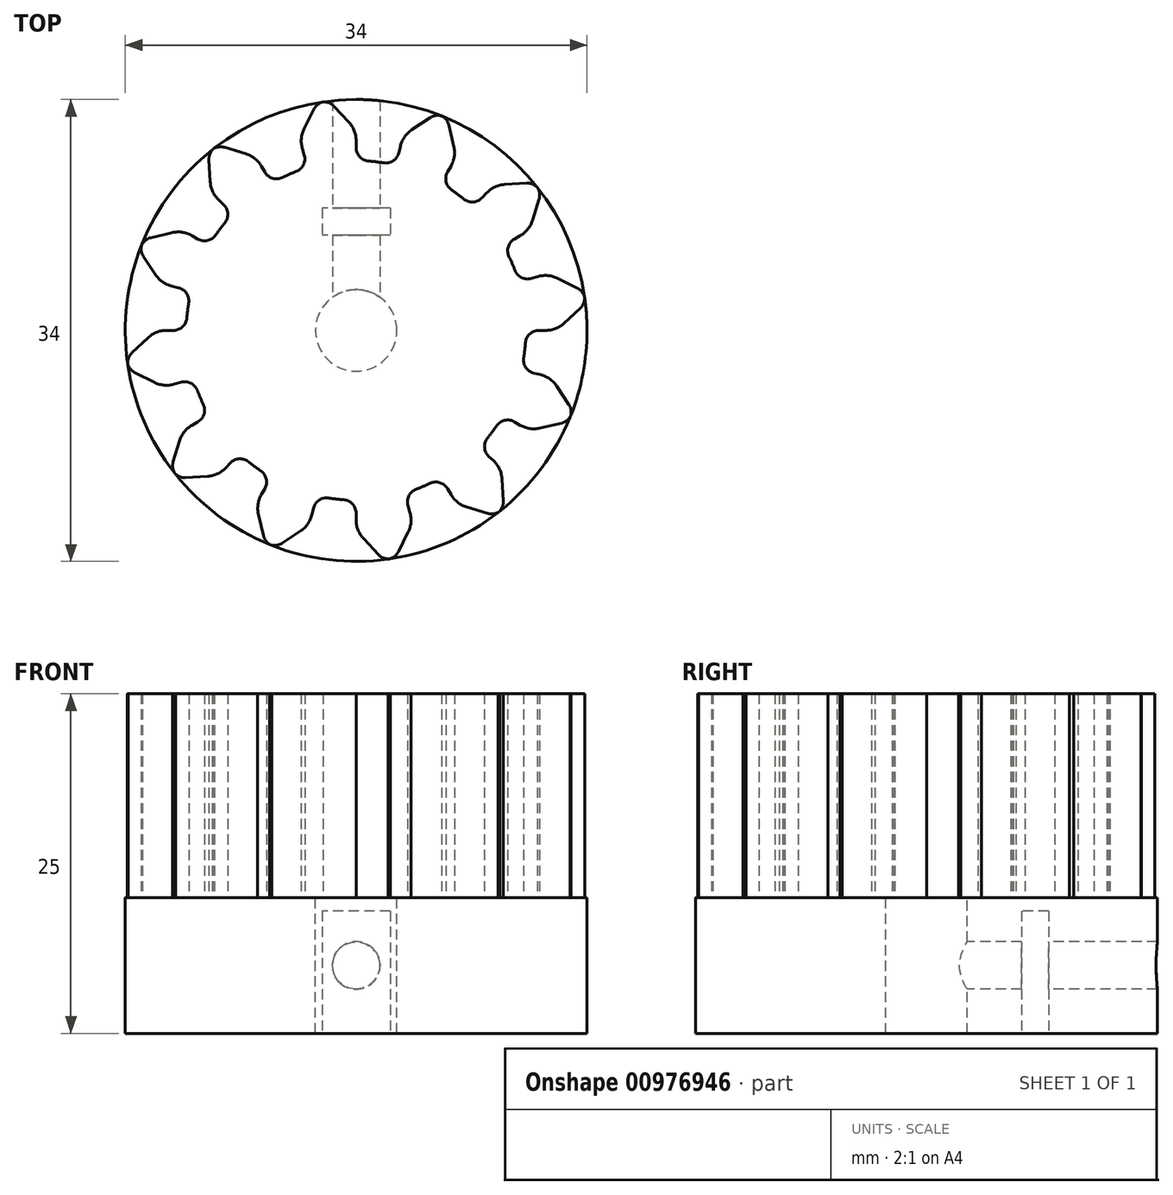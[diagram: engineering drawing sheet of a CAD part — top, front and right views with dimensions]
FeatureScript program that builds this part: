
annotation { "Feature Type Name" : "Feature", "Feature Type Description" : "" }
export const myFeature = defineFeature(function(context is Context, id is Id, definition is map)
    precondition{}
    {
        {
            var Q0;
            Q0=qCreatedBy(makeId("Top.planeOp"),FACE);
            var sketch = newSketch(context, id + "F0", { "sketchPlane" : qUnion([Q0])});
            skLineSegment(sketch, "E0", {"start": v(0, 13.96) * mm, "end": v(0, 13.46) * mm});
            skLineSegment(sketch, "E1", {"start": v(3.15, 13.1) * mm, "end": v(3.26, 13.57) * mm});
            skArc(sketch, "E2", {"start": v(2.01, 12.34) * mm, "mid": v(1.47, 12.41) * mm, "end": v(0.93, 12.47) * mm});
            skLineSegment(sketch, "E3", {"start": v(4.1, 14.78) * mm, "end": v(5.46, 15.67) * mm});
            skLineSegment(sketch, "E4", {"start": v(-0.54, 15.33) * mm, "end": v(-1.64, 16.5) * mm});
            skPoint(sketch, "E5.visualSharp", {"position": v(3.45, 14.34) * mm});
            skArc(sketch, "E5.filletArc", {"start": v(4.1, 14.78) * mm, "mid": v(3.57, 14.26) * mm, "end": v(3.26, 13.57) * mm});
            skPoint(sketch, "E6.visualSharp", {"position": v(0, 14.75) * mm});
            skArc(sketch, "E6.filletArc", {"start": v(0, 13.96) * mm, "mid": v(-0.14, 14.7) * mm, "end": v(-0.54, 15.33) * mm});
            skPoint(sketch, "E7.visualSharp", {"position": v(2.92, 12.15) * mm});
            skArc(sketch, "E7.filletArc", {"start": v(2.01, 12.34) * mm, "mid": v(2.73, 12.5) * mm, "end": v(3.15, 13.1) * mm});
            skPoint(sketch, "E8.visualSharp", {"position": v(0, 12.5) * mm});
            skArc(sketch, "E8.filletArc", {"start": v(0, 13.46) * mm, "mid": v(0.27, 12.78) * mm, "end": v(0.93, 12.47) * mm});
            skPoint(sketch, "E9.visualSharp", {"position": v(-2, 16.88) * mm});
            skArc(sketch, "E9.filletArc", {"start": v(-1.64, 16.5) * mm, "mid": v(-2.05, 16.77) * mm, "end": v(-2.52, 16.81) * mm});
            skPoint(sketch, "E10.visualSharp", {"position": v(5.89, 15.95) * mm});
            skArc(sketch, "E10.filletArc", {"start": v(6.38, 15.76) * mm, "mid": v(5.9, 15.83) * mm, "end": v(5.46, 15.67) * mm});
            skPoint(sketch, "E11.2.0", {"position": v(0, 17) * mm});
            skPoint(sketch, "E11.2.7", {"position": v(3.97, 16.53) * mm});
            skPoint(sketch, "E11.3.0", {"position": v(0, 17) * mm});
            skPoint(sketch, "E11.3.7", {"position": v(3.97, 16.53) * mm});
            skPoint(sketch, "E11.4.0", {"position": v(0, 17) * mm});
            skPoint(sketch, "E11.4.7", {"position": v(3.97, 16.53) * mm});
            skPoint(sketch, "E11.5.0", {"position": v(0, 17) * mm});
            skPoint(sketch, "E11.5.7", {"position": v(3.97, 16.53) * mm});
            skPoint(sketch, "E11.6.0", {"position": v(0, 17) * mm});
            skPoint(sketch, "E11.6.7", {"position": v(3.97, 16.53) * mm});
            skPoint(sketch, "E11.7.0", {"position": v(0, 17) * mm});
            skPoint(sketch, "E11.7.7", {"position": v(3.97, 16.53) * mm});
            skPoint(sketch, "E11.8.0", {"position": v(0, 17) * mm});
            skPoint(sketch, "E11.8.7", {"position": v(3.97, 16.53) * mm});
            skPoint(sketch, "E11.9.0", {"position": v(0, 17) * mm});
            skPoint(sketch, "E11.9.7", {"position": v(3.97, 16.53) * mm});
            skPoint(sketch, "E11.10.0", {"position": v(0, 17) * mm});
            skPoint(sketch, "E11.10.7", {"position": v(3.97, 16.53) * mm});
            skPoint(sketch, "E11.11.0", {"position": v(0, 17) * mm});
            skPoint(sketch, "E11.11.7", {"position": v(3.97, 16.53) * mm});
            skPoint(sketch, "E11.12.0", {"position": v(0, 17) * mm});
            skPoint(sketch, "E11.12.7", {"position": v(3.97, 16.53) * mm});
            skLineSegment(sketch, "E12.1.0", {"start": v(-10.6, 13.3) * mm, "end": v(0, 0) * mm});
            skPoint(sketch, "E12.1.1", {"position": v(-10.17, 13.62) * mm});
            skPoint(sketch, "E12.1.2", {"position": v(-4.82, 16.3) * mm});
            skPoint(sketch, "E12.1.4", {"position": v(-4.19, 14.14) * mm});
            skPoint(sketch, "E12.1.6", {"position": v(-2.88, 16.75) * mm});
            skPoint(sketch, "E12.1.7", {"position": v(-6.25, 10.83) * mm});
            skPoint(sketch, "E12.1.8", {"position": v(-8.5, 14.72) * mm});
            skPoint(sketch, "E12.1.9", {"position": v(-7.38, 12.77) * mm});
            skPoint(sketch, "E12.1.10", {"position": v(-3.55, 11.99) * mm});
            skPoint(sketch, "E12.1.11", {"position": v(-4.82, 16.3) * mm});
            skPoint(sketch, "E12.1.12", {"position": v(-2.88, 16.75) * mm});
            skPoint(sketch, "E12.1.13", {"position": v(-3.55, 11.99) * mm});
            skPoint(sketch, "E12.1.14", {"position": v(-6.25, 10.83) * mm});
            skPoint(sketch, "E12.1.15", {"position": v(-4.19, 14.14) * mm});
            skPoint(sketch, "E12.1.16", {"position": v(-10.17, 13.62) * mm});
            skPoint(sketch, "E12.1.17", {"position": v(-7.38, 12.77) * mm});
            skPoint(sketch, "E12.1.18", {"position": v(-8.5, 14.72) * mm});
            skPoint(sketch, "E12.1.19", {"position": v(-2.88, 16.75) * mm});
            skPoint(sketch, "E12.1.20", {"position": v(-4.82, 16.3) * mm});
            skPoint(sketch, "E12.1.21", {"position": v(-3.55, 11.99) * mm});
            skPoint(sketch, "E12.1.22", {"position": v(-7.38, 12.77) * mm});
            skPoint(sketch, "E12.1.23", {"position": v(-4.19, 14.14) * mm});
            skPoint(sketch, "E12.1.24", {"position": v(-6.25, 10.83) * mm});
            skPoint(sketch, "E12.1.25", {"position": v(-8.5, 14.72) * mm});
            skPoint(sketch, "E12.1.26", {"position": v(-10.17, 13.62) * mm});
            skPoint(sketch, "E12.1.27", {"position": v(-4.82, 16.3) * mm});
            skPoint(sketch, "E12.1.28", {"position": v(-4.19, 14.14) * mm});
            skPoint(sketch, "E12.1.29", {"position": v(-8.5, 14.72) * mm});
            skPoint(sketch, "E12.1.30", {"position": v(-10.17, 13.62) * mm});
            skPoint(sketch, "E12.1.31", {"position": v(-2.88, 16.75) * mm});
            skPoint(sketch, "E12.1.32", {"position": v(-6.25, 10.83) * mm});
            skPoint(sketch, "E12.1.33", {"position": v(-7.38, 12.77) * mm});
            skPoint(sketch, "E12.1.34", {"position": v(-3.55, 11.99) * mm});
            skPoint(sketch, "E12.1.35", {"position": v(-6.25, 10.83) * mm});
            skPoint(sketch, "E12.1.36", {"position": v(-10.17, 13.62) * mm});
            skPoint(sketch, "E12.1.37", {"position": v(-2.88, 16.75) * mm});
            skPoint(sketch, "E12.1.38", {"position": v(-4.82, 16.3) * mm});
            skPoint(sketch, "E12.1.39", {"position": v(-8.5, 14.72) * mm});
            skPoint(sketch, "E12.1.40", {"position": v(-4.19, 14.14) * mm});
            skPoint(sketch, "E12.1.41", {"position": v(-7.38, 12.77) * mm});
            skPoint(sketch, "E12.1.42", {"position": v(-3.55, 11.99) * mm});
            skPoint(sketch, "E12.1.43", {"position": v(-3.55, 11.99) * mm});
            skPoint(sketch, "E12.1.44", {"position": v(-2.88, 16.75) * mm});
            skPoint(sketch, "E12.1.45", {"position": v(-10.17, 13.62) * mm});
            skPoint(sketch, "E12.1.46", {"position": v(-4.82, 16.3) * mm});
            skPoint(sketch, "E12.1.47", {"position": v(-4.19, 14.14) * mm});
            skPoint(sketch, "E12.1.48", {"position": v(-6.25, 10.83) * mm});
            skPoint(sketch, "E12.1.49", {"position": v(-7.38, 12.77) * mm});
            skPoint(sketch, "E12.1.50", {"position": v(-4.19, 14.14) * mm});
            skPoint(sketch, "E12.1.51", {"position": v(-2.88, 16.75) * mm});
            skPoint(sketch, "E12.1.52", {"position": v(-7.38, 12.77) * mm});
            skPoint(sketch, "E12.1.53", {"position": v(-6.25, 10.83) * mm});
            skPoint(sketch, "E12.1.54", {"position": v(-3.55, 11.99) * mm});
            skPoint(sketch, "E12.1.55", {"position": v(-8.5, 14.72) * mm});
            skPoint(sketch, "E12.1.56", {"position": v(-4.82, 16.3) * mm});
            skPoint(sketch, "E12.1.57", {"position": v(-10.17, 13.62) * mm});
            skPoint(sketch, "E12.1.58", {"position": v(-2.88, 16.75) * mm});
            skPoint(sketch, "E12.1.59", {"position": v(-7.37, 12.77) * mm});
            skPoint(sketch, "E12.1.60", {"position": v(-10.17, 13.62) * mm});
            skPoint(sketch, "E12.1.61", {"position": v(-4.19, 14.14) * mm});
            skPoint(sketch, "E12.1.62", {"position": v(-3.55, 11.99) * mm});
            skPoint(sketch, "E12.1.63", {"position": v(-6.25, 10.83) * mm});
            skPoint(sketch, "E12.1.64", {"position": v(-4.82, 16.3) * mm});
            skPoint(sketch, "E12.1.65", {"position": v(-8.5, 14.72) * mm});
            skPoint(sketch, "E12.1.66", {"position": v(-7.38, 12.77) * mm});
            skPoint(sketch, "E12.1.67", {"position": v(-6.25, 10.83) * mm});
            skPoint(sketch, "E12.1.68", {"position": v(-4.19, 14.14) * mm});
            skPoint(sketch, "E12.1.69", {"position": v(-3.55, 11.99) * mm});
            skPoint(sketch, "E12.1.70", {"position": v(-10.17, 13.62) * mm});
            skPoint(sketch, "E12.1.71", {"position": v(-8.5, 14.72) * mm});
            skPoint(sketch, "E12.1.72", {"position": v(-2.88, 16.75) * mm});
            skPoint(sketch, "E12.1.73", {"position": v(-4.82, 16.3) * mm});
            skPoint(sketch, "E12.1.74", {"position": v(-8.5, 14.72) * mm});
            skPoint(sketch, "E12.1.75", {"position": v(-6.25, 10.83) * mm});
            skPoint(sketch, "E12.1.76", {"position": v(-2.88, 16.75) * mm});
            skPoint(sketch, "E12.1.77", {"position": v(-7.38, 12.77) * mm});
            skPoint(sketch, "E12.1.78", {"position": v(-10.17, 13.62) * mm});
            skPoint(sketch, "E12.1.79", {"position": v(-4.19, 14.14) * mm});
            skPoint(sketch, "E12.1.80", {"position": v(-4.82, 16.3) * mm});
            skPoint(sketch, "E12.1.81", {"position": v(-3.55, 11.99) * mm});
            skPoint(sketch, "E12.1.82", {"position": v(-8.5, 14.72) * mm});
            skPoint(sketch, "E12.1.83", {"position": v(-2.88, 16.75) * mm});
            skPoint(sketch, "E12.1.84", {"position": v(-10.17, 13.62) * mm});
            skPoint(sketch, "E12.1.85", {"position": v(-3.55, 11.99) * mm});
            skPoint(sketch, "E12.1.86", {"position": v(-7.38, 12.77) * mm});
            skPoint(sketch, "E12.1.87", {"position": v(-4.19, 14.14) * mm});
            skPoint(sketch, "E12.1.88", {"position": v(-6.25, 10.83) * mm});
            skPoint(sketch, "E12.1.89", {"position": v(-10.17, 13.62) * mm});
            skPoint(sketch, "E12.1.90", {"position": v(-6.25, 10.83) * mm});
            skPoint(sketch, "E12.1.91", {"position": v(-3.55, 11.99) * mm});
            skPoint(sketch, "E12.1.92", {"position": v(-7.38, 12.77) * mm});
            skPoint(sketch, "E12.1.93", {"position": v(-4.19, 14.14) * mm});
            skPoint(sketch, "E12.1.94", {"position": v(-2.88, 16.75) * mm});
            skPoint(sketch, "E12.1.95", {"position": v(-4.19, 14.14) * mm});
            skPoint(sketch, "E12.1.96", {"position": v(-3.55, 11.99) * mm});
            skPoint(sketch, "E12.1.97", {"position": v(-7.37, 12.77) * mm});
            skPoint(sketch, "E12.1.98", {"position": v(-6.25, 10.83) * mm});
            skPoint(sketch, "E12.1.99", {"position": v(-10.17, 13.62) * mm});
            skPoint(sketch, "E12.1.100", {"position": v(-2.88, 16.75) * mm});
            skArc(sketch, "E12.1.101", {"start": v(-3.83, 14.85) * mm, "mid": v(-4.04, 14.13) * mm, "end": v(-3.96, 13.39) * mm});
            skArc(sketch, "E12.1.102", {"start": v(-4.43, 11.7) * mm, "mid": v(-3.88, 12.18) * mm, "end": v(-3.82, 12.9) * mm});
            skArc(sketch, "E12.1.103", {"start": v(-6.73, 11.66) * mm, "mid": v(-6.16, 11.2) * mm, "end": v(-5.43, 11.26) * mm});
            skArc(sketch, "E12.1.104", {"start": v(-3.83, 14.85) * mm, "mid": v(-4.04, 14.13) * mm, "end": v(-3.96, 13.39) * mm});
            skArc(sketch, "E12.1.105", {"start": v(-2.35, 16.84) * mm, "mid": v(-2.8, 16.66) * mm, "end": v(-3.1, 16.3) * mm});
            skArc(sketch, "E12.1.106", {"start": v(-4.43, 11.7) * mm, "mid": v(-3.88, 12.18) * mm, "end": v(-3.82, 12.9) * mm});
            skArc(sketch, "E12.1.107", {"start": v(-6.73, 11.66) * mm, "mid": v(-6.16, 11.2) * mm, "end": v(-5.43, 11.26) * mm});
            skArc(sketch, "E12.1.108", {"start": v(-9.68, 13.47) * mm, "mid": v(-10.16, 13.5) * mm, "end": v(-10.6, 13.3) * mm});
            skArc(sketch, "E12.1.109", {"start": v(-4.43, 11.7) * mm, "mid": v(-3.88, 12.18) * mm, "end": v(-3.82, 12.9) * mm});
            skArc(sketch, "E12.1.110", {"start": v(-6.73, 11.66) * mm, "mid": v(-6.16, 11.2) * mm, "end": v(-5.43, 11.26) * mm});
            skArc(sketch, "E12.1.111", {"start": v(-3.83, 14.85) * mm, "mid": v(-4.04, 14.13) * mm, "end": v(-3.96, 13.39) * mm});
            skArc(sketch, "E12.1.112", {"start": v(-2.35, 16.84) * mm, "mid": v(-2.8, 16.66) * mm, "end": v(-3.1, 16.3) * mm});
            skArc(sketch, "E12.1.113", {"start": v(-9.68, 13.47) * mm, "mid": v(-10.16, 13.5) * mm, "end": v(-10.6, 13.3) * mm});
            skArc(sketch, "E12.1.114", {"start": v(-4.43, 11.7) * mm, "mid": v(-3.88, 12.18) * mm, "end": v(-3.82, 12.9) * mm});
            skArc(sketch, "E12.1.115", {"start": v(-9.68, 13.47) * mm, "mid": v(-10.16, 13.5) * mm, "end": v(-10.6, 13.3) * mm});
            skArc(sketch, "E12.1.116", {"start": v(-6.73, 11.66) * mm, "mid": v(-6.16, 11.2) * mm, "end": v(-5.43, 11.26) * mm});
            skArc(sketch, "E12.1.117", {"start": v(-3.83, 14.85) * mm, "mid": v(-4.04, 14.13) * mm, "end": v(-3.96, 13.39) * mm});
            skArc(sketch, "E12.1.118", {"start": v(-2.35, 16.84) * mm, "mid": v(-2.8, 16.66) * mm, "end": v(-3.1, 16.3) * mm});
            skArc(sketch, "E12.1.119", {"start": v(-9.68, 13.47) * mm, "mid": v(-10.16, 13.5) * mm, "end": v(-10.6, 13.3) * mm});
            skArc(sketch, "E12.1.120", {"start": v(-6.73, 11.66) * mm, "mid": v(-6.16, 11.2) * mm, "end": v(-5.43, 11.26) * mm});
            skArc(sketch, "E12.1.121", {"start": v(-4.43, 11.7) * mm, "mid": v(-3.88, 12.18) * mm, "end": v(-3.82, 12.9) * mm});
            skArc(sketch, "E12.1.122", {"start": v(-3.83, 14.85) * mm, "mid": v(-4.04, 14.13) * mm, "end": v(-3.96, 13.39) * mm});
            skArc(sketch, "E12.1.123", {"start": v(-2.35, 16.84) * mm, "mid": v(-2.8, 16.66) * mm, "end": v(-3.1, 16.3) * mm});
            skArc(sketch, "E12.1.124", {"start": v(-9.68, 13.47) * mm, "mid": v(-10.16, 13.5) * mm, "end": v(-10.6, 13.3) * mm});
            skArc(sketch, "E12.1.125", {"start": v(-4.43, 11.7) * mm, "mid": v(-3.88, 12.18) * mm, "end": v(-3.82, 12.9) * mm});
            skArc(sketch, "E12.1.126", {"start": v(-6.73, 11.66) * mm, "mid": v(-6.16, 11.2) * mm, "end": v(-5.43, 11.26) * mm});
            skArc(sketch, "E12.1.127", {"start": v(-3.83, 14.85) * mm, "mid": v(-4.04, 14.13) * mm, "end": v(-3.96, 13.39) * mm});
            skArc(sketch, "E12.1.128", {"start": v(-2.35, 16.84) * mm, "mid": v(-2.8, 16.66) * mm, "end": v(-3.1, 16.3) * mm});
            skArc(sketch, "E12.1.129", {"start": v(-4.43, 11.7) * mm, "mid": v(-3.88, 12.18) * mm, "end": v(-3.82, 12.9) * mm});
            skArc(sketch, "E12.1.130", {"start": v(-9.68, 13.47) * mm, "mid": v(-10.16, 13.5) * mm, "end": v(-10.6, 13.3) * mm});
            skArc(sketch, "E12.1.131", {"start": v(-6.73, 11.66) * mm, "mid": v(-6.16, 11.2) * mm, "end": v(-5.43, 11.26) * mm});
            skArc(sketch, "E12.1.132", {"start": v(-2.35, 16.84) * mm, "mid": v(-2.8, 16.66) * mm, "end": v(-3.1, 16.3) * mm});
            skArc(sketch, "E12.1.133", {"start": v(-3.83, 14.85) * mm, "mid": v(-4.04, 14.13) * mm, "end": v(-3.96, 13.39) * mm});
            skArc(sketch, "E12.1.134", {"start": v(-3.83, 14.85) * mm, "mid": v(-4.04, 14.13) * mm, "end": v(-3.96, 13.39) * mm});
            skArc(sketch, "E12.1.135", {"start": v(-2.35, 16.84) * mm, "mid": v(-2.8, 16.66) * mm, "end": v(-3.1, 16.3) * mm});
            skArc(sketch, "E12.1.136", {"start": v(-4.43, 11.7) * mm, "mid": v(-3.88, 12.18) * mm, "end": v(-3.82, 12.9) * mm});
            skArc(sketch, "E12.1.137", {"start": v(-9.68, 13.47) * mm, "mid": v(-10.16, 13.5) * mm, "end": v(-10.6, 13.3) * mm});
            skArc(sketch, "E12.1.138", {"start": v(-6.73, 11.66) * mm, "mid": v(-6.16, 11.2) * mm, "end": v(-5.43, 11.26) * mm});
            skArc(sketch, "E12.1.139", {"start": v(-4.43, 11.7) * mm, "mid": v(-3.88, 12.18) * mm, "end": v(-3.82, 12.9) * mm});
            skArc(sketch, "E12.1.140", {"start": v(-6.73, 11.66) * mm, "mid": v(-6.16, 11.2) * mm, "end": v(-5.43, 11.26) * mm});
            skArc(sketch, "E12.1.141", {"start": v(-3.83, 14.85) * mm, "mid": v(-4.04, 14.13) * mm, "end": v(-3.96, 13.39) * mm});
            skArc(sketch, "E12.1.142", {"start": v(-2.35, 16.84) * mm, "mid": v(-2.8, 16.66) * mm, "end": v(-3.1, 16.3) * mm});
            skArc(sketch, "E12.1.143", {"start": v(-9.68, 13.47) * mm, "mid": v(-10.16, 13.5) * mm, "end": v(-10.6, 13.3) * mm});
            skArc(sketch, "E12.1.144", {"start": v(-9.68, 13.47) * mm, "mid": v(-10.16, 13.5) * mm, "end": v(-10.6, 13.3) * mm});
            skArc(sketch, "E12.1.145", {"start": v(-3.83, 14.85) * mm, "mid": v(-4.04, 14.13) * mm, "end": v(-3.96, 13.39) * mm});
            skArc(sketch, "E12.1.146", {"start": v(-4.43, 11.7) * mm, "mid": v(-3.88, 12.18) * mm, "end": v(-3.82, 12.9) * mm});
            skArc(sketch, "E12.1.147", {"start": v(-6.73, 11.66) * mm, "mid": v(-6.16, 11.2) * mm, "end": v(-5.43, 11.26) * mm});
            skArc(sketch, "E12.1.148", {"start": v(-2.35, 16.84) * mm, "mid": v(-2.8, 16.66) * mm, "end": v(-3.1, 16.3) * mm});
            skArc(sketch, "E12.1.149", {"start": v(-4.43, 11.7) * mm, "mid": v(-3.88, 12.18) * mm, "end": v(-3.82, 12.9) * mm});
            skArc(sketch, "E12.1.150", {"start": v(-9.68, 13.47) * mm, "mid": v(-10.16, 13.5) * mm, "end": v(-10.6, 13.3) * mm});
            skArc(sketch, "E12.1.151", {"start": v(-6.73, 11.66) * mm, "mid": v(-6.16, 11.2) * mm, "end": v(-5.43, 11.26) * mm});
            skArc(sketch, "E12.1.152", {"start": v(-2.35, 16.84) * mm, "mid": v(-2.8, 16.66) * mm, "end": v(-3.1, 16.3) * mm});
            skArc(sketch, "E12.1.153", {"start": v(-3.83, 14.85) * mm, "mid": v(-4.04, 14.13) * mm, "end": v(-3.96, 13.39) * mm});
            skArc(sketch, "E12.1.154", {"start": v(-9.68, 13.47) * mm, "mid": v(-10.16, 13.5) * mm, "end": v(-10.6, 13.3) * mm});
            skArc(sketch, "E12.1.155", {"start": v(-2.35, 16.84) * mm, "mid": v(-2.8, 16.66) * mm, "end": v(-3.1, 16.3) * mm});
            skArc(sketch, "E12.1.156", {"start": v(-4.43, 11.7) * mm, "mid": v(-3.88, 12.18) * mm, "end": v(-3.82, 12.9) * mm});
            skArc(sketch, "E12.1.157", {"start": v(-3.83, 14.85) * mm, "mid": v(-4.04, 14.13) * mm, "end": v(-3.96, 13.39) * mm});
            skArc(sketch, "E12.1.158", {"start": v(-6.73, 11.66) * mm, "mid": v(-6.16, 11.2) * mm, "end": v(-5.43, 11.26) * mm});
            skArc(sketch, "E12.1.159", {"start": v(-9.68, 13.47) * mm, "mid": v(-10.16, 13.5) * mm, "end": v(-10.6, 13.3) * mm});
            skArc(sketch, "E12.1.160", {"start": v(-6.73, 11.66) * mm, "mid": v(-6.16, 11.2) * mm, "end": v(-5.43, 11.26) * mm});
            skArc(sketch, "E12.1.161", {"start": v(-4.43, 11.7) * mm, "mid": v(-3.88, 12.18) * mm, "end": v(-3.82, 12.9) * mm});
            skArc(sketch, "E12.1.162", {"start": v(-3.83, 14.85) * mm, "mid": v(-4.04, 14.13) * mm, "end": v(-3.96, 13.39) * mm});
            skArc(sketch, "E12.1.163", {"start": v(-2.35, 16.84) * mm, "mid": v(-2.8, 16.66) * mm, "end": v(-3.1, 16.3) * mm});
            skArc(sketch, "E12.1.164", {"start": v(-6.98, 12.09) * mm, "mid": v(-7.47, 12.66) * mm, "end": v(-8.13, 13) * mm});
            skArc(sketch, "E12.1.165", {"start": v(-4.43, 11.7) * mm, "mid": v(-4.93, 11.49) * mm, "end": v(-5.43, 11.26) * mm});
            skArc(sketch, "E12.1.166", {"start": v(-2.35, 16.84) * mm, "mid": v(-2.8, 16.66) * mm, "end": v(-3.1, 16.3) * mm});
            skLineSegment(sketch, "E12.1.167", {"start": v(-3.83, 14.85) * mm, "end": v(-3.1, 16.3) * mm});
            skLineSegment(sketch, "E12.1.168", {"start": v(-8.13, 13) * mm, "end": v(-9.68, 13.47) * mm});
            skArc(sketch, "E12.1.169", {"start": v(-9.68, 13.47) * mm, "mid": v(-10.16, 13.5) * mm, "end": v(-10.6, 13.3) * mm});
            skLineSegment(sketch, "E12.1.170", {"start": v(-8.13, 13) * mm, "end": v(-9.68, 13.47) * mm});
            skLineSegment(sketch, "E12.1.171", {"start": v(-3.83, 14.85) * mm, "end": v(-3.1, 16.3) * mm});
            skLineSegment(sketch, "E12.1.172", {"start": v(-3.82, 12.9) * mm, "end": v(-3.96, 13.39) * mm});
            skArc(sketch, "E12.1.173", {"start": v(-4.43, 11.7) * mm, "mid": v(-4.93, 11.49) * mm, "end": v(-5.43, 11.26) * mm});
            skArc(sketch, "E12.1.174", {"start": v(-6.98, 12.09) * mm, "mid": v(-7.47, 12.66) * mm, "end": v(-8.13, 13) * mm});
            skLineSegment(sketch, "E12.1.175", {"start": v(-3.83, 14.85) * mm, "end": v(-3.1, 16.3) * mm});
            skArc(sketch, "E12.1.176", {"start": v(-6.98, 12.09) * mm, "mid": v(-7.47, 12.66) * mm, "end": v(-8.13, 13) * mm});
            skLineSegment(sketch, "E12.1.177", {"start": v(-8.13, 13) * mm, "end": v(-9.68, 13.47) * mm});
            skLineSegment(sketch, "E12.1.178", {"start": v(-3.82, 12.9) * mm, "end": v(-3.96, 13.39) * mm});
            skArc(sketch, "E12.1.179", {"start": v(-4.43, 11.7) * mm, "mid": v(-4.93, 11.49) * mm, "end": v(-5.43, 11.26) * mm});
            skLineSegment(sketch, "E12.1.180", {"start": v(-8.13, 13) * mm, "end": v(-9.68, 13.47) * mm});
            skArc(sketch, "E12.1.181", {"start": v(-6.98, 12.09) * mm, "mid": v(-7.47, 12.66) * mm, "end": v(-8.13, 13) * mm});
            skArc(sketch, "E12.1.182", {"start": v(-4.43, 11.7) * mm, "mid": v(-4.93, 11.49) * mm, "end": v(-5.43, 11.26) * mm});
            skLineSegment(sketch, "E12.1.183", {"start": v(-3.82, 12.9) * mm, "end": v(-3.96, 13.39) * mm});
            skLineSegment(sketch, "E12.1.184", {"start": v(-3.83, 14.85) * mm, "end": v(-3.1, 16.3) * mm});
            skArc(sketch, "E12.1.185", {"start": v(-6.98, 12.09) * mm, "mid": v(-7.47, 12.66) * mm, "end": v(-8.13, 13) * mm});
            skLineSegment(sketch, "E12.1.186", {"start": v(-8.13, 13) * mm, "end": v(-9.68, 13.47) * mm});
            skLineSegment(sketch, "E12.1.187", {"start": v(-3.83, 14.85) * mm, "end": v(-3.1, 16.3) * mm});
            skArc(sketch, "E12.1.188", {"start": v(-4.43, 11.7) * mm, "mid": v(-4.93, 11.49) * mm, "end": v(-5.43, 11.26) * mm});
            skLineSegment(sketch, "E12.1.189", {"start": v(-3.82, 12.9) * mm, "end": v(-3.96, 13.39) * mm});
            skArc(sketch, "E12.1.190", {"start": v(-6.98, 12.09) * mm, "mid": v(-7.47, 12.66) * mm, "end": v(-8.13, 13) * mm});
            skLineSegment(sketch, "E12.1.191", {"start": v(-3.83, 14.85) * mm, "end": v(-3.1, 16.3) * mm});
            skArc(sketch, "E12.1.192", {"start": v(-4.43, 11.7) * mm, "mid": v(-4.93, 11.49) * mm, "end": v(-5.43, 11.26) * mm});
            skLineSegment(sketch, "E12.1.193", {"start": v(-8.13, 13) * mm, "end": v(-9.68, 13.47) * mm});
            skLineSegment(sketch, "E12.1.194", {"start": v(-3.82, 12.9) * mm, "end": v(-3.96, 13.39) * mm});
            skLineSegment(sketch, "E12.1.195", {"start": v(-8.13, 13) * mm, "end": v(-9.68, 13.47) * mm});
            skArc(sketch, "E12.1.196", {"start": v(-4.43, 11.7) * mm, "mid": v(-4.93, 11.49) * mm, "end": v(-5.43, 11.26) * mm});
            skLineSegment(sketch, "E12.1.197", {"start": v(-3.83, 14.85) * mm, "end": v(-3.1, 16.3) * mm});
            skArc(sketch, "E12.1.198", {"start": v(-6.98, 12.09) * mm, "mid": v(-7.47, 12.66) * mm, "end": v(-8.13, 13) * mm});
            skLineSegment(sketch, "E12.1.199", {"start": v(-3.82, 12.9) * mm, "end": v(-3.96, 13.39) * mm});
            skLineSegment(sketch, "E12.1.200", {"start": v(-3.83, 14.85) * mm, "end": v(-3.1, 16.3) * mm});
            skArc(sketch, "E12.1.201", {"start": v(-4.43, 11.7) * mm, "mid": v(-4.93, 11.49) * mm, "end": v(-5.43, 11.26) * mm});
            skLineSegment(sketch, "E12.1.202", {"start": v(-6.98, 12.09) * mm, "end": v(-6.73, 11.66) * mm});
            skLineSegment(sketch, "E12.1.203", {"start": v(-8.13, 13) * mm, "end": v(-9.68, 13.47) * mm});
            skArc(sketch, "E12.1.204", {"start": v(-6.98, 12.09) * mm, "mid": v(-7.47, 12.66) * mm, "end": v(-8.13, 13) * mm});
            skLineSegment(sketch, "E12.1.205", {"start": v(-3.82, 12.9) * mm, "end": v(-3.96, 13.39) * mm});
            skLineSegment(sketch, "E12.1.206", {"start": v(-6.98, 12.09) * mm, "end": v(-6.73, 11.66) * mm});
            skLineSegment(sketch, "E12.1.207", {"start": v(-3.82, 12.9) * mm, "end": v(-3.96, 13.39) * mm});
            skArc(sketch, "E12.1.208", {"start": v(-6.98, 12.09) * mm, "mid": v(-7.47, 12.66) * mm, "end": v(-8.13, 13) * mm});
            skLineSegment(sketch, "E12.1.209", {"start": v(-3.83, 14.85) * mm, "end": v(-3.1, 16.3) * mm});
            skArc(sketch, "E12.1.210", {"start": v(-4.43, 11.7) * mm, "mid": v(-4.93, 11.49) * mm, "end": v(-5.43, 11.26) * mm});
            skLineSegment(sketch, "E12.1.211", {"start": v(-8.13, 13) * mm, "end": v(-9.68, 13.47) * mm});
            skArc(sketch, "E12.1.212", {"start": v(-4.43, 11.7) * mm, "mid": v(-4.93, 11.49) * mm, "end": v(-5.43, 11.26) * mm});
            skLineSegment(sketch, "E12.1.213", {"start": v(-8.13, 13) * mm, "end": v(-9.68, 13.47) * mm});
            skLineSegment(sketch, "E12.1.214", {"start": v(-3.83, 14.85) * mm, "end": v(-3.1, 16.3) * mm});
            skLineSegment(sketch, "E12.1.215", {"start": v(-6.98, 12.09) * mm, "end": v(-6.73, 11.66) * mm});
            skArc(sketch, "E12.1.216", {"start": v(-6.98, 12.09) * mm, "mid": v(-7.47, 12.66) * mm, "end": v(-8.13, 13) * mm});
            skLineSegment(sketch, "E12.1.217", {"start": v(-3.82, 12.9) * mm, "end": v(-3.96, 13.39) * mm});
            skLineSegment(sketch, "E12.1.218", {"start": v(-8.13, 13) * mm, "end": v(-9.68, 13.47) * mm});
            skArc(sketch, "E12.1.219", {"start": v(-6.98, 12.09) * mm, "mid": v(-7.47, 12.66) * mm, "end": v(-8.13, 13) * mm});
            skLineSegment(sketch, "E12.1.220", {"start": v(-3.83, 14.85) * mm, "end": v(-3.1, 16.3) * mm});
            skLineSegment(sketch, "E12.1.221", {"start": v(-3.82, 12.9) * mm, "end": v(-3.96, 13.39) * mm});
            skArc(sketch, "E12.1.222", {"start": v(-4.43, 11.7) * mm, "mid": v(-4.93, 11.49) * mm, "end": v(-5.43, 11.26) * mm});
            skLineSegment(sketch, "E12.1.223", {"start": v(-6.98, 12.09) * mm, "end": v(-6.73, 11.66) * mm});
            skLineSegment(sketch, "E12.1.224", {"start": v(-8.13, 13) * mm, "end": v(-9.68, 13.47) * mm});
            skLineSegment(sketch, "E12.1.225", {"start": v(-3.83, 14.85) * mm, "end": v(-3.1, 16.3) * mm});
            skLineSegment(sketch, "E12.1.226", {"start": v(-6.98, 12.09) * mm, "end": v(-6.73, 11.66) * mm});
            skArc(sketch, "E12.1.227", {"start": v(-6.98, 12.09) * mm, "mid": v(-7.47, 12.66) * mm, "end": v(-8.13, 13) * mm});
            skLineSegment(sketch, "E12.1.228", {"start": v(-3.82, 12.9) * mm, "end": v(-3.96, 13.39) * mm});
            skArc(sketch, "E12.1.229", {"start": v(-4.43, 11.7) * mm, "mid": v(-4.93, 11.49) * mm, "end": v(-5.43, 11.26) * mm});
            skArc(sketch, "E12.1.230", {"start": v(-4.43, 11.7) * mm, "mid": v(-4.93, 11.49) * mm, "end": v(-5.43, 11.26) * mm});
            skLineSegment(sketch, "E12.1.231", {"start": v(-3.82, 12.9) * mm, "end": v(-3.96, 13.39) * mm});
            skLineSegment(sketch, "E12.1.232", {"start": v(-8.13, 13) * mm, "end": v(-9.68, 13.47) * mm});
            skLineSegment(sketch, "E12.1.233", {"start": v(-6.98, 12.09) * mm, "end": v(-6.73, 11.66) * mm});
            skArc(sketch, "E12.1.234", {"start": v(-6.98, 12.09) * mm, "mid": v(-7.47, 12.66) * mm, "end": v(-8.13, 13) * mm});
            skLineSegment(sketch, "E12.1.235", {"start": v(-3.83, 14.85) * mm, "end": v(-3.1, 16.3) * mm});
            skLineSegment(sketch, "E12.1.236", {"start": v(-3.82, 12.9) * mm, "end": v(-3.96, 13.39) * mm});
            skLineSegment(sketch, "E12.1.237", {"start": v(-6.98, 12.09) * mm, "end": v(-6.73, 11.66) * mm});
            skLineSegment(sketch, "E12.1.238", {"start": v(-6.98, 12.09) * mm, "end": v(-6.73, 11.66) * mm});
            skLineSegment(sketch, "E12.1.239", {"start": v(-6.98, 12.09) * mm, "end": v(-6.73, 11.66) * mm});
            skLineSegment(sketch, "E12.1.240", {"start": v(-6.98, 12.09) * mm, "end": v(-6.73, 11.66) * mm});
            skLineSegment(sketch, "E12.1.241", {"start": v(-6.98, 12.09) * mm, "end": v(-6.73, 11.66) * mm});
            skLineSegment(sketch, "E12.1.242", {"start": v(-6.98, 12.09) * mm, "end": v(-6.73, 11.66) * mm});
            skLineSegment(sketch, "E12.1.243", {"start": v(-6.98, 12.09) * mm, "end": v(-6.73, 11.66) * mm});
            skLineSegment(sketch, "E12.2.0", {"start": v(-15.82, 6.22) * mm, "end": v(0, 0) * mm});
            skPoint(sketch, "E12.2.1", {"position": v(-15.62, 6.71) * mm});
            skPoint(sketch, "E12.2.2", {"position": v(-12.33, 11.7) * mm});
            skLineSegment(sketch, "E12.2.3", {"start": v(-10.46, 13.4) * mm, "end": v(0, 0) * mm});
            skPoint(sketch, "E12.2.4", {"position": v(-10.7, 10.16) * mm});
            skPoint(sketch, "E12.2.6", {"position": v(-10.87, 13.07) * mm});
            skPoint(sketch, "E12.2.7", {"position": v(-10.83, 6.25) * mm});
            skPoint(sketch, "E12.2.8", {"position": v(-14.72, 8.5) * mm});
            skPoint(sketch, "E12.2.9", {"position": v(-12.77, 7.38) * mm});
            skPoint(sketch, "E12.2.10", {"position": v(-9.07, 8.6) * mm});
            skPoint(sketch, "E12.2.11", {"position": v(-12.33, 11.7) * mm});
            skPoint(sketch, "E12.2.12", {"position": v(-10.87, 13.07) * mm});
            skPoint(sketch, "E12.2.13", {"position": v(-9.07, 8.6) * mm});
            skPoint(sketch, "E12.2.14", {"position": v(-10.83, 6.25) * mm});
            skPoint(sketch, "E12.2.15", {"position": v(-10.7, 10.16) * mm});
            skPoint(sketch, "E12.2.16", {"position": v(-15.62, 6.71) * mm});
            skPoint(sketch, "E12.2.17", {"position": v(-12.77, 7.38) * mm});
            skPoint(sketch, "E12.2.18", {"position": v(-14.72, 8.5) * mm});
            skPoint(sketch, "E12.2.19", {"position": v(-10.87, 13.07) * mm});
            skPoint(sketch, "E12.2.20", {"position": v(-12.33, 11.7) * mm});
            skPoint(sketch, "E12.2.21", {"position": v(-9.07, 8.6) * mm});
            skPoint(sketch, "E12.2.22", {"position": v(-12.77, 7.38) * mm});
            skPoint(sketch, "E12.2.23", {"position": v(-10.7, 10.16) * mm});
            skPoint(sketch, "E12.2.24", {"position": v(-10.83, 6.25) * mm});
            skPoint(sketch, "E12.2.25", {"position": v(-14.72, 8.5) * mm});
            skPoint(sketch, "E12.2.26", {"position": v(-15.62, 6.71) * mm});
            skPoint(sketch, "E12.2.27", {"position": v(-12.33, 11.7) * mm});
            skPoint(sketch, "E12.2.28", {"position": v(-10.7, 10.16) * mm});
            skPoint(sketch, "E12.2.29", {"position": v(-14.72, 8.5) * mm});
            skPoint(sketch, "E12.2.30", {"position": v(-15.62, 6.71) * mm});
            skPoint(sketch, "E12.2.31", {"position": v(-10.87, 13.07) * mm});
            skPoint(sketch, "E12.2.32", {"position": v(-10.83, 6.25) * mm});
            skPoint(sketch, "E12.2.33", {"position": v(-12.77, 7.37) * mm});
            skPoint(sketch, "E12.2.34", {"position": v(-9.07, 8.6) * mm});
            skPoint(sketch, "E12.2.35", {"position": v(-10.83, 6.25) * mm});
            skPoint(sketch, "E12.2.36", {"position": v(-15.62, 6.71) * mm});
            skPoint(sketch, "E12.2.37", {"position": v(-10.87, 13.07) * mm});
            skPoint(sketch, "E12.2.38", {"position": v(-12.33, 11.7) * mm});
            skPoint(sketch, "E12.2.39", {"position": v(-14.72, 8.5) * mm});
            skPoint(sketch, "E12.2.40", {"position": v(-10.7, 10.16) * mm});
            skPoint(sketch, "E12.2.41", {"position": v(-12.77, 7.38) * mm});
            skPoint(sketch, "E12.2.42", {"position": v(-9.07, 8.6) * mm});
            skPoint(sketch, "E12.2.43", {"position": v(-9.07, 8.6) * mm});
            skPoint(sketch, "E12.2.44", {"position": v(-10.87, 13.07) * mm});
            skPoint(sketch, "E12.2.45", {"position": v(-15.62, 6.71) * mm});
            skPoint(sketch, "E12.2.46", {"position": v(-12.33, 11.7) * mm});
            skPoint(sketch, "E12.2.47", {"position": v(-10.7, 10.16) * mm});
            skPoint(sketch, "E12.2.48", {"position": v(-10.83, 6.25) * mm});
            skPoint(sketch, "E12.2.49", {"position": v(-12.77, 7.38) * mm});
            skPoint(sketch, "E12.2.50", {"position": v(-10.7, 10.16) * mm});
            skPoint(sketch, "E12.2.51", {"position": v(-10.87, 13.07) * mm});
            skPoint(sketch, "E12.2.52", {"position": v(-12.77, 7.38) * mm});
            skPoint(sketch, "E12.2.53", {"position": v(-10.83, 6.25) * mm});
            skPoint(sketch, "E12.2.54", {"position": v(-9.07, 8.6) * mm});
            skPoint(sketch, "E12.2.55", {"position": v(-14.72, 8.5) * mm});
            skPoint(sketch, "E12.2.56", {"position": v(-12.33, 11.7) * mm});
            skPoint(sketch, "E12.2.57", {"position": v(-15.62, 6.71) * mm});
            skPoint(sketch, "E12.2.58", {"position": v(-10.87, 13.07) * mm});
            skPoint(sketch, "E12.2.59", {"position": v(-12.77, 7.38) * mm});
            skPoint(sketch, "E12.2.60", {"position": v(-15.62, 6.71) * mm});
            skPoint(sketch, "E12.2.61", {"position": v(-10.7, 10.16) * mm});
            skPoint(sketch, "E12.2.62", {"position": v(-9.07, 8.6) * mm});
            skPoint(sketch, "E12.2.63", {"position": v(-10.83, 6.25) * mm});
            skPoint(sketch, "E12.2.64", {"position": v(-12.33, 11.7) * mm});
            skPoint(sketch, "E12.2.65", {"position": v(-14.72, 8.5) * mm});
            skPoint(sketch, "E12.2.66", {"position": v(-12.77, 7.38) * mm});
            skPoint(sketch, "E12.2.67", {"position": v(-10.83, 6.25) * mm});
            skPoint(sketch, "E12.2.68", {"position": v(-10.7, 10.16) * mm});
            skPoint(sketch, "E12.2.69", {"position": v(-9.07, 8.6) * mm});
            skPoint(sketch, "E12.2.70", {"position": v(-15.62, 6.71) * mm});
            skPoint(sketch, "E12.2.71", {"position": v(-14.72, 8.5) * mm});
            skPoint(sketch, "E12.2.72", {"position": v(-10.87, 13.07) * mm});
            skPoint(sketch, "E12.2.73", {"position": v(-12.33, 11.7) * mm});
            skPoint(sketch, "E12.2.74", {"position": v(-14.72, 8.5) * mm});
            skPoint(sketch, "E12.2.75", {"position": v(-10.83, 6.25) * mm});
            skPoint(sketch, "E12.2.76", {"position": v(-10.87, 13.07) * mm});
            skPoint(sketch, "E12.2.77", {"position": v(-12.77, 7.38) * mm});
            skPoint(sketch, "E12.2.78", {"position": v(-15.62, 6.71) * mm});
            skPoint(sketch, "E12.2.79", {"position": v(-10.7, 10.16) * mm});
            skPoint(sketch, "E12.2.80", {"position": v(-12.33, 11.7) * mm});
            skPoint(sketch, "E12.2.81", {"position": v(-9.07, 8.6) * mm});
            skPoint(sketch, "E12.2.82", {"position": v(-14.72, 8.5) * mm});
            skPoint(sketch, "E12.2.83", {"position": v(-10.87, 13.07) * mm});
            skPoint(sketch, "E12.2.84", {"position": v(-15.62, 6.71) * mm});
            skPoint(sketch, "E12.2.85", {"position": v(-9.07, 8.6) * mm});
            skPoint(sketch, "E12.2.86", {"position": v(-12.77, 7.38) * mm});
            skPoint(sketch, "E12.2.87", {"position": v(-10.7, 10.16) * mm});
            skPoint(sketch, "E12.2.88", {"position": v(-10.83, 6.25) * mm});
            skPoint(sketch, "E12.2.89", {"position": v(-15.62, 6.71) * mm});
            skPoint(sketch, "E12.2.90", {"position": v(-10.83, 6.25) * mm});
            skPoint(sketch, "E12.2.91", {"position": v(-9.07, 8.6) * mm});
            skPoint(sketch, "E12.2.92", {"position": v(-12.77, 7.37) * mm});
            skPoint(sketch, "E12.2.93", {"position": v(-10.7, 10.16) * mm});
            skPoint(sketch, "E12.2.94", {"position": v(-10.87, 13.07) * mm});
            skPoint(sketch, "E12.2.95", {"position": v(-10.7, 10.16) * mm});
            skPoint(sketch, "E12.2.96", {"position": v(-9.07, 8.6) * mm});
            skPoint(sketch, "E12.2.97", {"position": v(-12.77, 7.38) * mm});
            skPoint(sketch, "E12.2.98", {"position": v(-10.83, 6.25) * mm});
            skPoint(sketch, "E12.2.99", {"position": v(-15.62, 6.71) * mm});
            skPoint(sketch, "E12.2.100", {"position": v(-10.87, 13.07) * mm});
            skArc(sketch, "E12.2.101", {"start": v(-10.74, 10.94) * mm, "mid": v(-10.56, 10.22) * mm, "end": v(-10.12, 9.61) * mm});
            skArc(sketch, "E12.2.102", {"start": v(-9.68, 7.91) * mm, "mid": v(-9.45, 8.6) * mm, "end": v(-9.76, 9.27) * mm});
            skArc(sketch, "E12.2.103", {"start": v(-11.66, 6.73) * mm, "mid": v(-10.94, 6.62) * mm, "end": v(-10.33, 7.03) * mm});
            skArc(sketch, "E12.2.104", {"start": v(-10.74, 10.94) * mm, "mid": v(-10.56, 10.22) * mm, "end": v(-10.12, 9.61) * mm});
            skArc(sketch, "E12.2.105", {"start": v(-10.46, 13.4) * mm, "mid": v(-10.75, 13.03) * mm, "end": v(-10.84, 12.56) * mm});
            skArc(sketch, "E12.2.106", {"start": v(-9.68, 7.91) * mm, "mid": v(-9.45, 8.6) * mm, "end": v(-9.76, 9.27) * mm});
            skArc(sketch, "E12.2.107", {"start": v(-11.66, 6.73) * mm, "mid": v(-10.94, 6.62) * mm, "end": v(-10.33, 7.03) * mm});
            skArc(sketch, "E12.2.108", {"start": v(-15.12, 6.83) * mm, "mid": v(-15.54, 6.61) * mm, "end": v(-15.82, 6.22) * mm});
            skArc(sketch, "E12.2.109", {"start": v(-9.68, 7.91) * mm, "mid": v(-9.45, 8.6) * mm, "end": v(-9.76, 9.27) * mm});
            skArc(sketch, "E12.2.110", {"start": v(-11.66, 6.73) * mm, "mid": v(-10.94, 6.62) * mm, "end": v(-10.33, 7.03) * mm});
            skArc(sketch, "E12.2.111", {"start": v(-10.74, 10.94) * mm, "mid": v(-10.56, 10.22) * mm, "end": v(-10.12, 9.61) * mm});
            skArc(sketch, "E12.2.112", {"start": v(-10.46, 13.4) * mm, "mid": v(-10.75, 13.03) * mm, "end": v(-10.84, 12.56) * mm});
            skArc(sketch, "E12.2.113", {"start": v(-15.12, 6.83) * mm, "mid": v(-15.54, 6.61) * mm, "end": v(-15.82, 6.22) * mm});
            skArc(sketch, "E12.2.114", {"start": v(-9.68, 7.91) * mm, "mid": v(-9.45, 8.6) * mm, "end": v(-9.76, 9.27) * mm});
            skArc(sketch, "E12.2.115", {"start": v(-15.12, 6.83) * mm, "mid": v(-15.54, 6.61) * mm, "end": v(-15.82, 6.22) * mm});
            skArc(sketch, "E12.2.116", {"start": v(-11.66, 6.73) * mm, "mid": v(-10.94, 6.62) * mm, "end": v(-10.33, 7.03) * mm});
            skArc(sketch, "E12.2.117", {"start": v(-10.74, 10.94) * mm, "mid": v(-10.56, 10.22) * mm, "end": v(-10.12, 9.61) * mm});
            skArc(sketch, "E12.2.118", {"start": v(-10.46, 13.4) * mm, "mid": v(-10.75, 13.03) * mm, "end": v(-10.84, 12.56) * mm});
            skArc(sketch, "E12.2.119", {"start": v(-15.12, 6.83) * mm, "mid": v(-15.54, 6.61) * mm, "end": v(-15.82, 6.22) * mm});
            skArc(sketch, "E12.2.120", {"start": v(-11.66, 6.73) * mm, "mid": v(-10.94, 6.62) * mm, "end": v(-10.33, 7.03) * mm});
            skArc(sketch, "E12.2.121", {"start": v(-9.68, 7.91) * mm, "mid": v(-9.45, 8.6) * mm, "end": v(-9.76, 9.27) * mm});
            skArc(sketch, "E12.2.122", {"start": v(-10.74, 10.94) * mm, "mid": v(-10.56, 10.22) * mm, "end": v(-10.12, 9.61) * mm});
            skArc(sketch, "E12.2.123", {"start": v(-10.46, 13.4) * mm, "mid": v(-10.75, 13.03) * mm, "end": v(-10.84, 12.56) * mm});
            skArc(sketch, "E12.2.124", {"start": v(-15.12, 6.83) * mm, "mid": v(-15.54, 6.61) * mm, "end": v(-15.82, 6.22) * mm});
            skArc(sketch, "E12.2.125", {"start": v(-9.68, 7.91) * mm, "mid": v(-9.45, 8.6) * mm, "end": v(-9.76, 9.27) * mm});
            skArc(sketch, "E12.2.126", {"start": v(-11.66, 6.73) * mm, "mid": v(-10.94, 6.62) * mm, "end": v(-10.33, 7.03) * mm});
            skArc(sketch, "E12.2.127", {"start": v(-10.74, 10.94) * mm, "mid": v(-10.56, 10.22) * mm, "end": v(-10.12, 9.61) * mm});
            skArc(sketch, "E12.2.128", {"start": v(-10.46, 13.4) * mm, "mid": v(-10.75, 13.03) * mm, "end": v(-10.84, 12.56) * mm});
            skArc(sketch, "E12.2.129", {"start": v(-9.68, 7.91) * mm, "mid": v(-9.45, 8.6) * mm, "end": v(-9.76, 9.27) * mm});
            skArc(sketch, "E12.2.130", {"start": v(-15.12, 6.83) * mm, "mid": v(-15.54, 6.61) * mm, "end": v(-15.82, 6.22) * mm});
            skArc(sketch, "E12.2.131", {"start": v(-11.66, 6.73) * mm, "mid": v(-10.94, 6.62) * mm, "end": v(-10.33, 7.03) * mm});
            skArc(sketch, "E12.2.132", {"start": v(-10.46, 13.4) * mm, "mid": v(-10.75, 13.03) * mm, "end": v(-10.84, 12.56) * mm});
            skArc(sketch, "E12.2.133", {"start": v(-10.74, 10.94) * mm, "mid": v(-10.56, 10.22) * mm, "end": v(-10.12, 9.61) * mm});
            skArc(sketch, "E12.2.134", {"start": v(-10.74, 10.94) * mm, "mid": v(-10.56, 10.22) * mm, "end": v(-10.12, 9.61) * mm});
            skArc(sketch, "E12.2.135", {"start": v(-10.46, 13.4) * mm, "mid": v(-10.75, 13.03) * mm, "end": v(-10.84, 12.56) * mm});
            skArc(sketch, "E12.2.136", {"start": v(-9.68, 7.91) * mm, "mid": v(-9.45, 8.6) * mm, "end": v(-9.76, 9.27) * mm});
            skArc(sketch, "E12.2.137", {"start": v(-15.12, 6.83) * mm, "mid": v(-15.54, 6.61) * mm, "end": v(-15.82, 6.22) * mm});
            skArc(sketch, "E12.2.138", {"start": v(-11.66, 6.73) * mm, "mid": v(-10.94, 6.62) * mm, "end": v(-10.33, 7.03) * mm});
            skArc(sketch, "E12.2.139", {"start": v(-9.68, 7.91) * mm, "mid": v(-9.45, 8.6) * mm, "end": v(-9.76, 9.27) * mm});
            skArc(sketch, "E12.2.140", {"start": v(-11.66, 6.73) * mm, "mid": v(-10.94, 6.62) * mm, "end": v(-10.33, 7.03) * mm});
            skArc(sketch, "E12.2.141", {"start": v(-10.74, 10.94) * mm, "mid": v(-10.56, 10.22) * mm, "end": v(-10.12, 9.61) * mm});
            skArc(sketch, "E12.2.142", {"start": v(-10.46, 13.4) * mm, "mid": v(-10.75, 13.03) * mm, "end": v(-10.84, 12.56) * mm});
            skArc(sketch, "E12.2.143", {"start": v(-15.12, 6.83) * mm, "mid": v(-15.54, 6.61) * mm, "end": v(-15.82, 6.22) * mm});
            skArc(sketch, "E12.2.144", {"start": v(-15.12, 6.83) * mm, "mid": v(-15.54, 6.61) * mm, "end": v(-15.82, 6.22) * mm});
            skArc(sketch, "E12.2.145", {"start": v(-10.74, 10.94) * mm, "mid": v(-10.56, 10.22) * mm, "end": v(-10.12, 9.61) * mm});
            skArc(sketch, "E12.2.146", {"start": v(-9.68, 7.91) * mm, "mid": v(-9.45, 8.6) * mm, "end": v(-9.76, 9.27) * mm});
            skArc(sketch, "E12.2.147", {"start": v(-11.66, 6.73) * mm, "mid": v(-10.94, 6.62) * mm, "end": v(-10.33, 7.03) * mm});
            skArc(sketch, "E12.2.148", {"start": v(-10.46, 13.4) * mm, "mid": v(-10.75, 13.03) * mm, "end": v(-10.84, 12.56) * mm});
            skArc(sketch, "E12.2.149", {"start": v(-9.68, 7.91) * mm, "mid": v(-9.45, 8.6) * mm, "end": v(-9.76, 9.27) * mm});
            skArc(sketch, "E12.2.150", {"start": v(-15.12, 6.83) * mm, "mid": v(-15.54, 6.61) * mm, "end": v(-15.82, 6.22) * mm});
            skArc(sketch, "E12.2.151", {"start": v(-11.66, 6.73) * mm, "mid": v(-10.94, 6.62) * mm, "end": v(-10.33, 7.03) * mm});
            skArc(sketch, "E12.2.152", {"start": v(-10.46, 13.4) * mm, "mid": v(-10.75, 13.03) * mm, "end": v(-10.84, 12.56) * mm});
            skArc(sketch, "E12.2.153", {"start": v(-10.74, 10.94) * mm, "mid": v(-10.56, 10.22) * mm, "end": v(-10.12, 9.61) * mm});
            skArc(sketch, "E12.2.154", {"start": v(-15.12, 6.83) * mm, "mid": v(-15.54, 6.61) * mm, "end": v(-15.82, 6.22) * mm});
            skArc(sketch, "E12.2.155", {"start": v(-10.46, 13.4) * mm, "mid": v(-10.75, 13.03) * mm, "end": v(-10.84, 12.56) * mm});
            skArc(sketch, "E12.2.156", {"start": v(-9.68, 7.91) * mm, "mid": v(-9.45, 8.6) * mm, "end": v(-9.76, 9.27) * mm});
            skArc(sketch, "E12.2.157", {"start": v(-10.74, 10.94) * mm, "mid": v(-10.56, 10.22) * mm, "end": v(-10.12, 9.61) * mm});
            skArc(sketch, "E12.2.158", {"start": v(-11.66, 6.73) * mm, "mid": v(-10.94, 6.62) * mm, "end": v(-10.33, 7.03) * mm});
            skArc(sketch, "E12.2.159", {"start": v(-15.12, 6.83) * mm, "mid": v(-15.54, 6.61) * mm, "end": v(-15.82, 6.22) * mm});
            skArc(sketch, "E12.2.160", {"start": v(-11.66, 6.73) * mm, "mid": v(-10.94, 6.62) * mm, "end": v(-10.33, 7.03) * mm});
            skArc(sketch, "E12.2.161", {"start": v(-9.68, 7.91) * mm, "mid": v(-9.45, 8.6) * mm, "end": v(-9.76, 9.27) * mm});
            skArc(sketch, "E12.2.162", {"start": v(-10.74, 10.94) * mm, "mid": v(-10.56, 10.22) * mm, "end": v(-10.12, 9.61) * mm});
            skArc(sketch, "E12.2.163", {"start": v(-10.46, 13.4) * mm, "mid": v(-10.75, 13.03) * mm, "end": v(-10.84, 12.56) * mm});
            skArc(sketch, "E12.2.164", {"start": v(-12.09, 6.98) * mm, "mid": v(-12.8, 7.23) * mm, "end": v(-13.54, 7.2) * mm});
            skArc(sketch, "E12.2.165", {"start": v(-9.68, 7.91) * mm, "mid": v(-10.01, 7.48) * mm, "end": v(-10.33, 7.03) * mm});
            skArc(sketch, "E12.2.166", {"start": v(-10.46, 13.4) * mm, "mid": v(-10.75, 13.03) * mm, "end": v(-10.84, 12.56) * mm});
            skLineSegment(sketch, "E12.2.167", {"start": v(-10.74, 10.94) * mm, "end": v(-10.84, 12.56) * mm});
            skLineSegment(sketch, "E12.2.168", {"start": v(-13.54, 7.2) * mm, "end": v(-15.12, 6.83) * mm});
            skArc(sketch, "E12.2.169", {"start": v(-15.12, 6.83) * mm, "mid": v(-15.54, 6.61) * mm, "end": v(-15.82, 6.22) * mm});
            skLineSegment(sketch, "E12.2.170", {"start": v(-13.54, 7.2) * mm, "end": v(-15.12, 6.83) * mm});
            skLineSegment(sketch, "E12.2.171", {"start": v(-10.74, 10.94) * mm, "end": v(-10.84, 12.56) * mm});
            skLineSegment(sketch, "E12.2.172", {"start": v(-9.76, 9.27) * mm, "end": v(-10.12, 9.61) * mm});
            skArc(sketch, "E12.2.173", {"start": v(-9.68, 7.91) * mm, "mid": v(-10.01, 7.48) * mm, "end": v(-10.33, 7.03) * mm});
            skArc(sketch, "E12.2.174", {"start": v(-12.09, 6.98) * mm, "mid": v(-12.8, 7.23) * mm, "end": v(-13.54, 7.2) * mm});
            skLineSegment(sketch, "E12.2.175", {"start": v(-10.74, 10.94) * mm, "end": v(-10.84, 12.56) * mm});
            skArc(sketch, "E12.2.176", {"start": v(-12.09, 6.98) * mm, "mid": v(-12.8, 7.23) * mm, "end": v(-13.54, 7.2) * mm});
            skLineSegment(sketch, "E12.2.177", {"start": v(-13.54, 7.2) * mm, "end": v(-15.12, 6.83) * mm});
            skLineSegment(sketch, "E12.2.178", {"start": v(-9.76, 9.27) * mm, "end": v(-10.12, 9.61) * mm});
            skArc(sketch, "E12.2.179", {"start": v(-9.68, 7.91) * mm, "mid": v(-10.01, 7.48) * mm, "end": v(-10.33, 7.03) * mm});
            skLineSegment(sketch, "E12.2.180", {"start": v(-13.54, 7.2) * mm, "end": v(-15.12, 6.83) * mm});
            skArc(sketch, "E12.2.181", {"start": v(-12.09, 6.98) * mm, "mid": v(-12.8, 7.23) * mm, "end": v(-13.54, 7.2) * mm});
            skArc(sketch, "E12.2.182", {"start": v(-9.68, 7.91) * mm, "mid": v(-10.01, 7.48) * mm, "end": v(-10.33, 7.03) * mm});
            skLineSegment(sketch, "E12.2.183", {"start": v(-9.76, 9.27) * mm, "end": v(-10.12, 9.61) * mm});
            skLineSegment(sketch, "E12.2.184", {"start": v(-10.74, 10.94) * mm, "end": v(-10.84, 12.56) * mm});
            skArc(sketch, "E12.2.185", {"start": v(-12.09, 6.98) * mm, "mid": v(-12.8, 7.23) * mm, "end": v(-13.54, 7.2) * mm});
            skLineSegment(sketch, "E12.2.186", {"start": v(-13.54, 7.2) * mm, "end": v(-15.12, 6.83) * mm});
            skLineSegment(sketch, "E12.2.187", {"start": v(-10.74, 10.94) * mm, "end": v(-10.84, 12.56) * mm});
            skArc(sketch, "E12.2.188", {"start": v(-9.68, 7.91) * mm, "mid": v(-10.01, 7.48) * mm, "end": v(-10.33, 7.03) * mm});
            skLineSegment(sketch, "E12.2.189", {"start": v(-9.76, 9.27) * mm, "end": v(-10.12, 9.61) * mm});
            skArc(sketch, "E12.2.190", {"start": v(-12.09, 6.98) * mm, "mid": v(-12.8, 7.23) * mm, "end": v(-13.54, 7.2) * mm});
            skLineSegment(sketch, "E12.2.191", {"start": v(-10.74, 10.94) * mm, "end": v(-10.84, 12.56) * mm});
            skArc(sketch, "E12.2.192", {"start": v(-9.68, 7.91) * mm, "mid": v(-10.01, 7.48) * mm, "end": v(-10.33, 7.03) * mm});
            skLineSegment(sketch, "E12.2.193", {"start": v(-13.54, 7.2) * mm, "end": v(-15.12, 6.83) * mm});
            skLineSegment(sketch, "E12.2.194", {"start": v(-9.76, 9.27) * mm, "end": v(-10.12, 9.61) * mm});
            skLineSegment(sketch, "E12.2.195", {"start": v(-13.54, 7.2) * mm, "end": v(-15.12, 6.83) * mm});
            skArc(sketch, "E12.2.196", {"start": v(-9.68, 7.91) * mm, "mid": v(-10.01, 7.48) * mm, "end": v(-10.33, 7.03) * mm});
            skLineSegment(sketch, "E12.2.197", {"start": v(-10.74, 10.94) * mm, "end": v(-10.84, 12.56) * mm});
            skArc(sketch, "E12.2.198", {"start": v(-12.09, 6.98) * mm, "mid": v(-12.8, 7.23) * mm, "end": v(-13.54, 7.2) * mm});
            skLineSegment(sketch, "E12.2.199", {"start": v(-9.76, 9.27) * mm, "end": v(-10.12, 9.61) * mm});
            skLineSegment(sketch, "E12.2.200", {"start": v(-10.74, 10.94) * mm, "end": v(-10.84, 12.56) * mm});
            skArc(sketch, "E12.2.201", {"start": v(-9.68, 7.91) * mm, "mid": v(-10.01, 7.48) * mm, "end": v(-10.33, 7.03) * mm});
            skLineSegment(sketch, "E12.2.202", {"start": v(-12.09, 6.98) * mm, "end": v(-11.66, 6.73) * mm});
            skLineSegment(sketch, "E12.2.203", {"start": v(-13.54, 7.2) * mm, "end": v(-15.12, 6.83) * mm});
            skArc(sketch, "E12.2.204", {"start": v(-12.09, 6.98) * mm, "mid": v(-12.8, 7.23) * mm, "end": v(-13.54, 7.2) * mm});
            skLineSegment(sketch, "E12.2.205", {"start": v(-9.76, 9.27) * mm, "end": v(-10.12, 9.61) * mm});
            skLineSegment(sketch, "E12.2.206", {"start": v(-12.09, 6.98) * mm, "end": v(-11.66, 6.73) * mm});
            skLineSegment(sketch, "E12.2.207", {"start": v(-9.76, 9.27) * mm, "end": v(-10.12, 9.61) * mm});
            skArc(sketch, "E12.2.208", {"start": v(-12.09, 6.98) * mm, "mid": v(-12.8, 7.23) * mm, "end": v(-13.54, 7.2) * mm});
            skLineSegment(sketch, "E12.2.209", {"start": v(-10.74, 10.94) * mm, "end": v(-10.84, 12.56) * mm});
            skArc(sketch, "E12.2.210", {"start": v(-9.68, 7.91) * mm, "mid": v(-10.01, 7.48) * mm, "end": v(-10.33, 7.03) * mm});
            skLineSegment(sketch, "E12.2.211", {"start": v(-13.54, 7.2) * mm, "end": v(-15.12, 6.83) * mm});
            skArc(sketch, "E12.2.212", {"start": v(-9.68, 7.91) * mm, "mid": v(-10.01, 7.48) * mm, "end": v(-10.33, 7.03) * mm});
            skLineSegment(sketch, "E12.2.213", {"start": v(-13.54, 7.2) * mm, "end": v(-15.12, 6.83) * mm});
            skLineSegment(sketch, "E12.2.214", {"start": v(-10.74, 10.94) * mm, "end": v(-10.84, 12.56) * mm});
            skLineSegment(sketch, "E12.2.215", {"start": v(-12.09, 6.98) * mm, "end": v(-11.66, 6.73) * mm});
            skArc(sketch, "E12.2.216", {"start": v(-12.09, 6.98) * mm, "mid": v(-12.8, 7.23) * mm, "end": v(-13.54, 7.2) * mm});
            skLineSegment(sketch, "E12.2.217", {"start": v(-9.76, 9.27) * mm, "end": v(-10.12, 9.61) * mm});
            skLineSegment(sketch, "E12.2.218", {"start": v(-13.54, 7.2) * mm, "end": v(-15.12, 6.83) * mm});
            skArc(sketch, "E12.2.219", {"start": v(-12.09, 6.98) * mm, "mid": v(-12.8, 7.23) * mm, "end": v(-13.54, 7.2) * mm});
            skLineSegment(sketch, "E12.2.220", {"start": v(-10.74, 10.94) * mm, "end": v(-10.84, 12.56) * mm});
            skLineSegment(sketch, "E12.2.221", {"start": v(-9.76, 9.27) * mm, "end": v(-10.12, 9.61) * mm});
            skArc(sketch, "E12.2.222", {"start": v(-9.68, 7.91) * mm, "mid": v(-10.01, 7.48) * mm, "end": v(-10.33, 7.03) * mm});
            skLineSegment(sketch, "E12.2.223", {"start": v(-12.09, 6.98) * mm, "end": v(-11.66, 6.73) * mm});
            skLineSegment(sketch, "E12.2.224", {"start": v(-13.54, 7.2) * mm, "end": v(-15.12, 6.83) * mm});
            skLineSegment(sketch, "E12.2.225", {"start": v(-10.74, 10.94) * mm, "end": v(-10.84, 12.56) * mm});
            skLineSegment(sketch, "E12.2.226", {"start": v(-12.09, 6.98) * mm, "end": v(-11.66, 6.73) * mm});
            skArc(sketch, "E12.2.227", {"start": v(-12.09, 6.98) * mm, "mid": v(-12.8, 7.23) * mm, "end": v(-13.54, 7.2) * mm});
            skLineSegment(sketch, "E12.2.228", {"start": v(-9.76, 9.27) * mm, "end": v(-10.12, 9.61) * mm});
            skArc(sketch, "E12.2.229", {"start": v(-9.68, 7.91) * mm, "mid": v(-10.01, 7.48) * mm, "end": v(-10.33, 7.03) * mm});
            skArc(sketch, "E12.2.230", {"start": v(-9.68, 7.91) * mm, "mid": v(-10.01, 7.48) * mm, "end": v(-10.33, 7.03) * mm});
            skLineSegment(sketch, "E12.2.231", {"start": v(-9.76, 9.27) * mm, "end": v(-10.12, 9.61) * mm});
            skLineSegment(sketch, "E12.2.232", {"start": v(-13.54, 7.2) * mm, "end": v(-15.12, 6.83) * mm});
            skLineSegment(sketch, "E12.2.233", {"start": v(-12.09, 6.98) * mm, "end": v(-11.66, 6.73) * mm});
            skArc(sketch, "E12.2.234", {"start": v(-12.09, 6.98) * mm, "mid": v(-12.8, 7.23) * mm, "end": v(-13.54, 7.2) * mm});
            skLineSegment(sketch, "E12.2.235", {"start": v(-10.74, 10.94) * mm, "end": v(-10.84, 12.56) * mm});
            skLineSegment(sketch, "E12.2.236", {"start": v(-9.76, 9.27) * mm, "end": v(-10.12, 9.61) * mm});
            skLineSegment(sketch, "E12.2.237", {"start": v(-12.09, 6.98) * mm, "end": v(-11.66, 6.73) * mm});
            skLineSegment(sketch, "E12.2.238", {"start": v(-12.09, 6.98) * mm, "end": v(-11.66, 6.73) * mm});
            skLineSegment(sketch, "E12.2.239", {"start": v(-12.09, 6.98) * mm, "end": v(-11.66, 6.73) * mm});
            skLineSegment(sketch, "E12.2.240", {"start": v(-12.09, 6.98) * mm, "end": v(-11.66, 6.73) * mm});
            skLineSegment(sketch, "E12.2.241", {"start": v(-12.09, 6.98) * mm, "end": v(-11.66, 6.73) * mm});
            skLineSegment(sketch, "E12.2.242", {"start": v(-12.09, 6.98) * mm, "end": v(-11.66, 6.73) * mm});
            skLineSegment(sketch, "E12.2.243", {"start": v(-12.09, 6.98) * mm, "end": v(-11.66, 6.73) * mm});
            skLineSegment(sketch, "E12.3.0", {"start": v(-16.81, -2.52) * mm, "end": v(0, 0) * mm});
            skPoint(sketch, "E12.3.1", {"position": v(-16.88, -2) * mm});
            skPoint(sketch, "E12.3.2", {"position": v(-16.53, 3.97) * mm});
            skLineSegment(sketch, "E12.3.3", {"start": v(-15.76, 6.38) * mm, "end": v(0, 0) * mm});
            skPoint(sketch, "E12.3.4", {"position": v(-14.34, 3.45) * mm});
            skPoint(sketch, "E12.3.6", {"position": v(-15.95, 5.89) * mm});
            skPoint(sketch, "E12.3.7", {"position": v(-12.5, 0) * mm});
            skPoint(sketch, "E12.3.8", {"position": v(-17, 0) * mm});
            skPoint(sketch, "E12.3.9", {"position": v(-14.75, 0) * mm});
            skPoint(sketch, "E12.3.10", {"position": v(-12.15, 2.92) * mm});
            skPoint(sketch, "E12.3.11", {"position": v(-16.53, 3.97) * mm});
            skPoint(sketch, "E12.3.12", {"position": v(-15.95, 5.89) * mm});
            skPoint(sketch, "E12.3.13", {"position": v(-12.15, 2.92) * mm});
            skPoint(sketch, "E12.3.14", {"position": v(-12.5, 0) * mm});
            skPoint(sketch, "E12.3.15", {"position": v(-14.34, 3.45) * mm});
            skPoint(sketch, "E12.3.16", {"position": v(-16.88, -2) * mm});
            skPoint(sketch, "E12.3.17", {"position": v(-14.75, 0) * mm});
            skPoint(sketch, "E12.3.18", {"position": v(-17, 0) * mm});
            skPoint(sketch, "E12.3.19", {"position": v(-15.95, 5.89) * mm});
            skPoint(sketch, "E12.3.20", {"position": v(-16.53, 3.97) * mm});
            skPoint(sketch, "E12.3.21", {"position": v(-12.15, 2.92) * mm});
            skPoint(sketch, "E12.3.22", {"position": v(-14.75, 0) * mm});
            skPoint(sketch, "E12.3.23", {"position": v(-14.34, 3.45) * mm});
            skPoint(sketch, "E12.3.24", {"position": v(-12.5, 0) * mm});
            skPoint(sketch, "E12.3.25", {"position": v(-17, 0) * mm});
            skPoint(sketch, "E12.3.26", {"position": v(-16.88, -2) * mm});
            skPoint(sketch, "E12.3.27", {"position": v(-16.53, 3.97) * mm});
            skPoint(sketch, "E12.3.28", {"position": v(-14.34, 3.45) * mm});
            skPoint(sketch, "E12.3.29", {"position": v(-17, 0) * mm});
            skPoint(sketch, "E12.3.30", {"position": v(-16.88, -2) * mm});
            skPoint(sketch, "E12.3.31", {"position": v(-15.95, 5.89) * mm});
            skPoint(sketch, "E12.3.32", {"position": v(-12.5, 0) * mm});
            skPoint(sketch, "E12.3.33", {"position": v(-14.75, 0) * mm});
            skPoint(sketch, "E12.3.34", {"position": v(-12.15, 2.92) * mm});
            skPoint(sketch, "E12.3.35", {"position": v(-12.5, 0) * mm});
            skPoint(sketch, "E12.3.36", {"position": v(-16.88, -2) * mm});
            skPoint(sketch, "E12.3.37", {"position": v(-15.95, 5.89) * mm});
            skPoint(sketch, "E12.3.38", {"position": v(-16.53, 3.97) * mm});
            skPoint(sketch, "E12.3.39", {"position": v(-17, 0) * mm});
            skPoint(sketch, "E12.3.40", {"position": v(-14.34, 3.45) * mm});
            skPoint(sketch, "E12.3.41", {"position": v(-14.75, 0) * mm});
            skPoint(sketch, "E12.3.42", {"position": v(-12.15, 2.92) * mm});
            skPoint(sketch, "E12.3.43", {"position": v(-12.15, 2.92) * mm});
            skPoint(sketch, "E12.3.44", {"position": v(-15.95, 5.89) * mm});
            skPoint(sketch, "E12.3.45", {"position": v(-16.88, -2) * mm});
            skPoint(sketch, "E12.3.46", {"position": v(-16.53, 3.97) * mm});
            skPoint(sketch, "E12.3.47", {"position": v(-14.34, 3.45) * mm});
            skPoint(sketch, "E12.3.48", {"position": v(-12.5, 0) * mm});
            skPoint(sketch, "E12.3.49", {"position": v(-14.75, 0) * mm});
            skPoint(sketch, "E12.3.50", {"position": v(-14.34, 3.45) * mm});
            skPoint(sketch, "E12.3.51", {"position": v(-15.95, 5.89) * mm});
            skPoint(sketch, "E12.3.52", {"position": v(-14.75, 0) * mm});
            skPoint(sketch, "E12.3.53", {"position": v(-12.5, 0) * mm});
            skPoint(sketch, "E12.3.54", {"position": v(-12.15, 2.92) * mm});
            skPoint(sketch, "E12.3.55", {"position": v(-17, 0) * mm});
            skPoint(sketch, "E12.3.56", {"position": v(-16.53, 3.97) * mm});
            skPoint(sketch, "E12.3.57", {"position": v(-16.88, -2) * mm});
            skPoint(sketch, "E12.3.58", {"position": v(-15.95, 5.89) * mm});
            skPoint(sketch, "E12.3.59", {"position": v(-14.75, 0) * mm});
            skPoint(sketch, "E12.3.60", {"position": v(-16.88, -2) * mm});
            skPoint(sketch, "E12.3.61", {"position": v(-14.34, 3.45) * mm});
            skPoint(sketch, "E12.3.62", {"position": v(-12.15, 2.92) * mm});
            skPoint(sketch, "E12.3.63", {"position": v(-12.5, 0) * mm});
            skPoint(sketch, "E12.3.64", {"position": v(-16.53, 3.97) * mm});
            skPoint(sketch, "E12.3.65", {"position": v(-17, 0) * mm});
            skPoint(sketch, "E12.3.66", {"position": v(-14.75, 0) * mm});
            skPoint(sketch, "E12.3.67", {"position": v(-12.5, 0) * mm});
            skPoint(sketch, "E12.3.68", {"position": v(-14.34, 3.45) * mm});
            skPoint(sketch, "E12.3.69", {"position": v(-12.15, 2.92) * mm});
            skPoint(sketch, "E12.3.70", {"position": v(-16.88, -2) * mm});
            skPoint(sketch, "E12.3.71", {"position": v(-17, 0) * mm});
            skPoint(sketch, "E12.3.72", {"position": v(-15.95, 5.89) * mm});
            skPoint(sketch, "E12.3.73", {"position": v(-16.53, 3.97) * mm});
            skPoint(sketch, "E12.3.74", {"position": v(-17, 0) * mm});
            skPoint(sketch, "E12.3.75", {"position": v(-12.5, 0) * mm});
            skPoint(sketch, "E12.3.76", {"position": v(-15.95, 5.89) * mm});
            skPoint(sketch, "E12.3.77", {"position": v(-14.75, 0) * mm});
            skPoint(sketch, "E12.3.78", {"position": v(-16.88, -2) * mm});
            skPoint(sketch, "E12.3.79", {"position": v(-14.34, 3.45) * mm});
            skPoint(sketch, "E12.3.80", {"position": v(-16.53, 3.97) * mm});
            skPoint(sketch, "E12.3.81", {"position": v(-12.15, 2.92) * mm});
            skPoint(sketch, "E12.3.82", {"position": v(-17, 0) * mm});
            skPoint(sketch, "E12.3.83", {"position": v(-15.95, 5.89) * mm});
            skPoint(sketch, "E12.3.84", {"position": v(-16.88, -2) * mm});
            skPoint(sketch, "E12.3.85", {"position": v(-12.15, 2.92) * mm});
            skPoint(sketch, "E12.3.86", {"position": v(-14.75, 0) * mm});
            skPoint(sketch, "E12.3.87", {"position": v(-14.34, 3.45) * mm});
            skPoint(sketch, "E12.3.88", {"position": v(-12.5, 0) * mm});
            skPoint(sketch, "E12.3.89", {"position": v(-16.88, -2) * mm});
            skPoint(sketch, "E12.3.90", {"position": v(-12.5, 0) * mm});
            skPoint(sketch, "E12.3.91", {"position": v(-12.15, 2.92) * mm});
            skPoint(sketch, "E12.3.92", {"position": v(-14.75, 0) * mm});
            skPoint(sketch, "E12.3.93", {"position": v(-14.34, 3.45) * mm});
            skPoint(sketch, "E12.3.94", {"position": v(-15.95, 5.89) * mm});
            skPoint(sketch, "E12.3.95", {"position": v(-14.34, 3.45) * mm});
            skPoint(sketch, "E12.3.96", {"position": v(-12.15, 2.92) * mm});
            skPoint(sketch, "E12.3.97", {"position": v(-14.75, 0) * mm});
            skPoint(sketch, "E12.3.98", {"position": v(-12.5, 0) * mm});
            skPoint(sketch, "E12.3.99", {"position": v(-16.88, -2) * mm});
            skPoint(sketch, "E12.3.100", {"position": v(-15.95, 5.89) * mm});
            skArc(sketch, "E12.3.101", {"start": v(-14.78, 4.1) * mm, "mid": v(-14.26, 3.57) * mm, "end": v(-13.57, 3.26) * mm});
            skArc(sketch, "E12.3.102", {"start": v(-12.34, 2.01) * mm, "mid": v(-12.5, 2.73) * mm, "end": v(-13.1, 3.15) * mm});
            skArc(sketch, "E12.3.103", {"start": v(-13.46, 0) * mm, "mid": v(-12.78, 0.27) * mm, "end": v(-12.47, 0.93) * mm});
            skArc(sketch, "E12.3.104", {"start": v(-14.78, 4.1) * mm, "mid": v(-14.26, 3.57) * mm, "end": v(-13.57, 3.26) * mm});
            skArc(sketch, "E12.3.105", {"start": v(-15.76, 6.38) * mm, "mid": v(-15.83, 5.9) * mm, "end": v(-15.67, 5.46) * mm});
            skArc(sketch, "E12.3.106", {"start": v(-12.34, 2.01) * mm, "mid": v(-12.5, 2.73) * mm, "end": v(-13.1, 3.15) * mm});
            skArc(sketch, "E12.3.107", {"start": v(-13.46, 0) * mm, "mid": v(-12.78, 0.27) * mm, "end": v(-12.47, 0.93) * mm});
            skArc(sketch, "E12.3.108", {"start": v(-16.5, -1.64) * mm, "mid": v(-16.77, -2.05) * mm, "end": v(-16.81, -2.52) * mm});
            skArc(sketch, "E12.3.109", {"start": v(-12.34, 2.01) * mm, "mid": v(-12.5, 2.73) * mm, "end": v(-13.1, 3.15) * mm});
            skArc(sketch, "E12.3.110", {"start": v(-13.46, 0) * mm, "mid": v(-12.78, 0.27) * mm, "end": v(-12.47, 0.93) * mm});
            skArc(sketch, "E12.3.111", {"start": v(-14.78, 4.1) * mm, "mid": v(-14.26, 3.57) * mm, "end": v(-13.57, 3.26) * mm});
            skArc(sketch, "E12.3.112", {"start": v(-15.76, 6.38) * mm, "mid": v(-15.83, 5.9) * mm, "end": v(-15.67, 5.46) * mm});
            skArc(sketch, "E12.3.113", {"start": v(-16.5, -1.64) * mm, "mid": v(-16.77, -2.05) * mm, "end": v(-16.81, -2.52) * mm});
            skArc(sketch, "E12.3.114", {"start": v(-12.34, 2.01) * mm, "mid": v(-12.5, 2.73) * mm, "end": v(-13.1, 3.15) * mm});
            skArc(sketch, "E12.3.115", {"start": v(-16.5, -1.64) * mm, "mid": v(-16.77, -2.05) * mm, "end": v(-16.81, -2.52) * mm});
            skArc(sketch, "E12.3.116", {"start": v(-13.46, 0) * mm, "mid": v(-12.78, 0.27) * mm, "end": v(-12.47, 0.93) * mm});
            skArc(sketch, "E12.3.117", {"start": v(-14.78, 4.1) * mm, "mid": v(-14.26, 3.57) * mm, "end": v(-13.57, 3.26) * mm});
            skArc(sketch, "E12.3.118", {"start": v(-15.76, 6.38) * mm, "mid": v(-15.83, 5.9) * mm, "end": v(-15.67, 5.46) * mm});
            skArc(sketch, "E12.3.119", {"start": v(-16.5, -1.64) * mm, "mid": v(-16.77, -2.05) * mm, "end": v(-16.81, -2.52) * mm});
            skArc(sketch, "E12.3.120", {"start": v(-13.46, 0) * mm, "mid": v(-12.78, 0.27) * mm, "end": v(-12.47, 0.93) * mm});
            skArc(sketch, "E12.3.121", {"start": v(-12.34, 2.01) * mm, "mid": v(-12.5, 2.73) * mm, "end": v(-13.1, 3.15) * mm});
            skArc(sketch, "E12.3.122", {"start": v(-14.78, 4.1) * mm, "mid": v(-14.26, 3.57) * mm, "end": v(-13.57, 3.26) * mm});
            skArc(sketch, "E12.3.123", {"start": v(-15.76, 6.38) * mm, "mid": v(-15.83, 5.9) * mm, "end": v(-15.67, 5.46) * mm});
            skArc(sketch, "E12.3.124", {"start": v(-16.5, -1.64) * mm, "mid": v(-16.77, -2.05) * mm, "end": v(-16.81, -2.52) * mm});
            skArc(sketch, "E12.3.125", {"start": v(-12.34, 2.01) * mm, "mid": v(-12.5, 2.73) * mm, "end": v(-13.1, 3.15) * mm});
            skArc(sketch, "E12.3.126", {"start": v(-13.46, 0) * mm, "mid": v(-12.78, 0.27) * mm, "end": v(-12.47, 0.93) * mm});
            skArc(sketch, "E12.3.127", {"start": v(-14.78, 4.1) * mm, "mid": v(-14.26, 3.57) * mm, "end": v(-13.57, 3.26) * mm});
            skArc(sketch, "E12.3.128", {"start": v(-15.76, 6.38) * mm, "mid": v(-15.83, 5.9) * mm, "end": v(-15.67, 5.46) * mm});
            skArc(sketch, "E12.3.129", {"start": v(-12.34, 2.01) * mm, "mid": v(-12.5, 2.73) * mm, "end": v(-13.1, 3.15) * mm});
            skArc(sketch, "E12.3.130", {"start": v(-16.5, -1.64) * mm, "mid": v(-16.77, -2.05) * mm, "end": v(-16.81, -2.52) * mm});
            skArc(sketch, "E12.3.131", {"start": v(-13.46, 0) * mm, "mid": v(-12.78, 0.27) * mm, "end": v(-12.47, 0.93) * mm});
            skArc(sketch, "E12.3.132", {"start": v(-15.76, 6.38) * mm, "mid": v(-15.83, 5.9) * mm, "end": v(-15.67, 5.46) * mm});
            skArc(sketch, "E12.3.133", {"start": v(-14.78, 4.1) * mm, "mid": v(-14.26, 3.57) * mm, "end": v(-13.57, 3.26) * mm});
            skArc(sketch, "E12.3.134", {"start": v(-14.78, 4.1) * mm, "mid": v(-14.26, 3.57) * mm, "end": v(-13.57, 3.26) * mm});
            skArc(sketch, "E12.3.135", {"start": v(-15.76, 6.38) * mm, "mid": v(-15.83, 5.9) * mm, "end": v(-15.67, 5.46) * mm});
            skArc(sketch, "E12.3.136", {"start": v(-12.34, 2.01) * mm, "mid": v(-12.5, 2.73) * mm, "end": v(-13.1, 3.15) * mm});
            skArc(sketch, "E12.3.137", {"start": v(-16.5, -1.64) * mm, "mid": v(-16.77, -2.05) * mm, "end": v(-16.81, -2.52) * mm});
            skArc(sketch, "E12.3.138", {"start": v(-13.46, 0) * mm, "mid": v(-12.78, 0.27) * mm, "end": v(-12.47, 0.93) * mm});
            skArc(sketch, "E12.3.139", {"start": v(-12.34, 2.01) * mm, "mid": v(-12.5, 2.73) * mm, "end": v(-13.1, 3.15) * mm});
            skArc(sketch, "E12.3.140", {"start": v(-13.46, 0) * mm, "mid": v(-12.78, 0.27) * mm, "end": v(-12.47, 0.93) * mm});
            skArc(sketch, "E12.3.141", {"start": v(-14.78, 4.1) * mm, "mid": v(-14.26, 3.57) * mm, "end": v(-13.57, 3.26) * mm});
            skArc(sketch, "E12.3.142", {"start": v(-15.76, 6.38) * mm, "mid": v(-15.83, 5.9) * mm, "end": v(-15.67, 5.46) * mm});
            skArc(sketch, "E12.3.143", {"start": v(-16.5, -1.64) * mm, "mid": v(-16.77, -2.05) * mm, "end": v(-16.81, -2.52) * mm});
            skArc(sketch, "E12.3.144", {"start": v(-16.5, -1.64) * mm, "mid": v(-16.77, -2.05) * mm, "end": v(-16.81, -2.52) * mm});
            skArc(sketch, "E12.3.145", {"start": v(-14.78, 4.1) * mm, "mid": v(-14.26, 3.57) * mm, "end": v(-13.57, 3.26) * mm});
            skArc(sketch, "E12.3.146", {"start": v(-12.34, 2.01) * mm, "mid": v(-12.5, 2.73) * mm, "end": v(-13.1, 3.15) * mm});
            skArc(sketch, "E12.3.147", {"start": v(-13.46, 0) * mm, "mid": v(-12.78, 0.27) * mm, "end": v(-12.47, 0.93) * mm});
            skArc(sketch, "E12.3.148", {"start": v(-15.76, 6.38) * mm, "mid": v(-15.83, 5.9) * mm, "end": v(-15.67, 5.46) * mm});
            skArc(sketch, "E12.3.149", {"start": v(-12.34, 2.01) * mm, "mid": v(-12.5, 2.73) * mm, "end": v(-13.1, 3.15) * mm});
            skArc(sketch, "E12.3.150", {"start": v(-16.5, -1.64) * mm, "mid": v(-16.77, -2.05) * mm, "end": v(-16.81, -2.52) * mm});
            skArc(sketch, "E12.3.151", {"start": v(-13.46, 0) * mm, "mid": v(-12.78, 0.27) * mm, "end": v(-12.47, 0.93) * mm});
            skArc(sketch, "E12.3.152", {"start": v(-15.76, 6.38) * mm, "mid": v(-15.83, 5.9) * mm, "end": v(-15.67, 5.46) * mm});
            skArc(sketch, "E12.3.153", {"start": v(-14.78, 4.1) * mm, "mid": v(-14.26, 3.57) * mm, "end": v(-13.57, 3.26) * mm});
            skArc(sketch, "E12.3.154", {"start": v(-16.5, -1.64) * mm, "mid": v(-16.77, -2.05) * mm, "end": v(-16.81, -2.52) * mm});
            skArc(sketch, "E12.3.155", {"start": v(-15.76, 6.38) * mm, "mid": v(-15.83, 5.9) * mm, "end": v(-15.67, 5.46) * mm});
            skArc(sketch, "E12.3.156", {"start": v(-12.34, 2.01) * mm, "mid": v(-12.5, 2.73) * mm, "end": v(-13.1, 3.15) * mm});
            skArc(sketch, "E12.3.157", {"start": v(-14.78, 4.1) * mm, "mid": v(-14.26, 3.57) * mm, "end": v(-13.57, 3.26) * mm});
            skArc(sketch, "E12.3.158", {"start": v(-13.46, 0) * mm, "mid": v(-12.78, 0.27) * mm, "end": v(-12.47, 0.93) * mm});
            skArc(sketch, "E12.3.159", {"start": v(-16.5, -1.64) * mm, "mid": v(-16.77, -2.05) * mm, "end": v(-16.81, -2.52) * mm});
            skArc(sketch, "E12.3.160", {"start": v(-13.46, 0) * mm, "mid": v(-12.78, 0.27) * mm, "end": v(-12.47, 0.93) * mm});
            skArc(sketch, "E12.3.161", {"start": v(-12.34, 2.01) * mm, "mid": v(-12.5, 2.73) * mm, "end": v(-13.1, 3.15) * mm});
            skArc(sketch, "E12.3.162", {"start": v(-14.78, 4.1) * mm, "mid": v(-14.26, 3.57) * mm, "end": v(-13.57, 3.26) * mm});
            skArc(sketch, "E12.3.163", {"start": v(-15.76, 6.38) * mm, "mid": v(-15.83, 5.9) * mm, "end": v(-15.67, 5.46) * mm});
            skArc(sketch, "E12.3.164", {"start": v(-13.96, 0) * mm, "mid": v(-14.7, -0.14) * mm, "end": v(-15.33, -0.54) * mm});
            skArc(sketch, "E12.3.165", {"start": v(-12.34, 2.01) * mm, "mid": v(-12.41, 1.47) * mm, "end": v(-12.47, 0.93) * mm});
            skArc(sketch, "E12.3.166", {"start": v(-15.76, 6.38) * mm, "mid": v(-15.83, 5.9) * mm, "end": v(-15.67, 5.46) * mm});
            skLineSegment(sketch, "E12.3.167", {"start": v(-14.78, 4.1) * mm, "end": v(-15.67, 5.46) * mm});
            skLineSegment(sketch, "E12.3.168", {"start": v(-15.33, -0.54) * mm, "end": v(-16.5, -1.64) * mm});
            skArc(sketch, "E12.3.169", {"start": v(-16.5, -1.64) * mm, "mid": v(-16.77, -2.05) * mm, "end": v(-16.81, -2.52) * mm});
            skLineSegment(sketch, "E12.3.170", {"start": v(-15.33, -0.54) * mm, "end": v(-16.5, -1.64) * mm});
            skLineSegment(sketch, "E12.3.171", {"start": v(-14.78, 4.1) * mm, "end": v(-15.67, 5.46) * mm});
            skLineSegment(sketch, "E12.3.172", {"start": v(-13.1, 3.15) * mm, "end": v(-13.57, 3.26) * mm});
            skArc(sketch, "E12.3.173", {"start": v(-12.34, 2.01) * mm, "mid": v(-12.41, 1.47) * mm, "end": v(-12.47, 0.93) * mm});
            skArc(sketch, "E12.3.174", {"start": v(-13.96, 0) * mm, "mid": v(-14.7, -0.14) * mm, "end": v(-15.33, -0.54) * mm});
            skLineSegment(sketch, "E12.3.175", {"start": v(-14.78, 4.1) * mm, "end": v(-15.67, 5.46) * mm});
            skArc(sketch, "E12.3.176", {"start": v(-13.96, 0) * mm, "mid": v(-14.7, -0.14) * mm, "end": v(-15.33, -0.54) * mm});
            skLineSegment(sketch, "E12.3.177", {"start": v(-15.33, -0.54) * mm, "end": v(-16.5, -1.64) * mm});
            skLineSegment(sketch, "E12.3.178", {"start": v(-13.1, 3.15) * mm, "end": v(-13.57, 3.26) * mm});
            skArc(sketch, "E12.3.179", {"start": v(-12.34, 2.01) * mm, "mid": v(-12.41, 1.47) * mm, "end": v(-12.47, 0.93) * mm});
            skLineSegment(sketch, "E12.3.180", {"start": v(-15.33, -0.54) * mm, "end": v(-16.5, -1.64) * mm});
            skArc(sketch, "E12.3.181", {"start": v(-13.96, 0) * mm, "mid": v(-14.7, -0.14) * mm, "end": v(-15.33, -0.54) * mm});
            skArc(sketch, "E12.3.182", {"start": v(-12.34, 2.01) * mm, "mid": v(-12.41, 1.47) * mm, "end": v(-12.47, 0.93) * mm});
            skLineSegment(sketch, "E12.3.183", {"start": v(-13.1, 3.15) * mm, "end": v(-13.57, 3.26) * mm});
            skLineSegment(sketch, "E12.3.184", {"start": v(-14.78, 4.1) * mm, "end": v(-15.67, 5.46) * mm});
            skArc(sketch, "E12.3.185", {"start": v(-13.96, 0) * mm, "mid": v(-14.7, -0.14) * mm, "end": v(-15.33, -0.54) * mm});
            skLineSegment(sketch, "E12.3.186", {"start": v(-15.33, -0.54) * mm, "end": v(-16.5, -1.64) * mm});
            skLineSegment(sketch, "E12.3.187", {"start": v(-14.78, 4.1) * mm, "end": v(-15.67, 5.46) * mm});
            skArc(sketch, "E12.3.188", {"start": v(-12.34, 2.01) * mm, "mid": v(-12.41, 1.47) * mm, "end": v(-12.47, 0.93) * mm});
            skLineSegment(sketch, "E12.3.189", {"start": v(-13.1, 3.15) * mm, "end": v(-13.57, 3.26) * mm});
            skArc(sketch, "E12.3.190", {"start": v(-13.96, 0) * mm, "mid": v(-14.7, -0.14) * mm, "end": v(-15.33, -0.54) * mm});
            skLineSegment(sketch, "E12.3.191", {"start": v(-14.78, 4.1) * mm, "end": v(-15.67, 5.46) * mm});
            skArc(sketch, "E12.3.192", {"start": v(-12.34, 2.01) * mm, "mid": v(-12.41, 1.47) * mm, "end": v(-12.47, 0.93) * mm});
            skLineSegment(sketch, "E12.3.193", {"start": v(-15.33, -0.54) * mm, "end": v(-16.5, -1.64) * mm});
            skLineSegment(sketch, "E12.3.194", {"start": v(-13.1, 3.15) * mm, "end": v(-13.57, 3.26) * mm});
            skLineSegment(sketch, "E12.3.195", {"start": v(-15.33, -0.54) * mm, "end": v(-16.5, -1.64) * mm});
            skArc(sketch, "E12.3.196", {"start": v(-12.34, 2.01) * mm, "mid": v(-12.41, 1.47) * mm, "end": v(-12.47, 0.93) * mm});
            skLineSegment(sketch, "E12.3.197", {"start": v(-14.78, 4.1) * mm, "end": v(-15.67, 5.46) * mm});
            skArc(sketch, "E12.3.198", {"start": v(-13.96, 0) * mm, "mid": v(-14.7, -0.14) * mm, "end": v(-15.33, -0.54) * mm});
            skLineSegment(sketch, "E12.3.199", {"start": v(-13.1, 3.15) * mm, "end": v(-13.57, 3.26) * mm});
            skLineSegment(sketch, "E12.3.200", {"start": v(-14.78, 4.1) * mm, "end": v(-15.67, 5.46) * mm});
            skArc(sketch, "E12.3.201", {"start": v(-12.34, 2.01) * mm, "mid": v(-12.41, 1.47) * mm, "end": v(-12.47, 0.93) * mm});
            skLineSegment(sketch, "E12.3.202", {"start": v(-13.96, 0) * mm, "end": v(-13.46, 0) * mm});
            skLineSegment(sketch, "E12.3.203", {"start": v(-15.33, -0.54) * mm, "end": v(-16.5, -1.64) * mm});
            skArc(sketch, "E12.3.204", {"start": v(-13.96, 0) * mm, "mid": v(-14.7, -0.14) * mm, "end": v(-15.33, -0.54) * mm});
            skLineSegment(sketch, "E12.3.205", {"start": v(-13.1, 3.15) * mm, "end": v(-13.57, 3.26) * mm});
            skLineSegment(sketch, "E12.3.206", {"start": v(-13.96, 0) * mm, "end": v(-13.46, 0) * mm});
            skLineSegment(sketch, "E12.3.207", {"start": v(-13.1, 3.15) * mm, "end": v(-13.57, 3.26) * mm});
            skArc(sketch, "E12.3.208", {"start": v(-13.96, 0) * mm, "mid": v(-14.7, -0.14) * mm, "end": v(-15.33, -0.54) * mm});
            skLineSegment(sketch, "E12.3.209", {"start": v(-14.78, 4.1) * mm, "end": v(-15.67, 5.46) * mm});
            skArc(sketch, "E12.3.210", {"start": v(-12.34, 2.01) * mm, "mid": v(-12.41, 1.47) * mm, "end": v(-12.47, 0.93) * mm});
            skLineSegment(sketch, "E12.3.211", {"start": v(-15.33, -0.54) * mm, "end": v(-16.5, -1.64) * mm});
            skArc(sketch, "E12.3.212", {"start": v(-12.34, 2.01) * mm, "mid": v(-12.41, 1.47) * mm, "end": v(-12.47, 0.93) * mm});
            skLineSegment(sketch, "E12.3.213", {"start": v(-15.33, -0.54) * mm, "end": v(-16.5, -1.64) * mm});
            skLineSegment(sketch, "E12.3.214", {"start": v(-14.78, 4.1) * mm, "end": v(-15.67, 5.46) * mm});
            skLineSegment(sketch, "E12.3.215", {"start": v(-13.96, 0) * mm, "end": v(-13.46, 0) * mm});
            skArc(sketch, "E12.3.216", {"start": v(-13.96, 0) * mm, "mid": v(-14.7, -0.14) * mm, "end": v(-15.33, -0.54) * mm});
            skLineSegment(sketch, "E12.3.217", {"start": v(-13.1, 3.15) * mm, "end": v(-13.57, 3.26) * mm});
            skLineSegment(sketch, "E12.3.218", {"start": v(-15.33, -0.54) * mm, "end": v(-16.5, -1.64) * mm});
            skArc(sketch, "E12.3.219", {"start": v(-13.96, 0) * mm, "mid": v(-14.7, -0.14) * mm, "end": v(-15.33, -0.54) * mm});
            skLineSegment(sketch, "E12.3.220", {"start": v(-14.78, 4.1) * mm, "end": v(-15.67, 5.46) * mm});
            skLineSegment(sketch, "E12.3.221", {"start": v(-13.1, 3.15) * mm, "end": v(-13.57, 3.26) * mm});
            skArc(sketch, "E12.3.222", {"start": v(-12.34, 2.01) * mm, "mid": v(-12.41, 1.47) * mm, "end": v(-12.47, 0.93) * mm});
            skLineSegment(sketch, "E12.3.223", {"start": v(-13.96, 0) * mm, "end": v(-13.46, 0) * mm});
            skLineSegment(sketch, "E12.3.224", {"start": v(-15.33, -0.54) * mm, "end": v(-16.5, -1.64) * mm});
            skLineSegment(sketch, "E12.3.225", {"start": v(-14.78, 4.1) * mm, "end": v(-15.67, 5.46) * mm});
            skLineSegment(sketch, "E12.3.226", {"start": v(-13.96, 0) * mm, "end": v(-13.46, 0) * mm});
            skArc(sketch, "E12.3.227", {"start": v(-13.96, 0) * mm, "mid": v(-14.7, -0.14) * mm, "end": v(-15.33, -0.54) * mm});
            skLineSegment(sketch, "E12.3.228", {"start": v(-13.1, 3.15) * mm, "end": v(-13.57, 3.26) * mm});
            skArc(sketch, "E12.3.229", {"start": v(-12.34, 2.01) * mm, "mid": v(-12.41, 1.47) * mm, "end": v(-12.47, 0.93) * mm});
            skArc(sketch, "E12.3.230", {"start": v(-12.34, 2.01) * mm, "mid": v(-12.41, 1.47) * mm, "end": v(-12.47, 0.93) * mm});
            skLineSegment(sketch, "E12.3.231", {"start": v(-13.1, 3.15) * mm, "end": v(-13.57, 3.26) * mm});
            skLineSegment(sketch, "E12.3.232", {"start": v(-15.33, -0.54) * mm, "end": v(-16.5, -1.64) * mm});
            skLineSegment(sketch, "E12.3.233", {"start": v(-13.96, 0) * mm, "end": v(-13.46, 0) * mm});
            skArc(sketch, "E12.3.234", {"start": v(-13.96, 0) * mm, "mid": v(-14.7, -0.14) * mm, "end": v(-15.33, -0.54) * mm});
            skLineSegment(sketch, "E12.3.235", {"start": v(-14.78, 4.1) * mm, "end": v(-15.67, 5.46) * mm});
            skLineSegment(sketch, "E12.3.236", {"start": v(-13.1, 3.15) * mm, "end": v(-13.57, 3.26) * mm});
            skLineSegment(sketch, "E12.3.237", {"start": v(-13.96, 0) * mm, "end": v(-13.46, 0) * mm});
            skLineSegment(sketch, "E12.3.238", {"start": v(-13.96, 0) * mm, "end": v(-13.46, 0) * mm});
            skLineSegment(sketch, "E12.3.239", {"start": v(-13.96, 0) * mm, "end": v(-13.46, 0) * mm});
            skLineSegment(sketch, "E12.3.240", {"start": v(-13.96, 0) * mm, "end": v(-13.46, 0) * mm});
            skLineSegment(sketch, "E12.3.241", {"start": v(-13.96, 0) * mm, "end": v(-13.46, 0) * mm});
            skLineSegment(sketch, "E12.3.242", {"start": v(-13.96, 0) * mm, "end": v(-13.46, 0) * mm});
            skLineSegment(sketch, "E12.3.243", {"start": v(-13.96, 0) * mm, "end": v(-13.46, 0) * mm});
            skLineSegment(sketch, "E12.4.0", {"start": v(-13.3, -10.6) * mm, "end": v(0, 0) * mm});
            skPoint(sketch, "E12.4.1", {"position": v(-13.62, -10.17) * mm});
            skPoint(sketch, "E12.4.2", {"position": v(-16.3, -4.82) * mm});
            skLineSegment(sketch, "E12.4.3", {"start": v(-16.84, -2.35) * mm, "end": v(0, 0) * mm});
            skPoint(sketch, "E12.4.4", {"position": v(-14.14, -4.19) * mm});
            skPoint(sketch, "E12.4.6", {"position": v(-16.75, -2.88) * mm});
            skPoint(sketch, "E12.4.7", {"position": v(-10.83, -6.25) * mm});
            skPoint(sketch, "E12.4.8", {"position": v(-14.72, -8.5) * mm});
            skPoint(sketch, "E12.4.9", {"position": v(-12.77, -7.37) * mm});
            skPoint(sketch, "E12.4.10", {"position": v(-11.99, -3.55) * mm});
            skPoint(sketch, "E12.4.11", {"position": v(-16.3, -4.82) * mm});
            skPoint(sketch, "E12.4.12", {"position": v(-16.75, -2.88) * mm});
            skPoint(sketch, "E12.4.13", {"position": v(-11.99, -3.55) * mm});
            skPoint(sketch, "E12.4.14", {"position": v(-10.83, -6.25) * mm});
            skPoint(sketch, "E12.4.15", {"position": v(-14.14, -4.19) * mm});
            skPoint(sketch, "E12.4.16", {"position": v(-13.62, -10.17) * mm});
            skPoint(sketch, "E12.4.17", {"position": v(-12.77, -7.37) * mm});
            skPoint(sketch, "E12.4.18", {"position": v(-14.72, -8.5) * mm});
            skPoint(sketch, "E12.4.19", {"position": v(-16.75, -2.88) * mm});
            skPoint(sketch, "E12.4.20", {"position": v(-16.3, -4.82) * mm});
            skPoint(sketch, "E12.4.21", {"position": v(-11.99, -3.55) * mm});
            skPoint(sketch, "E12.4.22", {"position": v(-12.77, -7.37) * mm});
            skPoint(sketch, "E12.4.23", {"position": v(-14.14, -4.19) * mm});
            skPoint(sketch, "E12.4.24", {"position": v(-10.83, -6.25) * mm});
            skPoint(sketch, "E12.4.25", {"position": v(-14.72, -8.5) * mm});
            skPoint(sketch, "E12.4.26", {"position": v(-13.62, -10.17) * mm});
            skPoint(sketch, "E12.4.27", {"position": v(-16.3, -4.82) * mm});
            skPoint(sketch, "E12.4.28", {"position": v(-14.14, -4.19) * mm});
            skPoint(sketch, "E12.4.29", {"position": v(-14.72, -8.5) * mm});
            skPoint(sketch, "E12.4.30", {"position": v(-13.62, -10.17) * mm});
            skPoint(sketch, "E12.4.31", {"position": v(-16.75, -2.88) * mm});
            skPoint(sketch, "E12.4.32", {"position": v(-10.83, -6.25) * mm});
            skPoint(sketch, "E12.4.33", {"position": v(-12.77, -7.37) * mm});
            skPoint(sketch, "E12.4.34", {"position": v(-11.99, -3.55) * mm});
            skPoint(sketch, "E12.4.35", {"position": v(-10.83, -6.25) * mm});
            skPoint(sketch, "E12.4.36", {"position": v(-13.62, -10.17) * mm});
            skPoint(sketch, "E12.4.37", {"position": v(-16.75, -2.88) * mm});
            skPoint(sketch, "E12.4.38", {"position": v(-16.3, -4.82) * mm});
            skPoint(sketch, "E12.4.39", {"position": v(-14.72, -8.5) * mm});
            skPoint(sketch, "E12.4.40", {"position": v(-14.14, -4.19) * mm});
            skPoint(sketch, "E12.4.41", {"position": v(-12.77, -7.37) * mm});
            skPoint(sketch, "E12.4.42", {"position": v(-11.99, -3.55) * mm});
            skPoint(sketch, "E12.4.43", {"position": v(-11.99, -3.55) * mm});
            skPoint(sketch, "E12.4.44", {"position": v(-16.75, -2.88) * mm});
            skPoint(sketch, "E12.4.45", {"position": v(-13.62, -10.17) * mm});
            skPoint(sketch, "E12.4.46", {"position": v(-16.3, -4.82) * mm});
            skPoint(sketch, "E12.4.47", {"position": v(-14.14, -4.19) * mm});
            skPoint(sketch, "E12.4.48", {"position": v(-10.83, -6.25) * mm});
            skPoint(sketch, "E12.4.49", {"position": v(-12.77, -7.37) * mm});
            skPoint(sketch, "E12.4.50", {"position": v(-14.14, -4.19) * mm});
            skPoint(sketch, "E12.4.51", {"position": v(-16.75, -2.88) * mm});
            skPoint(sketch, "E12.4.52", {"position": v(-12.77, -7.37) * mm});
            skPoint(sketch, "E12.4.53", {"position": v(-10.83, -6.25) * mm});
            skPoint(sketch, "E12.4.54", {"position": v(-11.99, -3.55) * mm});
            skPoint(sketch, "E12.4.55", {"position": v(-14.72, -8.5) * mm});
            skPoint(sketch, "E12.4.56", {"position": v(-16.3, -4.82) * mm});
            skPoint(sketch, "E12.4.57", {"position": v(-13.62, -10.17) * mm});
            skPoint(sketch, "E12.4.58", {"position": v(-16.75, -2.88) * mm});
            skPoint(sketch, "E12.4.59", {"position": v(-12.77, -7.37) * mm});
            skPoint(sketch, "E12.4.60", {"position": v(-13.62, -10.17) * mm});
            skPoint(sketch, "E12.4.61", {"position": v(-14.14, -4.19) * mm});
            skPoint(sketch, "E12.4.62", {"position": v(-11.99, -3.55) * mm});
            skPoint(sketch, "E12.4.63", {"position": v(-10.83, -6.25) * mm});
            skPoint(sketch, "E12.4.64", {"position": v(-16.3, -4.82) * mm});
            skPoint(sketch, "E12.4.65", {"position": v(-14.72, -8.5) * mm});
            skPoint(sketch, "E12.4.66", {"position": v(-12.77, -7.37) * mm});
            skPoint(sketch, "E12.4.67", {"position": v(-10.83, -6.25) * mm});
            skPoint(sketch, "E12.4.68", {"position": v(-14.14, -4.19) * mm});
            skPoint(sketch, "E12.4.69", {"position": v(-11.99, -3.55) * mm});
            skPoint(sketch, "E12.4.70", {"position": v(-13.62, -10.17) * mm});
            skPoint(sketch, "E12.4.71", {"position": v(-14.72, -8.5) * mm});
            skPoint(sketch, "E12.4.72", {"position": v(-16.75, -2.88) * mm});
            skPoint(sketch, "E12.4.73", {"position": v(-16.3, -4.82) * mm});
            skPoint(sketch, "E12.4.74", {"position": v(-14.72, -8.5) * mm});
            skPoint(sketch, "E12.4.75", {"position": v(-10.83, -6.25) * mm});
            skPoint(sketch, "E12.4.76", {"position": v(-16.75, -2.88) * mm});
            skPoint(sketch, "E12.4.77", {"position": v(-12.77, -7.37) * mm});
            skPoint(sketch, "E12.4.78", {"position": v(-13.62, -10.17) * mm});
            skPoint(sketch, "E12.4.79", {"position": v(-14.14, -4.19) * mm});
            skPoint(sketch, "E12.4.80", {"position": v(-16.3, -4.82) * mm});
            skPoint(sketch, "E12.4.81", {"position": v(-11.99, -3.55) * mm});
            skPoint(sketch, "E12.4.82", {"position": v(-14.72, -8.5) * mm});
            skPoint(sketch, "E12.4.83", {"position": v(-16.75, -2.88) * mm});
            skPoint(sketch, "E12.4.84", {"position": v(-13.62, -10.17) * mm});
            skPoint(sketch, "E12.4.85", {"position": v(-11.99, -3.55) * mm});
            skPoint(sketch, "E12.4.86", {"position": v(-12.77, -7.37) * mm});
            skPoint(sketch, "E12.4.87", {"position": v(-14.14, -4.19) * mm});
            skPoint(sketch, "E12.4.88", {"position": v(-10.83, -6.25) * mm});
            skPoint(sketch, "E12.4.89", {"position": v(-13.62, -10.17) * mm});
            skPoint(sketch, "E12.4.90", {"position": v(-10.83, -6.25) * mm});
            skPoint(sketch, "E12.4.91", {"position": v(-11.99, -3.55) * mm});
            skPoint(sketch, "E12.4.92", {"position": v(-12.77, -7.38) * mm});
            skPoint(sketch, "E12.4.93", {"position": v(-14.14, -4.19) * mm});
            skPoint(sketch, "E12.4.94", {"position": v(-16.75, -2.88) * mm});
            skPoint(sketch, "E12.4.95", {"position": v(-14.14, -4.19) * mm});
            skPoint(sketch, "E12.4.96", {"position": v(-11.99, -3.55) * mm});
            skPoint(sketch, "E12.4.97", {"position": v(-12.77, -7.37) * mm});
            skPoint(sketch, "E12.4.98", {"position": v(-10.83, -6.25) * mm});
            skPoint(sketch, "E12.4.99", {"position": v(-13.62, -10.17) * mm});
            skPoint(sketch, "E12.4.100", {"position": v(-16.75, -2.88) * mm});
            skArc(sketch, "E12.4.101", {"start": v(-14.85, -3.83) * mm, "mid": v(-14.13, -4.04) * mm, "end": v(-13.39, -3.96) * mm});
            skArc(sketch, "E12.4.102", {"start": v(-11.7, -4.43) * mm, "mid": v(-12.18, -3.88) * mm, "end": v(-12.9, -3.82) * mm});
            skArc(sketch, "E12.4.103", {"start": v(-11.66, -6.73) * mm, "mid": v(-11.2, -6.16) * mm, "end": v(-11.26, -5.43) * mm});
            skArc(sketch, "E12.4.104", {"start": v(-14.85, -3.83) * mm, "mid": v(-14.13, -4.04) * mm, "end": v(-13.39, -3.96) * mm});
            skArc(sketch, "E12.4.105", {"start": v(-16.84, -2.35) * mm, "mid": v(-16.66, -2.8) * mm, "end": v(-16.3, -3.1) * mm});
            skArc(sketch, "E12.4.106", {"start": v(-11.7, -4.43) * mm, "mid": v(-12.18, -3.88) * mm, "end": v(-12.9, -3.82) * mm});
            skArc(sketch, "E12.4.107", {"start": v(-11.66, -6.73) * mm, "mid": v(-11.2, -6.16) * mm, "end": v(-11.26, -5.43) * mm});
            skArc(sketch, "E12.4.108", {"start": v(-13.47, -9.68) * mm, "mid": v(-13.5, -10.16) * mm, "end": v(-13.3, -10.6) * mm});
            skArc(sketch, "E12.4.109", {"start": v(-11.7, -4.43) * mm, "mid": v(-12.18, -3.88) * mm, "end": v(-12.9, -3.82) * mm});
            skArc(sketch, "E12.4.110", {"start": v(-11.66, -6.73) * mm, "mid": v(-11.2, -6.16) * mm, "end": v(-11.26, -5.43) * mm});
            skArc(sketch, "E12.4.111", {"start": v(-14.85, -3.83) * mm, "mid": v(-14.13, -4.04) * mm, "end": v(-13.39, -3.96) * mm});
            skArc(sketch, "E12.4.112", {"start": v(-16.84, -2.35) * mm, "mid": v(-16.66, -2.8) * mm, "end": v(-16.3, -3.1) * mm});
            skArc(sketch, "E12.4.113", {"start": v(-13.47, -9.68) * mm, "mid": v(-13.5, -10.16) * mm, "end": v(-13.3, -10.6) * mm});
            skArc(sketch, "E12.4.114", {"start": v(-11.7, -4.43) * mm, "mid": v(-12.18, -3.88) * mm, "end": v(-12.9, -3.82) * mm});
            skArc(sketch, "E12.4.115", {"start": v(-13.47, -9.68) * mm, "mid": v(-13.5, -10.16) * mm, "end": v(-13.3, -10.6) * mm});
            skArc(sketch, "E12.4.116", {"start": v(-11.66, -6.73) * mm, "mid": v(-11.2, -6.16) * mm, "end": v(-11.26, -5.43) * mm});
            skArc(sketch, "E12.4.117", {"start": v(-14.85, -3.83) * mm, "mid": v(-14.13, -4.04) * mm, "end": v(-13.39, -3.96) * mm});
            skArc(sketch, "E12.4.118", {"start": v(-16.84, -2.35) * mm, "mid": v(-16.66, -2.8) * mm, "end": v(-16.3, -3.1) * mm});
            skArc(sketch, "E12.4.119", {"start": v(-13.47, -9.68) * mm, "mid": v(-13.5, -10.16) * mm, "end": v(-13.3, -10.6) * mm});
            skArc(sketch, "E12.4.120", {"start": v(-11.66, -6.73) * mm, "mid": v(-11.2, -6.16) * mm, "end": v(-11.26, -5.43) * mm});
            skArc(sketch, "E12.4.121", {"start": v(-11.7, -4.43) * mm, "mid": v(-12.18, -3.88) * mm, "end": v(-12.9, -3.82) * mm});
            skArc(sketch, "E12.4.122", {"start": v(-14.85, -3.83) * mm, "mid": v(-14.13, -4.04) * mm, "end": v(-13.39, -3.96) * mm});
            skArc(sketch, "E12.4.123", {"start": v(-16.84, -2.35) * mm, "mid": v(-16.66, -2.8) * mm, "end": v(-16.3, -3.1) * mm});
            skArc(sketch, "E12.4.124", {"start": v(-13.47, -9.68) * mm, "mid": v(-13.5, -10.16) * mm, "end": v(-13.3, -10.6) * mm});
            skArc(sketch, "E12.4.125", {"start": v(-11.7, -4.43) * mm, "mid": v(-12.18, -3.88) * mm, "end": v(-12.9, -3.82) * mm});
            skArc(sketch, "E12.4.126", {"start": v(-11.66, -6.73) * mm, "mid": v(-11.2, -6.16) * mm, "end": v(-11.26, -5.43) * mm});
            skArc(sketch, "E12.4.127", {"start": v(-14.85, -3.83) * mm, "mid": v(-14.13, -4.04) * mm, "end": v(-13.39, -3.96) * mm});
            skArc(sketch, "E12.4.128", {"start": v(-16.84, -2.35) * mm, "mid": v(-16.66, -2.8) * mm, "end": v(-16.3, -3.1) * mm});
            skArc(sketch, "E12.4.129", {"start": v(-11.7, -4.43) * mm, "mid": v(-12.18, -3.88) * mm, "end": v(-12.9, -3.82) * mm});
            skArc(sketch, "E12.4.130", {"start": v(-13.47, -9.68) * mm, "mid": v(-13.5, -10.16) * mm, "end": v(-13.3, -10.6) * mm});
            skArc(sketch, "E12.4.131", {"start": v(-11.66, -6.73) * mm, "mid": v(-11.2, -6.16) * mm, "end": v(-11.26, -5.43) * mm});
            skArc(sketch, "E12.4.132", {"start": v(-16.84, -2.35) * mm, "mid": v(-16.66, -2.8) * mm, "end": v(-16.3, -3.1) * mm});
            skArc(sketch, "E12.4.133", {"start": v(-14.85, -3.83) * mm, "mid": v(-14.13, -4.04) * mm, "end": v(-13.39, -3.96) * mm});
            skArc(sketch, "E12.4.134", {"start": v(-14.85, -3.83) * mm, "mid": v(-14.13, -4.04) * mm, "end": v(-13.39, -3.96) * mm});
            skArc(sketch, "E12.4.135", {"start": v(-16.84, -2.35) * mm, "mid": v(-16.66, -2.8) * mm, "end": v(-16.3, -3.1) * mm});
            skArc(sketch, "E12.4.136", {"start": v(-11.7, -4.43) * mm, "mid": v(-12.18, -3.88) * mm, "end": v(-12.9, -3.82) * mm});
            skArc(sketch, "E12.4.137", {"start": v(-13.47, -9.68) * mm, "mid": v(-13.5, -10.16) * mm, "end": v(-13.3, -10.6) * mm});
            skArc(sketch, "E12.4.138", {"start": v(-11.66, -6.73) * mm, "mid": v(-11.2, -6.16) * mm, "end": v(-11.26, -5.43) * mm});
            skArc(sketch, "E12.4.139", {"start": v(-11.7, -4.43) * mm, "mid": v(-12.18, -3.88) * mm, "end": v(-12.9, -3.82) * mm});
            skArc(sketch, "E12.4.140", {"start": v(-11.66, -6.73) * mm, "mid": v(-11.2, -6.16) * mm, "end": v(-11.26, -5.43) * mm});
            skArc(sketch, "E12.4.141", {"start": v(-14.85, -3.83) * mm, "mid": v(-14.13, -4.04) * mm, "end": v(-13.39, -3.96) * mm});
            skArc(sketch, "E12.4.142", {"start": v(-16.84, -2.35) * mm, "mid": v(-16.66, -2.8) * mm, "end": v(-16.3, -3.1) * mm});
            skArc(sketch, "E12.4.143", {"start": v(-13.47, -9.68) * mm, "mid": v(-13.5, -10.16) * mm, "end": v(-13.3, -10.6) * mm});
            skArc(sketch, "E12.4.144", {"start": v(-13.47, -9.68) * mm, "mid": v(-13.5, -10.16) * mm, "end": v(-13.3, -10.6) * mm});
            skArc(sketch, "E12.4.145", {"start": v(-14.85, -3.83) * mm, "mid": v(-14.13, -4.04) * mm, "end": v(-13.39, -3.96) * mm});
            skArc(sketch, "E12.4.146", {"start": v(-11.7, -4.43) * mm, "mid": v(-12.18, -3.88) * mm, "end": v(-12.9, -3.82) * mm});
            skArc(sketch, "E12.4.147", {"start": v(-11.66, -6.73) * mm, "mid": v(-11.2, -6.16) * mm, "end": v(-11.26, -5.43) * mm});
            skArc(sketch, "E12.4.148", {"start": v(-16.84, -2.35) * mm, "mid": v(-16.66, -2.8) * mm, "end": v(-16.3, -3.1) * mm});
            skArc(sketch, "E12.4.149", {"start": v(-11.7, -4.43) * mm, "mid": v(-12.18, -3.88) * mm, "end": v(-12.9, -3.82) * mm});
            skArc(sketch, "E12.4.150", {"start": v(-13.47, -9.68) * mm, "mid": v(-13.5, -10.16) * mm, "end": v(-13.3, -10.6) * mm});
            skArc(sketch, "E12.4.151", {"start": v(-11.66, -6.73) * mm, "mid": v(-11.2, -6.16) * mm, "end": v(-11.26, -5.43) * mm});
            skArc(sketch, "E12.4.152", {"start": v(-16.84, -2.35) * mm, "mid": v(-16.66, -2.8) * mm, "end": v(-16.3, -3.1) * mm});
            skArc(sketch, "E12.4.153", {"start": v(-14.85, -3.83) * mm, "mid": v(-14.13, -4.04) * mm, "end": v(-13.39, -3.96) * mm});
            skArc(sketch, "E12.4.154", {"start": v(-13.47, -9.68) * mm, "mid": v(-13.5, -10.16) * mm, "end": v(-13.3, -10.6) * mm});
            skArc(sketch, "E12.4.155", {"start": v(-16.84, -2.35) * mm, "mid": v(-16.66, -2.8) * mm, "end": v(-16.3, -3.1) * mm});
            skArc(sketch, "E12.4.156", {"start": v(-11.7, -4.43) * mm, "mid": v(-12.18, -3.88) * mm, "end": v(-12.9, -3.82) * mm});
            skArc(sketch, "E12.4.157", {"start": v(-14.85, -3.83) * mm, "mid": v(-14.13, -4.04) * mm, "end": v(-13.39, -3.96) * mm});
            skArc(sketch, "E12.4.158", {"start": v(-11.66, -6.73) * mm, "mid": v(-11.2, -6.16) * mm, "end": v(-11.26, -5.43) * mm});
            skArc(sketch, "E12.4.159", {"start": v(-13.47, -9.68) * mm, "mid": v(-13.5, -10.16) * mm, "end": v(-13.3, -10.6) * mm});
            skArc(sketch, "E12.4.160", {"start": v(-11.66, -6.73) * mm, "mid": v(-11.2, -6.16) * mm, "end": v(-11.26, -5.43) * mm});
            skArc(sketch, "E12.4.161", {"start": v(-11.7, -4.43) * mm, "mid": v(-12.18, -3.88) * mm, "end": v(-12.9, -3.82) * mm});
            skArc(sketch, "E12.4.162", {"start": v(-14.85, -3.83) * mm, "mid": v(-14.13, -4.04) * mm, "end": v(-13.39, -3.96) * mm});
            skArc(sketch, "E12.4.163", {"start": v(-16.84, -2.35) * mm, "mid": v(-16.66, -2.8) * mm, "end": v(-16.3, -3.1) * mm});
            skArc(sketch, "E12.4.164", {"start": v(-12.09, -6.98) * mm, "mid": v(-12.66, -7.47) * mm, "end": v(-13, -8.13) * mm});
            skArc(sketch, "E12.4.165", {"start": v(-11.7, -4.43) * mm, "mid": v(-11.49, -4.93) * mm, "end": v(-11.26, -5.43) * mm});
            skArc(sketch, "E12.4.166", {"start": v(-16.84, -2.35) * mm, "mid": v(-16.66, -2.8) * mm, "end": v(-16.3, -3.1) * mm});
            skLineSegment(sketch, "E12.4.167", {"start": v(-14.85, -3.83) * mm, "end": v(-16.3, -3.1) * mm});
            skLineSegment(sketch, "E12.4.168", {"start": v(-13, -8.13) * mm, "end": v(-13.47, -9.68) * mm});
            skArc(sketch, "E12.4.169", {"start": v(-13.47, -9.68) * mm, "mid": v(-13.5, -10.16) * mm, "end": v(-13.3, -10.6) * mm});
            skLineSegment(sketch, "E12.4.170", {"start": v(-13, -8.13) * mm, "end": v(-13.47, -9.68) * mm});
            skLineSegment(sketch, "E12.4.171", {"start": v(-14.85, -3.83) * mm, "end": v(-16.3, -3.1) * mm});
            skLineSegment(sketch, "E12.4.172", {"start": v(-12.9, -3.82) * mm, "end": v(-13.39, -3.96) * mm});
            skArc(sketch, "E12.4.173", {"start": v(-11.7, -4.43) * mm, "mid": v(-11.49, -4.93) * mm, "end": v(-11.26, -5.43) * mm});
            skArc(sketch, "E12.4.174", {"start": v(-12.09, -6.98) * mm, "mid": v(-12.66, -7.47) * mm, "end": v(-13, -8.13) * mm});
            skLineSegment(sketch, "E12.4.175", {"start": v(-14.85, -3.83) * mm, "end": v(-16.3, -3.1) * mm});
            skArc(sketch, "E12.4.176", {"start": v(-12.09, -6.98) * mm, "mid": v(-12.66, -7.47) * mm, "end": v(-13, -8.13) * mm});
            skLineSegment(sketch, "E12.4.177", {"start": v(-13, -8.13) * mm, "end": v(-13.47, -9.68) * mm});
            skLineSegment(sketch, "E12.4.178", {"start": v(-12.9, -3.82) * mm, "end": v(-13.39, -3.96) * mm});
            skArc(sketch, "E12.4.179", {"start": v(-11.7, -4.43) * mm, "mid": v(-11.49, -4.93) * mm, "end": v(-11.26, -5.43) * mm});
            skLineSegment(sketch, "E12.4.180", {"start": v(-13, -8.13) * mm, "end": v(-13.47, -9.68) * mm});
            skArc(sketch, "E12.4.181", {"start": v(-12.09, -6.98) * mm, "mid": v(-12.66, -7.47) * mm, "end": v(-13, -8.13) * mm});
            skArc(sketch, "E12.4.182", {"start": v(-11.7, -4.43) * mm, "mid": v(-11.49, -4.93) * mm, "end": v(-11.26, -5.43) * mm});
            skLineSegment(sketch, "E12.4.183", {"start": v(-12.9, -3.82) * mm, "end": v(-13.39, -3.96) * mm});
            skLineSegment(sketch, "E12.4.184", {"start": v(-14.85, -3.83) * mm, "end": v(-16.3, -3.1) * mm});
            skArc(sketch, "E12.4.185", {"start": v(-12.09, -6.98) * mm, "mid": v(-12.66, -7.47) * mm, "end": v(-13, -8.13) * mm});
            skLineSegment(sketch, "E12.4.186", {"start": v(-13, -8.13) * mm, "end": v(-13.47, -9.68) * mm});
            skLineSegment(sketch, "E12.4.187", {"start": v(-14.85, -3.83) * mm, "end": v(-16.3, -3.1) * mm});
            skArc(sketch, "E12.4.188", {"start": v(-11.7, -4.43) * mm, "mid": v(-11.49, -4.93) * mm, "end": v(-11.26, -5.43) * mm});
            skLineSegment(sketch, "E12.4.189", {"start": v(-12.9, -3.82) * mm, "end": v(-13.39, -3.96) * mm});
            skArc(sketch, "E12.4.190", {"start": v(-12.09, -6.98) * mm, "mid": v(-12.66, -7.47) * mm, "end": v(-13, -8.13) * mm});
            skLineSegment(sketch, "E12.4.191", {"start": v(-14.85, -3.83) * mm, "end": v(-16.3, -3.1) * mm});
            skArc(sketch, "E12.4.192", {"start": v(-11.7, -4.43) * mm, "mid": v(-11.49, -4.93) * mm, "end": v(-11.26, -5.43) * mm});
            skLineSegment(sketch, "E12.4.193", {"start": v(-13, -8.13) * mm, "end": v(-13.47, -9.68) * mm});
            skLineSegment(sketch, "E12.4.194", {"start": v(-12.9, -3.82) * mm, "end": v(-13.39, -3.96) * mm});
            skLineSegment(sketch, "E12.4.195", {"start": v(-13, -8.13) * mm, "end": v(-13.47, -9.68) * mm});
            skArc(sketch, "E12.4.196", {"start": v(-11.7, -4.43) * mm, "mid": v(-11.49, -4.93) * mm, "end": v(-11.26, -5.43) * mm});
            skLineSegment(sketch, "E12.4.197", {"start": v(-14.85, -3.83) * mm, "end": v(-16.3, -3.1) * mm});
            skArc(sketch, "E12.4.198", {"start": v(-12.09, -6.98) * mm, "mid": v(-12.66, -7.47) * mm, "end": v(-13, -8.13) * mm});
            skLineSegment(sketch, "E12.4.199", {"start": v(-12.9, -3.82) * mm, "end": v(-13.39, -3.96) * mm});
            skLineSegment(sketch, "E12.4.200", {"start": v(-14.85, -3.83) * mm, "end": v(-16.3, -3.1) * mm});
            skArc(sketch, "E12.4.201", {"start": v(-11.7, -4.43) * mm, "mid": v(-11.49, -4.93) * mm, "end": v(-11.26, -5.43) * mm});
            skLineSegment(sketch, "E12.4.202", {"start": v(-12.09, -6.98) * mm, "end": v(-11.66, -6.73) * mm});
            skLineSegment(sketch, "E12.4.203", {"start": v(-13, -8.13) * mm, "end": v(-13.47, -9.68) * mm});
            skArc(sketch, "E12.4.204", {"start": v(-12.09, -6.98) * mm, "mid": v(-12.66, -7.47) * mm, "end": v(-13, -8.13) * mm});
            skLineSegment(sketch, "E12.4.205", {"start": v(-12.9, -3.82) * mm, "end": v(-13.39, -3.96) * mm});
            skLineSegment(sketch, "E12.4.206", {"start": v(-12.09, -6.98) * mm, "end": v(-11.66, -6.73) * mm});
            skLineSegment(sketch, "E12.4.207", {"start": v(-12.9, -3.82) * mm, "end": v(-13.39, -3.96) * mm});
            skArc(sketch, "E12.4.208", {"start": v(-12.09, -6.98) * mm, "mid": v(-12.66, -7.47) * mm, "end": v(-13, -8.13) * mm});
            skLineSegment(sketch, "E12.4.209", {"start": v(-14.85, -3.83) * mm, "end": v(-16.3, -3.1) * mm});
            skArc(sketch, "E12.4.210", {"start": v(-11.7, -4.43) * mm, "mid": v(-11.49, -4.93) * mm, "end": v(-11.26, -5.43) * mm});
            skLineSegment(sketch, "E12.4.211", {"start": v(-13, -8.13) * mm, "end": v(-13.47, -9.68) * mm});
            skArc(sketch, "E12.4.212", {"start": v(-11.7, -4.43) * mm, "mid": v(-11.49, -4.93) * mm, "end": v(-11.26, -5.43) * mm});
            skLineSegment(sketch, "E12.4.213", {"start": v(-13, -8.13) * mm, "end": v(-13.47, -9.68) * mm});
            skLineSegment(sketch, "E12.4.214", {"start": v(-14.85, -3.83) * mm, "end": v(-16.3, -3.1) * mm});
            skLineSegment(sketch, "E12.4.215", {"start": v(-12.09, -6.98) * mm, "end": v(-11.66, -6.73) * mm});
            skArc(sketch, "E12.4.216", {"start": v(-12.09, -6.98) * mm, "mid": v(-12.66, -7.47) * mm, "end": v(-13, -8.13) * mm});
            skLineSegment(sketch, "E12.4.217", {"start": v(-12.9, -3.82) * mm, "end": v(-13.39, -3.96) * mm});
            skLineSegment(sketch, "E12.4.218", {"start": v(-13, -8.13) * mm, "end": v(-13.47, -9.68) * mm});
            skArc(sketch, "E12.4.219", {"start": v(-12.09, -6.98) * mm, "mid": v(-12.66, -7.47) * mm, "end": v(-13, -8.13) * mm});
            skLineSegment(sketch, "E12.4.220", {"start": v(-14.85, -3.83) * mm, "end": v(-16.3, -3.1) * mm});
            skLineSegment(sketch, "E12.4.221", {"start": v(-12.9, -3.82) * mm, "end": v(-13.39, -3.96) * mm});
            skArc(sketch, "E12.4.222", {"start": v(-11.7, -4.43) * mm, "mid": v(-11.49, -4.93) * mm, "end": v(-11.26, -5.43) * mm});
            skLineSegment(sketch, "E12.4.223", {"start": v(-12.09, -6.98) * mm, "end": v(-11.66, -6.73) * mm});
            skLineSegment(sketch, "E12.4.224", {"start": v(-13, -8.13) * mm, "end": v(-13.47, -9.68) * mm});
            skLineSegment(sketch, "E12.4.225", {"start": v(-14.85, -3.83) * mm, "end": v(-16.3, -3.1) * mm});
            skLineSegment(sketch, "E12.4.226", {"start": v(-12.09, -6.98) * mm, "end": v(-11.66, -6.73) * mm});
            skArc(sketch, "E12.4.227", {"start": v(-12.09, -6.98) * mm, "mid": v(-12.66, -7.47) * mm, "end": v(-13, -8.13) * mm});
            skLineSegment(sketch, "E12.4.228", {"start": v(-12.9, -3.82) * mm, "end": v(-13.39, -3.96) * mm});
            skArc(sketch, "E12.4.229", {"start": v(-11.7, -4.43) * mm, "mid": v(-11.49, -4.93) * mm, "end": v(-11.26, -5.43) * mm});
            skArc(sketch, "E12.4.230", {"start": v(-11.7, -4.43) * mm, "mid": v(-11.49, -4.93) * mm, "end": v(-11.26, -5.43) * mm});
            skLineSegment(sketch, "E12.4.231", {"start": v(-12.9, -3.82) * mm, "end": v(-13.39, -3.96) * mm});
            skLineSegment(sketch, "E12.4.232", {"start": v(-13, -8.13) * mm, "end": v(-13.47, -9.68) * mm});
            skLineSegment(sketch, "E12.4.233", {"start": v(-12.09, -6.98) * mm, "end": v(-11.66, -6.73) * mm});
            skArc(sketch, "E12.4.234", {"start": v(-12.09, -6.98) * mm, "mid": v(-12.66, -7.47) * mm, "end": v(-13, -8.13) * mm});
            skLineSegment(sketch, "E12.4.235", {"start": v(-14.85, -3.83) * mm, "end": v(-16.3, -3.1) * mm});
            skLineSegment(sketch, "E12.4.236", {"start": v(-12.9, -3.82) * mm, "end": v(-13.39, -3.96) * mm});
            skLineSegment(sketch, "E12.4.237", {"start": v(-12.09, -6.98) * mm, "end": v(-11.66, -6.73) * mm});
            skLineSegment(sketch, "E12.4.238", {"start": v(-12.09, -6.98) * mm, "end": v(-11.66, -6.73) * mm});
            skLineSegment(sketch, "E12.4.239", {"start": v(-12.09, -6.98) * mm, "end": v(-11.66, -6.73) * mm});
            skLineSegment(sketch, "E12.4.240", {"start": v(-12.09, -6.98) * mm, "end": v(-11.66, -6.73) * mm});
            skLineSegment(sketch, "E12.4.241", {"start": v(-12.09, -6.98) * mm, "end": v(-11.66, -6.73) * mm});
            skLineSegment(sketch, "E12.4.242", {"start": v(-12.09, -6.98) * mm, "end": v(-11.66, -6.73) * mm});
            skLineSegment(sketch, "E12.4.243", {"start": v(-12.09, -6.98) * mm, "end": v(-11.66, -6.73) * mm});
            skLineSegment(sketch, "E12.5.0", {"start": v(-6.22, -15.82) * mm, "end": v(0, 0) * mm});
            skPoint(sketch, "E12.5.1", {"position": v(-6.71, -15.62) * mm});
            skPoint(sketch, "E12.5.2", {"position": v(-11.7, -12.33) * mm});
            skLineSegment(sketch, "E12.5.3", {"start": v(-13.4, -10.46) * mm, "end": v(0, 0) * mm});
            skPoint(sketch, "E12.5.4", {"position": v(-10.16, -10.7) * mm});
            skPoint(sketch, "E12.5.6", {"position": v(-13.07, -10.87) * mm});
            skPoint(sketch, "E12.5.7", {"position": v(-6.25, -10.83) * mm});
            skPoint(sketch, "E12.5.8", {"position": v(-8.5, -14.72) * mm});
            skPoint(sketch, "E12.5.9", {"position": v(-7.37, -12.77) * mm});
            skPoint(sketch, "E12.5.10", {"position": v(-8.6, -9.07) * mm});
            skPoint(sketch, "E12.5.11", {"position": v(-11.7, -12.33) * mm});
            skPoint(sketch, "E12.5.12", {"position": v(-13.07, -10.87) * mm});
            skPoint(sketch, "E12.5.13", {"position": v(-8.6, -9.07) * mm});
            skPoint(sketch, "E12.5.14", {"position": v(-6.25, -10.83) * mm});
            skPoint(sketch, "E12.5.15", {"position": v(-10.16, -10.7) * mm});
            skPoint(sketch, "E12.5.16", {"position": v(-6.71, -15.62) * mm});
            skPoint(sketch, "E12.5.17", {"position": v(-7.37, -12.77) * mm});
            skPoint(sketch, "E12.5.18", {"position": v(-8.5, -14.72) * mm});
            skPoint(sketch, "E12.5.19", {"position": v(-13.07, -10.87) * mm});
            skPoint(sketch, "E12.5.20", {"position": v(-11.7, -12.33) * mm});
            skPoint(sketch, "E12.5.21", {"position": v(-8.6, -9.07) * mm});
            skPoint(sketch, "E12.5.22", {"position": v(-7.37, -12.77) * mm});
            skPoint(sketch, "E12.5.23", {"position": v(-10.16, -10.7) * mm});
            skPoint(sketch, "E12.5.24", {"position": v(-6.25, -10.83) * mm});
            skPoint(sketch, "E12.5.25", {"position": v(-8.5, -14.72) * mm});
            skPoint(sketch, "E12.5.26", {"position": v(-6.71, -15.62) * mm});
            skPoint(sketch, "E12.5.27", {"position": v(-11.7, -12.33) * mm});
            skPoint(sketch, "E12.5.28", {"position": v(-10.16, -10.7) * mm});
            skPoint(sketch, "E12.5.29", {"position": v(-8.5, -14.72) * mm});
            skPoint(sketch, "E12.5.30", {"position": v(-6.71, -15.62) * mm});
            skPoint(sketch, "E12.5.31", {"position": v(-13.07, -10.87) * mm});
            skPoint(sketch, "E12.5.32", {"position": v(-6.25, -10.83) * mm});
            skPoint(sketch, "E12.5.33", {"position": v(-7.37, -12.77) * mm});
            skPoint(sketch, "E12.5.34", {"position": v(-8.6, -9.07) * mm});
            skPoint(sketch, "E12.5.35", {"position": v(-6.25, -10.83) * mm});
            skPoint(sketch, "E12.5.36", {"position": v(-6.71, -15.62) * mm});
            skPoint(sketch, "E12.5.37", {"position": v(-13.07, -10.87) * mm});
            skPoint(sketch, "E12.5.38", {"position": v(-11.7, -12.33) * mm});
            skPoint(sketch, "E12.5.39", {"position": v(-8.5, -14.72) * mm});
            skPoint(sketch, "E12.5.40", {"position": v(-10.16, -10.7) * mm});
            skPoint(sketch, "E12.5.41", {"position": v(-7.37, -12.77) * mm});
            skPoint(sketch, "E12.5.42", {"position": v(-8.6, -9.07) * mm});
            skPoint(sketch, "E12.5.43", {"position": v(-8.6, -9.07) * mm});
            skPoint(sketch, "E12.5.44", {"position": v(-13.07, -10.87) * mm});
            skPoint(sketch, "E12.5.45", {"position": v(-6.71, -15.62) * mm});
            skPoint(sketch, "E12.5.46", {"position": v(-11.7, -12.33) * mm});
            skPoint(sketch, "E12.5.47", {"position": v(-10.16, -10.7) * mm});
            skPoint(sketch, "E12.5.48", {"position": v(-6.25, -10.83) * mm});
            skPoint(sketch, "E12.5.49", {"position": v(-7.37, -12.77) * mm});
            skPoint(sketch, "E12.5.50", {"position": v(-10.16, -10.7) * mm});
            skPoint(sketch, "E12.5.51", {"position": v(-13.07, -10.87) * mm});
            skPoint(sketch, "E12.5.52", {"position": v(-7.37, -12.77) * mm});
            skPoint(sketch, "E12.5.53", {"position": v(-6.25, -10.83) * mm});
            skPoint(sketch, "E12.5.54", {"position": v(-8.6, -9.07) * mm});
            skPoint(sketch, "E12.5.55", {"position": v(-8.5, -14.72) * mm});
            skPoint(sketch, "E12.5.56", {"position": v(-11.7, -12.33) * mm});
            skPoint(sketch, "E12.5.57", {"position": v(-6.71, -15.62) * mm});
            skPoint(sketch, "E12.5.58", {"position": v(-13.07, -10.87) * mm});
            skPoint(sketch, "E12.5.59", {"position": v(-7.37, -12.77) * mm});
            skPoint(sketch, "E12.5.60", {"position": v(-6.71, -15.62) * mm});
            skPoint(sketch, "E12.5.61", {"position": v(-10.16, -10.7) * mm});
            skPoint(sketch, "E12.5.62", {"position": v(-8.6, -9.07) * mm});
            skPoint(sketch, "E12.5.63", {"position": v(-6.25, -10.83) * mm});
            skPoint(sketch, "E12.5.64", {"position": v(-11.7, -12.33) * mm});
            skPoint(sketch, "E12.5.65", {"position": v(-8.5, -14.72) * mm});
            skPoint(sketch, "E12.5.66", {"position": v(-7.37, -12.77) * mm});
            skPoint(sketch, "E12.5.67", {"position": v(-6.25, -10.83) * mm});
            skPoint(sketch, "E12.5.68", {"position": v(-10.16, -10.7) * mm});
            skPoint(sketch, "E12.5.69", {"position": v(-8.6, -9.07) * mm});
            skPoint(sketch, "E12.5.70", {"position": v(-6.71, -15.62) * mm});
            skPoint(sketch, "E12.5.71", {"position": v(-8.5, -14.72) * mm});
            skPoint(sketch, "E12.5.72", {"position": v(-13.07, -10.87) * mm});
            skPoint(sketch, "E12.5.73", {"position": v(-11.7, -12.33) * mm});
            skPoint(sketch, "E12.5.74", {"position": v(-8.5, -14.72) * mm});
            skPoint(sketch, "E12.5.75", {"position": v(-6.25, -10.83) * mm});
            skPoint(sketch, "E12.5.76", {"position": v(-13.07, -10.87) * mm});
            skPoint(sketch, "E12.5.77", {"position": v(-7.37, -12.77) * mm});
            skPoint(sketch, "E12.5.78", {"position": v(-6.71, -15.62) * mm});
            skPoint(sketch, "E12.5.79", {"position": v(-10.16, -10.7) * mm});
            skPoint(sketch, "E12.5.80", {"position": v(-11.7, -12.33) * mm});
            skPoint(sketch, "E12.5.81", {"position": v(-8.6, -9.07) * mm});
            skPoint(sketch, "E12.5.82", {"position": v(-8.5, -14.72) * mm});
            skPoint(sketch, "E12.5.83", {"position": v(-13.07, -10.87) * mm});
            skPoint(sketch, "E12.5.84", {"position": v(-6.71, -15.62) * mm});
            skPoint(sketch, "E12.5.85", {"position": v(-8.6, -9.07) * mm});
            skPoint(sketch, "E12.5.86", {"position": v(-7.37, -12.77) * mm});
            skPoint(sketch, "E12.5.87", {"position": v(-10.16, -10.7) * mm});
            skPoint(sketch, "E12.5.88", {"position": v(-6.25, -10.83) * mm});
            skPoint(sketch, "E12.5.89", {"position": v(-6.71, -15.62) * mm});
            skPoint(sketch, "E12.5.90", {"position": v(-6.25, -10.83) * mm});
            skPoint(sketch, "E12.5.91", {"position": v(-8.6, -9.07) * mm});
            skPoint(sketch, "E12.5.92", {"position": v(-7.37, -12.77) * mm});
            skPoint(sketch, "E12.5.93", {"position": v(-10.16, -10.7) * mm});
            skPoint(sketch, "E12.5.94", {"position": v(-13.07, -10.87) * mm});
            skPoint(sketch, "E12.5.95", {"position": v(-10.16, -10.7) * mm});
            skPoint(sketch, "E12.5.96", {"position": v(-8.6, -9.07) * mm});
            skPoint(sketch, "E12.5.97", {"position": v(-7.37, -12.77) * mm});
            skPoint(sketch, "E12.5.98", {"position": v(-6.25, -10.83) * mm});
            skPoint(sketch, "E12.5.99", {"position": v(-6.71, -15.62) * mm});
            skPoint(sketch, "E12.5.100", {"position": v(-13.07, -10.87) * mm});
            skArc(sketch, "E12.5.101", {"start": v(-10.94, -10.74) * mm, "mid": v(-10.22, -10.56) * mm, "end": v(-9.61, -10.12) * mm});
            skArc(sketch, "E12.5.102", {"start": v(-7.91, -9.68) * mm, "mid": v(-8.6, -9.45) * mm, "end": v(-9.27, -9.76) * mm});
            skArc(sketch, "E12.5.103", {"start": v(-6.73, -11.66) * mm, "mid": v(-6.62, -10.94) * mm, "end": v(-7.03, -10.33) * mm});
            skArc(sketch, "E12.5.104", {"start": v(-10.94, -10.74) * mm, "mid": v(-10.22, -10.56) * mm, "end": v(-9.61, -10.12) * mm});
            skArc(sketch, "E12.5.105", {"start": v(-13.4, -10.46) * mm, "mid": v(-13.03, -10.75) * mm, "end": v(-12.56, -10.84) * mm});
            skArc(sketch, "E12.5.106", {"start": v(-7.91, -9.68) * mm, "mid": v(-8.6, -9.45) * mm, "end": v(-9.27, -9.76) * mm});
            skArc(sketch, "E12.5.107", {"start": v(-6.73, -11.66) * mm, "mid": v(-6.62, -10.94) * mm, "end": v(-7.03, -10.33) * mm});
            skArc(sketch, "E12.5.108", {"start": v(-6.83, -15.12) * mm, "mid": v(-6.61, -15.54) * mm, "end": v(-6.22, -15.82) * mm});
            skArc(sketch, "E12.5.109", {"start": v(-7.91, -9.68) * mm, "mid": v(-8.6, -9.45) * mm, "end": v(-9.27, -9.76) * mm});
            skArc(sketch, "E12.5.110", {"start": v(-6.73, -11.66) * mm, "mid": v(-6.62, -10.94) * mm, "end": v(-7.03, -10.33) * mm});
            skArc(sketch, "E12.5.111", {"start": v(-10.94, -10.74) * mm, "mid": v(-10.22, -10.56) * mm, "end": v(-9.61, -10.12) * mm});
            skArc(sketch, "E12.5.112", {"start": v(-13.4, -10.46) * mm, "mid": v(-13.03, -10.75) * mm, "end": v(-12.56, -10.84) * mm});
            skArc(sketch, "E12.5.113", {"start": v(-6.83, -15.12) * mm, "mid": v(-6.61, -15.54) * mm, "end": v(-6.22, -15.82) * mm});
            skArc(sketch, "E12.5.114", {"start": v(-7.91, -9.68) * mm, "mid": v(-8.6, -9.45) * mm, "end": v(-9.27, -9.76) * mm});
            skArc(sketch, "E12.5.115", {"start": v(-6.83, -15.12) * mm, "mid": v(-6.61, -15.54) * mm, "end": v(-6.22, -15.82) * mm});
            skArc(sketch, "E12.5.116", {"start": v(-6.73, -11.66) * mm, "mid": v(-6.62, -10.94) * mm, "end": v(-7.03, -10.33) * mm});
            skArc(sketch, "E12.5.117", {"start": v(-10.94, -10.74) * mm, "mid": v(-10.22, -10.56) * mm, "end": v(-9.61, -10.12) * mm});
            skArc(sketch, "E12.5.118", {"start": v(-13.4, -10.46) * mm, "mid": v(-13.03, -10.75) * mm, "end": v(-12.56, -10.84) * mm});
            skArc(sketch, "E12.5.119", {"start": v(-6.83, -15.12) * mm, "mid": v(-6.61, -15.54) * mm, "end": v(-6.22, -15.82) * mm});
            skArc(sketch, "E12.5.120", {"start": v(-6.73, -11.66) * mm, "mid": v(-6.62, -10.94) * mm, "end": v(-7.03, -10.33) * mm});
            skArc(sketch, "E12.5.121", {"start": v(-7.91, -9.68) * mm, "mid": v(-8.6, -9.45) * mm, "end": v(-9.27, -9.76) * mm});
            skArc(sketch, "E12.5.122", {"start": v(-10.94, -10.74) * mm, "mid": v(-10.22, -10.56) * mm, "end": v(-9.61, -10.12) * mm});
            skArc(sketch, "E12.5.123", {"start": v(-13.4, -10.46) * mm, "mid": v(-13.03, -10.75) * mm, "end": v(-12.56, -10.84) * mm});
            skArc(sketch, "E12.5.124", {"start": v(-6.83, -15.12) * mm, "mid": v(-6.61, -15.54) * mm, "end": v(-6.22, -15.82) * mm});
            skArc(sketch, "E12.5.125", {"start": v(-7.91, -9.68) * mm, "mid": v(-8.6, -9.45) * mm, "end": v(-9.27, -9.76) * mm});
            skArc(sketch, "E12.5.126", {"start": v(-6.73, -11.66) * mm, "mid": v(-6.62, -10.94) * mm, "end": v(-7.03, -10.33) * mm});
            skArc(sketch, "E12.5.127", {"start": v(-10.94, -10.74) * mm, "mid": v(-10.22, -10.56) * mm, "end": v(-9.61, -10.12) * mm});
            skArc(sketch, "E12.5.128", {"start": v(-13.4, -10.46) * mm, "mid": v(-13.03, -10.75) * mm, "end": v(-12.56, -10.84) * mm});
            skArc(sketch, "E12.5.129", {"start": v(-7.91, -9.68) * mm, "mid": v(-8.6, -9.45) * mm, "end": v(-9.27, -9.76) * mm});
            skArc(sketch, "E12.5.130", {"start": v(-6.83, -15.12) * mm, "mid": v(-6.61, -15.54) * mm, "end": v(-6.22, -15.82) * mm});
            skArc(sketch, "E12.5.131", {"start": v(-6.73, -11.66) * mm, "mid": v(-6.62, -10.94) * mm, "end": v(-7.03, -10.33) * mm});
            skArc(sketch, "E12.5.132", {"start": v(-13.4, -10.46) * mm, "mid": v(-13.03, -10.75) * mm, "end": v(-12.56, -10.84) * mm});
            skArc(sketch, "E12.5.133", {"start": v(-10.94, -10.74) * mm, "mid": v(-10.22, -10.56) * mm, "end": v(-9.61, -10.12) * mm});
            skArc(sketch, "E12.5.134", {"start": v(-10.94, -10.74) * mm, "mid": v(-10.22, -10.56) * mm, "end": v(-9.61, -10.12) * mm});
            skArc(sketch, "E12.5.135", {"start": v(-13.4, -10.46) * mm, "mid": v(-13.03, -10.75) * mm, "end": v(-12.56, -10.84) * mm});
            skArc(sketch, "E12.5.136", {"start": v(-7.91, -9.68) * mm, "mid": v(-8.6, -9.45) * mm, "end": v(-9.27, -9.76) * mm});
            skArc(sketch, "E12.5.137", {"start": v(-6.83, -15.12) * mm, "mid": v(-6.61, -15.54) * mm, "end": v(-6.22, -15.82) * mm});
            skArc(sketch, "E12.5.138", {"start": v(-6.73, -11.66) * mm, "mid": v(-6.62, -10.94) * mm, "end": v(-7.03, -10.33) * mm});
            skArc(sketch, "E12.5.139", {"start": v(-7.91, -9.68) * mm, "mid": v(-8.6, -9.45) * mm, "end": v(-9.27, -9.76) * mm});
            skArc(sketch, "E12.5.140", {"start": v(-6.73, -11.66) * mm, "mid": v(-6.62, -10.94) * mm, "end": v(-7.03, -10.33) * mm});
            skArc(sketch, "E12.5.141", {"start": v(-10.94, -10.74) * mm, "mid": v(-10.22, -10.56) * mm, "end": v(-9.61, -10.12) * mm});
            skArc(sketch, "E12.5.142", {"start": v(-13.4, -10.46) * mm, "mid": v(-13.03, -10.75) * mm, "end": v(-12.56, -10.84) * mm});
            skArc(sketch, "E12.5.143", {"start": v(-6.83, -15.12) * mm, "mid": v(-6.61, -15.54) * mm, "end": v(-6.22, -15.82) * mm});
            skArc(sketch, "E12.5.144", {"start": v(-6.83, -15.12) * mm, "mid": v(-6.61, -15.54) * mm, "end": v(-6.22, -15.82) * mm});
            skArc(sketch, "E12.5.145", {"start": v(-10.94, -10.74) * mm, "mid": v(-10.22, -10.56) * mm, "end": v(-9.61, -10.12) * mm});
            skArc(sketch, "E12.5.146", {"start": v(-7.91, -9.68) * mm, "mid": v(-8.6, -9.45) * mm, "end": v(-9.27, -9.76) * mm});
            skArc(sketch, "E12.5.147", {"start": v(-6.73, -11.66) * mm, "mid": v(-6.62, -10.94) * mm, "end": v(-7.03, -10.33) * mm});
            skArc(sketch, "E12.5.148", {"start": v(-13.4, -10.46) * mm, "mid": v(-13.03, -10.75) * mm, "end": v(-12.56, -10.84) * mm});
            skArc(sketch, "E12.5.149", {"start": v(-7.91, -9.68) * mm, "mid": v(-8.6, -9.45) * mm, "end": v(-9.27, -9.76) * mm});
            skArc(sketch, "E12.5.150", {"start": v(-6.83, -15.12) * mm, "mid": v(-6.61, -15.54) * mm, "end": v(-6.22, -15.82) * mm});
            skArc(sketch, "E12.5.151", {"start": v(-6.73, -11.66) * mm, "mid": v(-6.62, -10.94) * mm, "end": v(-7.03, -10.33) * mm});
            skArc(sketch, "E12.5.152", {"start": v(-13.4, -10.46) * mm, "mid": v(-13.03, -10.75) * mm, "end": v(-12.56, -10.84) * mm});
            skArc(sketch, "E12.5.153", {"start": v(-10.94, -10.74) * mm, "mid": v(-10.22, -10.56) * mm, "end": v(-9.61, -10.12) * mm});
            skArc(sketch, "E12.5.154", {"start": v(-6.83, -15.12) * mm, "mid": v(-6.61, -15.54) * mm, "end": v(-6.22, -15.82) * mm});
            skArc(sketch, "E12.5.155", {"start": v(-13.4, -10.46) * mm, "mid": v(-13.03, -10.75) * mm, "end": v(-12.56, -10.84) * mm});
            skArc(sketch, "E12.5.156", {"start": v(-7.91, -9.68) * mm, "mid": v(-8.6, -9.45) * mm, "end": v(-9.27, -9.76) * mm});
            skArc(sketch, "E12.5.157", {"start": v(-10.94, -10.74) * mm, "mid": v(-10.22, -10.56) * mm, "end": v(-9.61, -10.12) * mm});
            skArc(sketch, "E12.5.158", {"start": v(-6.73, -11.66) * mm, "mid": v(-6.62, -10.94) * mm, "end": v(-7.03, -10.33) * mm});
            skArc(sketch, "E12.5.159", {"start": v(-6.83, -15.12) * mm, "mid": v(-6.61, -15.54) * mm, "end": v(-6.22, -15.82) * mm});
            skArc(sketch, "E12.5.160", {"start": v(-6.73, -11.66) * mm, "mid": v(-6.62, -10.94) * mm, "end": v(-7.03, -10.33) * mm});
            skArc(sketch, "E12.5.161", {"start": v(-7.91, -9.68) * mm, "mid": v(-8.6, -9.45) * mm, "end": v(-9.27, -9.76) * mm});
            skArc(sketch, "E12.5.162", {"start": v(-10.94, -10.74) * mm, "mid": v(-10.22, -10.56) * mm, "end": v(-9.61, -10.12) * mm});
            skArc(sketch, "E12.5.163", {"start": v(-13.4, -10.46) * mm, "mid": v(-13.03, -10.75) * mm, "end": v(-12.56, -10.84) * mm});
            skArc(sketch, "E12.5.164", {"start": v(-6.98, -12.09) * mm, "mid": v(-7.23, -12.8) * mm, "end": v(-7.2, -13.54) * mm});
            skArc(sketch, "E12.5.165", {"start": v(-7.91, -9.68) * mm, "mid": v(-7.48, -10.01) * mm, "end": v(-7.03, -10.33) * mm});
            skArc(sketch, "E12.5.166", {"start": v(-13.4, -10.46) * mm, "mid": v(-13.03, -10.75) * mm, "end": v(-12.56, -10.84) * mm});
            skLineSegment(sketch, "E12.5.167", {"start": v(-10.94, -10.74) * mm, "end": v(-12.56, -10.84) * mm});
            skLineSegment(sketch, "E12.5.168", {"start": v(-7.2, -13.54) * mm, "end": v(-6.83, -15.12) * mm});
            skArc(sketch, "E12.5.169", {"start": v(-6.83, -15.12) * mm, "mid": v(-6.61, -15.54) * mm, "end": v(-6.22, -15.82) * mm});
            skLineSegment(sketch, "E12.5.170", {"start": v(-7.2, -13.54) * mm, "end": v(-6.83, -15.12) * mm});
            skLineSegment(sketch, "E12.5.171", {"start": v(-10.94, -10.74) * mm, "end": v(-12.56, -10.84) * mm});
            skLineSegment(sketch, "E12.5.172", {"start": v(-9.27, -9.76) * mm, "end": v(-9.61, -10.12) * mm});
            skArc(sketch, "E12.5.173", {"start": v(-7.91, -9.68) * mm, "mid": v(-7.48, -10.01) * mm, "end": v(-7.03, -10.33) * mm});
            skArc(sketch, "E12.5.174", {"start": v(-6.98, -12.09) * mm, "mid": v(-7.23, -12.8) * mm, "end": v(-7.2, -13.54) * mm});
            skLineSegment(sketch, "E12.5.175", {"start": v(-10.94, -10.74) * mm, "end": v(-12.56, -10.84) * mm});
            skArc(sketch, "E12.5.176", {"start": v(-6.98, -12.09) * mm, "mid": v(-7.23, -12.8) * mm, "end": v(-7.2, -13.54) * mm});
            skLineSegment(sketch, "E12.5.177", {"start": v(-7.2, -13.54) * mm, "end": v(-6.83, -15.12) * mm});
            skLineSegment(sketch, "E12.5.178", {"start": v(-9.27, -9.76) * mm, "end": v(-9.61, -10.12) * mm});
            skArc(sketch, "E12.5.179", {"start": v(-7.91, -9.68) * mm, "mid": v(-7.48, -10.01) * mm, "end": v(-7.03, -10.33) * mm});
            skLineSegment(sketch, "E12.5.180", {"start": v(-7.2, -13.54) * mm, "end": v(-6.83, -15.12) * mm});
            skArc(sketch, "E12.5.181", {"start": v(-6.98, -12.09) * mm, "mid": v(-7.23, -12.8) * mm, "end": v(-7.2, -13.54) * mm});
            skArc(sketch, "E12.5.182", {"start": v(-7.91, -9.68) * mm, "mid": v(-7.48, -10.01) * mm, "end": v(-7.03, -10.33) * mm});
            skLineSegment(sketch, "E12.5.183", {"start": v(-9.27, -9.76) * mm, "end": v(-9.61, -10.12) * mm});
            skLineSegment(sketch, "E12.5.184", {"start": v(-10.94, -10.74) * mm, "end": v(-12.56, -10.84) * mm});
            skArc(sketch, "E12.5.185", {"start": v(-6.98, -12.09) * mm, "mid": v(-7.23, -12.8) * mm, "end": v(-7.2, -13.54) * mm});
            skLineSegment(sketch, "E12.5.186", {"start": v(-7.2, -13.54) * mm, "end": v(-6.83, -15.12) * mm});
            skLineSegment(sketch, "E12.5.187", {"start": v(-10.94, -10.74) * mm, "end": v(-12.56, -10.84) * mm});
            skArc(sketch, "E12.5.188", {"start": v(-7.91, -9.68) * mm, "mid": v(-7.48, -10.01) * mm, "end": v(-7.03, -10.33) * mm});
            skLineSegment(sketch, "E12.5.189", {"start": v(-9.27, -9.76) * mm, "end": v(-9.61, -10.12) * mm});
            skArc(sketch, "E12.5.190", {"start": v(-6.98, -12.09) * mm, "mid": v(-7.23, -12.8) * mm, "end": v(-7.2, -13.54) * mm});
            skLineSegment(sketch, "E12.5.191", {"start": v(-10.94, -10.74) * mm, "end": v(-12.56, -10.84) * mm});
            skArc(sketch, "E12.5.192", {"start": v(-7.91, -9.68) * mm, "mid": v(-7.48, -10.01) * mm, "end": v(-7.03, -10.33) * mm});
            skLineSegment(sketch, "E12.5.193", {"start": v(-7.2, -13.54) * mm, "end": v(-6.83, -15.12) * mm});
            skLineSegment(sketch, "E12.5.194", {"start": v(-9.27, -9.76) * mm, "end": v(-9.61, -10.12) * mm});
            skLineSegment(sketch, "E12.5.195", {"start": v(-7.2, -13.54) * mm, "end": v(-6.83, -15.12) * mm});
            skArc(sketch, "E12.5.196", {"start": v(-7.91, -9.68) * mm, "mid": v(-7.48, -10.01) * mm, "end": v(-7.03, -10.33) * mm});
            skLineSegment(sketch, "E12.5.197", {"start": v(-10.94, -10.74) * mm, "end": v(-12.56, -10.84) * mm});
            skArc(sketch, "E12.5.198", {"start": v(-6.98, -12.09) * mm, "mid": v(-7.23, -12.8) * mm, "end": v(-7.2, -13.54) * mm});
            skLineSegment(sketch, "E12.5.199", {"start": v(-9.27, -9.76) * mm, "end": v(-9.61, -10.12) * mm});
            skLineSegment(sketch, "E12.5.200", {"start": v(-10.94, -10.74) * mm, "end": v(-12.56, -10.84) * mm});
            skArc(sketch, "E12.5.201", {"start": v(-7.91, -9.68) * mm, "mid": v(-7.48, -10.01) * mm, "end": v(-7.03, -10.33) * mm});
            skLineSegment(sketch, "E12.5.202", {"start": v(-6.98, -12.09) * mm, "end": v(-6.73, -11.66) * mm});
            skLineSegment(sketch, "E12.5.203", {"start": v(-7.2, -13.54) * mm, "end": v(-6.83, -15.12) * mm});
            skArc(sketch, "E12.5.204", {"start": v(-6.98, -12.09) * mm, "mid": v(-7.23, -12.8) * mm, "end": v(-7.2, -13.54) * mm});
            skLineSegment(sketch, "E12.5.205", {"start": v(-9.27, -9.76) * mm, "end": v(-9.61, -10.12) * mm});
            skLineSegment(sketch, "E12.5.206", {"start": v(-6.98, -12.09) * mm, "end": v(-6.73, -11.66) * mm});
            skLineSegment(sketch, "E12.5.207", {"start": v(-9.27, -9.76) * mm, "end": v(-9.61, -10.12) * mm});
            skArc(sketch, "E12.5.208", {"start": v(-6.98, -12.09) * mm, "mid": v(-7.23, -12.8) * mm, "end": v(-7.2, -13.54) * mm});
            skLineSegment(sketch, "E12.5.209", {"start": v(-10.94, -10.74) * mm, "end": v(-12.56, -10.84) * mm});
            skArc(sketch, "E12.5.210", {"start": v(-7.91, -9.68) * mm, "mid": v(-7.48, -10.01) * mm, "end": v(-7.03, -10.33) * mm});
            skLineSegment(sketch, "E12.5.211", {"start": v(-7.2, -13.54) * mm, "end": v(-6.83, -15.12) * mm});
            skArc(sketch, "E12.5.212", {"start": v(-7.91, -9.68) * mm, "mid": v(-7.48, -10.01) * mm, "end": v(-7.03, -10.33) * mm});
            skLineSegment(sketch, "E12.5.213", {"start": v(-7.2, -13.54) * mm, "end": v(-6.83, -15.12) * mm});
            skLineSegment(sketch, "E12.5.214", {"start": v(-10.94, -10.74) * mm, "end": v(-12.56, -10.84) * mm});
            skLineSegment(sketch, "E12.5.215", {"start": v(-6.98, -12.09) * mm, "end": v(-6.73, -11.66) * mm});
            skArc(sketch, "E12.5.216", {"start": v(-6.98, -12.09) * mm, "mid": v(-7.23, -12.8) * mm, "end": v(-7.2, -13.54) * mm});
            skLineSegment(sketch, "E12.5.217", {"start": v(-9.27, -9.76) * mm, "end": v(-9.61, -10.12) * mm});
            skLineSegment(sketch, "E12.5.218", {"start": v(-7.2, -13.54) * mm, "end": v(-6.83, -15.12) * mm});
            skArc(sketch, "E12.5.219", {"start": v(-6.98, -12.09) * mm, "mid": v(-7.23, -12.8) * mm, "end": v(-7.2, -13.54) * mm});
            skLineSegment(sketch, "E12.5.220", {"start": v(-10.94, -10.74) * mm, "end": v(-12.56, -10.84) * mm});
            skLineSegment(sketch, "E12.5.221", {"start": v(-9.27, -9.76) * mm, "end": v(-9.61, -10.12) * mm});
            skArc(sketch, "E12.5.222", {"start": v(-7.91, -9.68) * mm, "mid": v(-7.48, -10.01) * mm, "end": v(-7.03, -10.33) * mm});
            skLineSegment(sketch, "E12.5.223", {"start": v(-6.98, -12.09) * mm, "end": v(-6.73, -11.66) * mm});
            skLineSegment(sketch, "E12.5.224", {"start": v(-7.2, -13.54) * mm, "end": v(-6.83, -15.12) * mm});
            skLineSegment(sketch, "E12.5.225", {"start": v(-10.94, -10.74) * mm, "end": v(-12.56, -10.84) * mm});
            skLineSegment(sketch, "E12.5.226", {"start": v(-6.98, -12.09) * mm, "end": v(-6.73, -11.66) * mm});
            skArc(sketch, "E12.5.227", {"start": v(-6.98, -12.09) * mm, "mid": v(-7.23, -12.8) * mm, "end": v(-7.2, -13.54) * mm});
            skLineSegment(sketch, "E12.5.228", {"start": v(-9.27, -9.76) * mm, "end": v(-9.61, -10.12) * mm});
            skArc(sketch, "E12.5.229", {"start": v(-7.91, -9.68) * mm, "mid": v(-7.48, -10.01) * mm, "end": v(-7.03, -10.33) * mm});
            skArc(sketch, "E12.5.230", {"start": v(-7.91, -9.68) * mm, "mid": v(-7.48, -10.01) * mm, "end": v(-7.03, -10.33) * mm});
            skLineSegment(sketch, "E12.5.231", {"start": v(-9.27, -9.76) * mm, "end": v(-9.61, -10.12) * mm});
            skLineSegment(sketch, "E12.5.232", {"start": v(-7.2, -13.54) * mm, "end": v(-6.83, -15.12) * mm});
            skLineSegment(sketch, "E12.5.233", {"start": v(-6.98, -12.09) * mm, "end": v(-6.73, -11.66) * mm});
            skArc(sketch, "E12.5.234", {"start": v(-6.98, -12.09) * mm, "mid": v(-7.23, -12.8) * mm, "end": v(-7.2, -13.54) * mm});
            skLineSegment(sketch, "E12.5.235", {"start": v(-10.94, -10.74) * mm, "end": v(-12.56, -10.84) * mm});
            skLineSegment(sketch, "E12.5.236", {"start": v(-9.27, -9.76) * mm, "end": v(-9.61, -10.12) * mm});
            skLineSegment(sketch, "E12.5.237", {"start": v(-6.98, -12.09) * mm, "end": v(-6.73, -11.66) * mm});
            skLineSegment(sketch, "E12.5.238", {"start": v(-6.98, -12.09) * mm, "end": v(-6.73, -11.66) * mm});
            skLineSegment(sketch, "E12.5.239", {"start": v(-6.98, -12.09) * mm, "end": v(-6.73, -11.66) * mm});
            skLineSegment(sketch, "E12.5.240", {"start": v(-6.98, -12.09) * mm, "end": v(-6.73, -11.66) * mm});
            skLineSegment(sketch, "E12.5.241", {"start": v(-6.98, -12.09) * mm, "end": v(-6.73, -11.66) * mm});
            skLineSegment(sketch, "E12.5.242", {"start": v(-6.98, -12.09) * mm, "end": v(-6.73, -11.66) * mm});
            skLineSegment(sketch, "E12.5.243", {"start": v(-6.98, -12.09) * mm, "end": v(-6.73, -11.66) * mm});
            skLineSegment(sketch, "E12.6.0", {"start": v(2.52, -16.81) * mm, "end": v(0, 0) * mm});
            skPoint(sketch, "E12.6.1", {"position": v(2, -16.88) * mm});
            skPoint(sketch, "E12.6.2", {"position": v(-3.97, -16.53) * mm});
            skLineSegment(sketch, "E12.6.3", {"start": v(-6.38, -15.76) * mm, "end": v(0, 0) * mm});
            skPoint(sketch, "E12.6.4", {"position": v(-3.45, -14.34) * mm});
            skPoint(sketch, "E12.6.6", {"position": v(-5.89, -15.95) * mm});
            skPoint(sketch, "E12.6.7", {"position": v(0, -12.5) * mm});
            skPoint(sketch, "E12.6.8", {"position": v(0, -17) * mm});
            skPoint(sketch, "E12.6.9", {"position": v(0, -14.75) * mm});
            skPoint(sketch, "E12.6.10", {"position": v(-2.92, -12.15) * mm});
            skPoint(sketch, "E12.6.11", {"position": v(-3.97, -16.53) * mm});
            skPoint(sketch, "E12.6.12", {"position": v(-5.89, -15.95) * mm});
            skPoint(sketch, "E12.6.13", {"position": v(-2.92, -12.15) * mm});
            skPoint(sketch, "E12.6.14", {"position": v(0, -12.5) * mm});
            skPoint(sketch, "E12.6.15", {"position": v(-3.45, -14.34) * mm});
            skPoint(sketch, "E12.6.16", {"position": v(2, -16.88) * mm});
            skPoint(sketch, "E12.6.17", {"position": v(0, -14.75) * mm});
            skPoint(sketch, "E12.6.18", {"position": v(0, -17) * mm});
            skPoint(sketch, "E12.6.19", {"position": v(-5.89, -15.95) * mm});
            skPoint(sketch, "E12.6.20", {"position": v(-3.97, -16.53) * mm});
            skPoint(sketch, "E12.6.21", {"position": v(-2.92, -12.15) * mm});
            skPoint(sketch, "E12.6.22", {"position": v(0, -14.75) * mm});
            skPoint(sketch, "E12.6.23", {"position": v(-3.45, -14.34) * mm});
            skPoint(sketch, "E12.6.24", {"position": v(0, -12.5) * mm});
            skPoint(sketch, "E12.6.25", {"position": v(0, -17) * mm});
            skPoint(sketch, "E12.6.26", {"position": v(2, -16.88) * mm});
            skPoint(sketch, "E12.6.27", {"position": v(-3.97, -16.53) * mm});
            skPoint(sketch, "E12.6.28", {"position": v(-3.45, -14.34) * mm});
            skPoint(sketch, "E12.6.29", {"position": v(0, -17) * mm});
            skPoint(sketch, "E12.6.30", {"position": v(2, -16.88) * mm});
            skPoint(sketch, "E12.6.31", {"position": v(-5.89, -15.95) * mm});
            skPoint(sketch, "E12.6.32", {"position": v(0, -12.5) * mm});
            skPoint(sketch, "E12.6.33", {"position": v(0, -14.75) * mm});
            skPoint(sketch, "E12.6.34", {"position": v(-2.92, -12.15) * mm});
            skPoint(sketch, "E12.6.35", {"position": v(0, -12.5) * mm});
            skPoint(sketch, "E12.6.36", {"position": v(2, -16.88) * mm});
            skPoint(sketch, "E12.6.37", {"position": v(-5.89, -15.95) * mm});
            skPoint(sketch, "E12.6.38", {"position": v(-3.97, -16.53) * mm});
            skPoint(sketch, "E12.6.39", {"position": v(0, -17) * mm});
            skPoint(sketch, "E12.6.40", {"position": v(-3.45, -14.34) * mm});
            skPoint(sketch, "E12.6.41", {"position": v(0, -14.75) * mm});
            skPoint(sketch, "E12.6.42", {"position": v(-2.92, -12.15) * mm});
            skPoint(sketch, "E12.6.43", {"position": v(-2.92, -12.15) * mm});
            skPoint(sketch, "E12.6.44", {"position": v(-5.89, -15.95) * mm});
            skPoint(sketch, "E12.6.45", {"position": v(2, -16.88) * mm});
            skPoint(sketch, "E12.6.46", {"position": v(-3.97, -16.53) * mm});
            skPoint(sketch, "E12.6.47", {"position": v(-3.45, -14.34) * mm});
            skPoint(sketch, "E12.6.48", {"position": v(0, -12.5) * mm});
            skPoint(sketch, "E12.6.49", {"position": v(0, -14.75) * mm});
            skPoint(sketch, "E12.6.50", {"position": v(-3.45, -14.34) * mm});
            skPoint(sketch, "E12.6.51", {"position": v(-5.89, -15.95) * mm});
            skPoint(sketch, "E12.6.52", {"position": v(0, -14.75) * mm});
            skPoint(sketch, "E12.6.53", {"position": v(0, -12.5) * mm});
            skPoint(sketch, "E12.6.54", {"position": v(-2.92, -12.15) * mm});
            skPoint(sketch, "E12.6.55", {"position": v(0, -17) * mm});
            skPoint(sketch, "E12.6.56", {"position": v(-3.97, -16.53) * mm});
            skPoint(sketch, "E12.6.57", {"position": v(2, -16.88) * mm});
            skPoint(sketch, "E12.6.58", {"position": v(-5.89, -15.95) * mm});
            skPoint(sketch, "E12.6.59", {"position": v(0, -14.75) * mm});
            skPoint(sketch, "E12.6.60", {"position": v(2, -16.88) * mm});
            skPoint(sketch, "E12.6.61", {"position": v(-3.45, -14.34) * mm});
            skPoint(sketch, "E12.6.62", {"position": v(-2.92, -12.15) * mm});
            skPoint(sketch, "E12.6.63", {"position": v(0, -12.5) * mm});
            skPoint(sketch, "E12.6.64", {"position": v(-3.97, -16.53) * mm});
            skPoint(sketch, "E12.6.65", {"position": v(0, -17) * mm});
            skPoint(sketch, "E12.6.66", {"position": v(0, -14.75) * mm});
            skPoint(sketch, "E12.6.67", {"position": v(0, -12.5) * mm});
            skPoint(sketch, "E12.6.68", {"position": v(-3.45, -14.34) * mm});
            skPoint(sketch, "E12.6.69", {"position": v(-2.92, -12.15) * mm});
            skPoint(sketch, "E12.6.70", {"position": v(2, -16.88) * mm});
            skPoint(sketch, "E12.6.71", {"position": v(0, -17) * mm});
            skPoint(sketch, "E12.6.72", {"position": v(-5.89, -15.95) * mm});
            skPoint(sketch, "E12.6.73", {"position": v(-3.97, -16.53) * mm});
            skPoint(sketch, "E12.6.74", {"position": v(0, -17) * mm});
            skPoint(sketch, "E12.6.75", {"position": v(0, -12.5) * mm});
            skPoint(sketch, "E12.6.76", {"position": v(-5.89, -15.95) * mm});
            skPoint(sketch, "E12.6.77", {"position": v(0, -14.75) * mm});
            skPoint(sketch, "E12.6.78", {"position": v(2, -16.88) * mm});
            skPoint(sketch, "E12.6.79", {"position": v(-3.45, -14.34) * mm});
            skPoint(sketch, "E12.6.80", {"position": v(-3.97, -16.53) * mm});
            skPoint(sketch, "E12.6.81", {"position": v(-2.92, -12.15) * mm});
            skPoint(sketch, "E12.6.82", {"position": v(0, -17) * mm});
            skPoint(sketch, "E12.6.83", {"position": v(-5.89, -15.95) * mm});
            skPoint(sketch, "E12.6.84", {"position": v(2, -16.88) * mm});
            skPoint(sketch, "E12.6.85", {"position": v(-2.92, -12.15) * mm});
            skPoint(sketch, "E12.6.86", {"position": v(0, -14.75) * mm});
            skPoint(sketch, "E12.6.87", {"position": v(-3.45, -14.34) * mm});
            skPoint(sketch, "E12.6.88", {"position": v(0, -12.5) * mm});
            skPoint(sketch, "E12.6.89", {"position": v(2, -16.88) * mm});
            skPoint(sketch, "E12.6.90", {"position": v(0, -12.5) * mm});
            skPoint(sketch, "E12.6.91", {"position": v(-2.92, -12.15) * mm});
            skPoint(sketch, "E12.6.92", {"position": v(0, -14.75) * mm});
            skPoint(sketch, "E12.6.93", {"position": v(-3.45, -14.34) * mm});
            skPoint(sketch, "E12.6.94", {"position": v(-5.89, -15.95) * mm});
            skPoint(sketch, "E12.6.95", {"position": v(-3.45, -14.34) * mm});
            skPoint(sketch, "E12.6.96", {"position": v(-2.92, -12.15) * mm});
            skPoint(sketch, "E12.6.97", {"position": v(0, -14.75) * mm});
            skPoint(sketch, "E12.6.98", {"position": v(0, -12.5) * mm});
            skPoint(sketch, "E12.6.99", {"position": v(2, -16.88) * mm});
            skPoint(sketch, "E12.6.100", {"position": v(-5.89, -15.95) * mm});
            skArc(sketch, "E12.6.101", {"start": v(-4.1, -14.78) * mm, "mid": v(-3.57, -14.26) * mm, "end": v(-3.26, -13.57) * mm});
            skArc(sketch, "E12.6.102", {"start": v(-2.01, -12.34) * mm, "mid": v(-2.73, -12.5) * mm, "end": v(-3.15, -13.1) * mm});
            skArc(sketch, "E12.6.103", {"start": v(0, -13.46) * mm, "mid": v(-0.27, -12.78) * mm, "end": v(-0.93, -12.47) * mm});
            skArc(sketch, "E12.6.104", {"start": v(-4.1, -14.78) * mm, "mid": v(-3.57, -14.26) * mm, "end": v(-3.26, -13.57) * mm});
            skArc(sketch, "E12.6.105", {"start": v(-6.38, -15.76) * mm, "mid": v(-5.9, -15.83) * mm, "end": v(-5.46, -15.67) * mm});
            skArc(sketch, "E12.6.106", {"start": v(-2.01, -12.34) * mm, "mid": v(-2.73, -12.5) * mm, "end": v(-3.15, -13.1) * mm});
            skArc(sketch, "E12.6.107", {"start": v(0, -13.46) * mm, "mid": v(-0.27, -12.78) * mm, "end": v(-0.93, -12.47) * mm});
            skArc(sketch, "E12.6.108", {"start": v(1.64, -16.5) * mm, "mid": v(2.05, -16.77) * mm, "end": v(2.52, -16.81) * mm});
            skArc(sketch, "E12.6.109", {"start": v(-2.01, -12.34) * mm, "mid": v(-2.73, -12.5) * mm, "end": v(-3.15, -13.1) * mm});
            skArc(sketch, "E12.6.110", {"start": v(0, -13.46) * mm, "mid": v(-0.27, -12.78) * mm, "end": v(-0.93, -12.47) * mm});
            skArc(sketch, "E12.6.111", {"start": v(-4.1, -14.78) * mm, "mid": v(-3.57, -14.26) * mm, "end": v(-3.26, -13.57) * mm});
            skArc(sketch, "E12.6.112", {"start": v(-6.38, -15.76) * mm, "mid": v(-5.9, -15.83) * mm, "end": v(-5.46, -15.67) * mm});
            skArc(sketch, "E12.6.113", {"start": v(1.64, -16.5) * mm, "mid": v(2.05, -16.77) * mm, "end": v(2.52, -16.81) * mm});
            skArc(sketch, "E12.6.114", {"start": v(-2.01, -12.34) * mm, "mid": v(-2.73, -12.5) * mm, "end": v(-3.15, -13.1) * mm});
            skArc(sketch, "E12.6.115", {"start": v(1.64, -16.5) * mm, "mid": v(2.05, -16.77) * mm, "end": v(2.52, -16.81) * mm});
            skArc(sketch, "E12.6.116", {"start": v(0, -13.46) * mm, "mid": v(-0.27, -12.78) * mm, "end": v(-0.93, -12.47) * mm});
            skArc(sketch, "E12.6.117", {"start": v(-4.1, -14.78) * mm, "mid": v(-3.57, -14.26) * mm, "end": v(-3.26, -13.57) * mm});
            skArc(sketch, "E12.6.118", {"start": v(-6.38, -15.76) * mm, "mid": v(-5.9, -15.83) * mm, "end": v(-5.46, -15.67) * mm});
            skArc(sketch, "E12.6.119", {"start": v(1.64, -16.5) * mm, "mid": v(2.05, -16.77) * mm, "end": v(2.52, -16.81) * mm});
            skArc(sketch, "E12.6.120", {"start": v(0, -13.46) * mm, "mid": v(-0.27, -12.78) * mm, "end": v(-0.93, -12.47) * mm});
            skArc(sketch, "E12.6.121", {"start": v(-2.01, -12.34) * mm, "mid": v(-2.73, -12.5) * mm, "end": v(-3.15, -13.1) * mm});
            skArc(sketch, "E12.6.122", {"start": v(-4.1, -14.78) * mm, "mid": v(-3.57, -14.26) * mm, "end": v(-3.26, -13.57) * mm});
            skArc(sketch, "E12.6.123", {"start": v(-6.38, -15.76) * mm, "mid": v(-5.9, -15.83) * mm, "end": v(-5.46, -15.67) * mm});
            skArc(sketch, "E12.6.124", {"start": v(1.64, -16.5) * mm, "mid": v(2.05, -16.77) * mm, "end": v(2.52, -16.81) * mm});
            skArc(sketch, "E12.6.125", {"start": v(-2.01, -12.34) * mm, "mid": v(-2.73, -12.5) * mm, "end": v(-3.15, -13.1) * mm});
            skArc(sketch, "E12.6.126", {"start": v(0, -13.46) * mm, "mid": v(-0.27, -12.78) * mm, "end": v(-0.93, -12.47) * mm});
            skArc(sketch, "E12.6.127", {"start": v(-4.1, -14.78) * mm, "mid": v(-3.57, -14.26) * mm, "end": v(-3.26, -13.57) * mm});
            skArc(sketch, "E12.6.128", {"start": v(-6.38, -15.76) * mm, "mid": v(-5.9, -15.83) * mm, "end": v(-5.46, -15.67) * mm});
            skArc(sketch, "E12.6.129", {"start": v(-2.01, -12.34) * mm, "mid": v(-2.73, -12.5) * mm, "end": v(-3.15, -13.1) * mm});
            skArc(sketch, "E12.6.130", {"start": v(1.64, -16.5) * mm, "mid": v(2.05, -16.77) * mm, "end": v(2.52, -16.81) * mm});
            skArc(sketch, "E12.6.131", {"start": v(0, -13.46) * mm, "mid": v(-0.27, -12.78) * mm, "end": v(-0.93, -12.47) * mm});
            skArc(sketch, "E12.6.132", {"start": v(-6.38, -15.76) * mm, "mid": v(-5.9, -15.83) * mm, "end": v(-5.46, -15.67) * mm});
            skArc(sketch, "E12.6.133", {"start": v(-4.1, -14.78) * mm, "mid": v(-3.57, -14.26) * mm, "end": v(-3.26, -13.57) * mm});
            skArc(sketch, "E12.6.134", {"start": v(-4.1, -14.78) * mm, "mid": v(-3.57, -14.26) * mm, "end": v(-3.26, -13.57) * mm});
            skArc(sketch, "E12.6.135", {"start": v(-6.38, -15.76) * mm, "mid": v(-5.9, -15.83) * mm, "end": v(-5.46, -15.67) * mm});
            skArc(sketch, "E12.6.136", {"start": v(-2.01, -12.34) * mm, "mid": v(-2.73, -12.5) * mm, "end": v(-3.15, -13.1) * mm});
            skArc(sketch, "E12.6.137", {"start": v(1.64, -16.5) * mm, "mid": v(2.05, -16.77) * mm, "end": v(2.52, -16.81) * mm});
            skArc(sketch, "E12.6.138", {"start": v(0, -13.46) * mm, "mid": v(-0.27, -12.78) * mm, "end": v(-0.93, -12.47) * mm});
            skArc(sketch, "E12.6.139", {"start": v(-2.01, -12.34) * mm, "mid": v(-2.73, -12.5) * mm, "end": v(-3.15, -13.1) * mm});
            skArc(sketch, "E12.6.140", {"start": v(0, -13.46) * mm, "mid": v(-0.27, -12.78) * mm, "end": v(-0.93, -12.47) * mm});
            skArc(sketch, "E12.6.141", {"start": v(-4.1, -14.78) * mm, "mid": v(-3.57, -14.26) * mm, "end": v(-3.26, -13.57) * mm});
            skArc(sketch, "E12.6.142", {"start": v(-6.38, -15.76) * mm, "mid": v(-5.9, -15.83) * mm, "end": v(-5.46, -15.67) * mm});
            skArc(sketch, "E12.6.143", {"start": v(1.64, -16.5) * mm, "mid": v(2.05, -16.77) * mm, "end": v(2.52, -16.81) * mm});
            skArc(sketch, "E12.6.144", {"start": v(1.64, -16.5) * mm, "mid": v(2.05, -16.77) * mm, "end": v(2.52, -16.81) * mm});
            skArc(sketch, "E12.6.145", {"start": v(-4.1, -14.78) * mm, "mid": v(-3.57, -14.26) * mm, "end": v(-3.26, -13.57) * mm});
            skArc(sketch, "E12.6.146", {"start": v(-2.01, -12.34) * mm, "mid": v(-2.73, -12.5) * mm, "end": v(-3.15, -13.1) * mm});
            skArc(sketch, "E12.6.147", {"start": v(0, -13.46) * mm, "mid": v(-0.27, -12.78) * mm, "end": v(-0.93, -12.47) * mm});
            skArc(sketch, "E12.6.148", {"start": v(-6.38, -15.76) * mm, "mid": v(-5.9, -15.83) * mm, "end": v(-5.46, -15.67) * mm});
            skArc(sketch, "E12.6.149", {"start": v(-2.01, -12.34) * mm, "mid": v(-2.73, -12.5) * mm, "end": v(-3.15, -13.1) * mm});
            skArc(sketch, "E12.6.150", {"start": v(1.64, -16.5) * mm, "mid": v(2.05, -16.77) * mm, "end": v(2.52, -16.81) * mm});
            skArc(sketch, "E12.6.151", {"start": v(0, -13.46) * mm, "mid": v(-0.27, -12.78) * mm, "end": v(-0.93, -12.47) * mm});
            skArc(sketch, "E12.6.152", {"start": v(-6.38, -15.76) * mm, "mid": v(-5.9, -15.83) * mm, "end": v(-5.46, -15.67) * mm});
            skArc(sketch, "E12.6.153", {"start": v(-4.1, -14.78) * mm, "mid": v(-3.57, -14.26) * mm, "end": v(-3.26, -13.57) * mm});
            skArc(sketch, "E12.6.154", {"start": v(1.64, -16.5) * mm, "mid": v(2.05, -16.77) * mm, "end": v(2.52, -16.81) * mm});
            skArc(sketch, "E12.6.155", {"start": v(-6.38, -15.76) * mm, "mid": v(-5.9, -15.83) * mm, "end": v(-5.46, -15.67) * mm});
            skArc(sketch, "E12.6.156", {"start": v(-2.01, -12.34) * mm, "mid": v(-2.73, -12.5) * mm, "end": v(-3.15, -13.1) * mm});
            skArc(sketch, "E12.6.157", {"start": v(-4.1, -14.78) * mm, "mid": v(-3.57, -14.26) * mm, "end": v(-3.26, -13.57) * mm});
            skArc(sketch, "E12.6.158", {"start": v(0, -13.46) * mm, "mid": v(-0.27, -12.78) * mm, "end": v(-0.93, -12.47) * mm});
            skArc(sketch, "E12.6.159", {"start": v(1.64, -16.5) * mm, "mid": v(2.05, -16.77) * mm, "end": v(2.52, -16.81) * mm});
            skArc(sketch, "E12.6.160", {"start": v(0, -13.46) * mm, "mid": v(-0.27, -12.78) * mm, "end": v(-0.93, -12.47) * mm});
            skArc(sketch, "E12.6.161", {"start": v(-2.01, -12.34) * mm, "mid": v(-2.73, -12.5) * mm, "end": v(-3.15, -13.1) * mm});
            skArc(sketch, "E12.6.162", {"start": v(-4.1, -14.78) * mm, "mid": v(-3.57, -14.26) * mm, "end": v(-3.26, -13.57) * mm});
            skArc(sketch, "E12.6.163", {"start": v(-6.38, -15.76) * mm, "mid": v(-5.9, -15.83) * mm, "end": v(-5.46, -15.67) * mm});
            skArc(sketch, "E12.6.164", {"start": v(0, -13.96) * mm, "mid": v(0.14, -14.7) * mm, "end": v(0.54, -15.33) * mm});
            skArc(sketch, "E12.6.165", {"start": v(-2.01, -12.34) * mm, "mid": v(-1.47, -12.41) * mm, "end": v(-0.93, -12.47) * mm});
            skArc(sketch, "E12.6.166", {"start": v(-6.38, -15.76) * mm, "mid": v(-5.9, -15.83) * mm, "end": v(-5.46, -15.67) * mm});
            skLineSegment(sketch, "E12.6.167", {"start": v(-4.1, -14.78) * mm, "end": v(-5.46, -15.67) * mm});
            skLineSegment(sketch, "E12.6.168", {"start": v(0.54, -15.33) * mm, "end": v(1.64, -16.5) * mm});
            skArc(sketch, "E12.6.169", {"start": v(1.64, -16.5) * mm, "mid": v(2.05, -16.77) * mm, "end": v(2.52, -16.81) * mm});
            skLineSegment(sketch, "E12.6.170", {"start": v(0.54, -15.33) * mm, "end": v(1.64, -16.5) * mm});
            skLineSegment(sketch, "E12.6.171", {"start": v(-4.1, -14.78) * mm, "end": v(-5.46, -15.67) * mm});
            skLineSegment(sketch, "E12.6.172", {"start": v(-3.15, -13.1) * mm, "end": v(-3.26, -13.57) * mm});
            skArc(sketch, "E12.6.173", {"start": v(-2.01, -12.34) * mm, "mid": v(-1.47, -12.41) * mm, "end": v(-0.93, -12.47) * mm});
            skArc(sketch, "E12.6.174", {"start": v(0, -13.96) * mm, "mid": v(0.14, -14.7) * mm, "end": v(0.54, -15.33) * mm});
            skLineSegment(sketch, "E12.6.175", {"start": v(-4.1, -14.78) * mm, "end": v(-5.46, -15.67) * mm});
            skArc(sketch, "E12.6.176", {"start": v(0, -13.96) * mm, "mid": v(0.14, -14.7) * mm, "end": v(0.54, -15.33) * mm});
            skLineSegment(sketch, "E12.6.177", {"start": v(0.54, -15.33) * mm, "end": v(1.64, -16.5) * mm});
            skLineSegment(sketch, "E12.6.178", {"start": v(-3.15, -13.1) * mm, "end": v(-3.26, -13.57) * mm});
            skArc(sketch, "E12.6.179", {"start": v(-2.01, -12.34) * mm, "mid": v(-1.47, -12.41) * mm, "end": v(-0.93, -12.47) * mm});
            skLineSegment(sketch, "E12.6.180", {"start": v(0.54, -15.33) * mm, "end": v(1.64, -16.5) * mm});
            skArc(sketch, "E12.6.181", {"start": v(0, -13.96) * mm, "mid": v(0.14, -14.7) * mm, "end": v(0.54, -15.33) * mm});
            skArc(sketch, "E12.6.182", {"start": v(-2.01, -12.34) * mm, "mid": v(-1.47, -12.41) * mm, "end": v(-0.93, -12.47) * mm});
            skLineSegment(sketch, "E12.6.183", {"start": v(-3.15, -13.1) * mm, "end": v(-3.26, -13.57) * mm});
            skLineSegment(sketch, "E12.6.184", {"start": v(-4.1, -14.78) * mm, "end": v(-5.46, -15.67) * mm});
            skArc(sketch, "E12.6.185", {"start": v(0, -13.96) * mm, "mid": v(0.14, -14.7) * mm, "end": v(0.54, -15.33) * mm});
            skLineSegment(sketch, "E12.6.186", {"start": v(0.54, -15.33) * mm, "end": v(1.64, -16.5) * mm});
            skLineSegment(sketch, "E12.6.187", {"start": v(-4.1, -14.78) * mm, "end": v(-5.46, -15.67) * mm});
            skArc(sketch, "E12.6.188", {"start": v(-2.01, -12.34) * mm, "mid": v(-1.47, -12.41) * mm, "end": v(-0.93, -12.47) * mm});
            skLineSegment(sketch, "E12.6.189", {"start": v(-3.15, -13.1) * mm, "end": v(-3.26, -13.57) * mm});
            skArc(sketch, "E12.6.190", {"start": v(0, -13.96) * mm, "mid": v(0.14, -14.7) * mm, "end": v(0.54, -15.33) * mm});
            skLineSegment(sketch, "E12.6.191", {"start": v(-4.1, -14.78) * mm, "end": v(-5.46, -15.67) * mm});
            skArc(sketch, "E12.6.192", {"start": v(-2.01, -12.34) * mm, "mid": v(-1.47, -12.41) * mm, "end": v(-0.93, -12.47) * mm});
            skLineSegment(sketch, "E12.6.193", {"start": v(0.54, -15.33) * mm, "end": v(1.64, -16.5) * mm});
            skLineSegment(sketch, "E12.6.194", {"start": v(-3.15, -13.1) * mm, "end": v(-3.26, -13.57) * mm});
            skLineSegment(sketch, "E12.6.195", {"start": v(0.54, -15.33) * mm, "end": v(1.64, -16.5) * mm});
            skArc(sketch, "E12.6.196", {"start": v(-2.01, -12.34) * mm, "mid": v(-1.47, -12.41) * mm, "end": v(-0.93, -12.47) * mm});
            skLineSegment(sketch, "E12.6.197", {"start": v(-4.1, -14.78) * mm, "end": v(-5.46, -15.67) * mm});
            skArc(sketch, "E12.6.198", {"start": v(0, -13.96) * mm, "mid": v(0.14, -14.7) * mm, "end": v(0.54, -15.33) * mm});
            skLineSegment(sketch, "E12.6.199", {"start": v(-3.15, -13.1) * mm, "end": v(-3.26, -13.57) * mm});
            skLineSegment(sketch, "E12.6.200", {"start": v(-4.1, -14.78) * mm, "end": v(-5.46, -15.67) * mm});
            skArc(sketch, "E12.6.201", {"start": v(-2.01, -12.34) * mm, "mid": v(-1.47, -12.41) * mm, "end": v(-0.93, -12.47) * mm});
            skLineSegment(sketch, "E12.6.202", {"start": v(0, -13.96) * mm, "end": v(0, -13.46) * mm});
            skLineSegment(sketch, "E12.6.203", {"start": v(0.54, -15.33) * mm, "end": v(1.64, -16.5) * mm});
            skArc(sketch, "E12.6.204", {"start": v(0, -13.96) * mm, "mid": v(0.14, -14.7) * mm, "end": v(0.54, -15.33) * mm});
            skLineSegment(sketch, "E12.6.205", {"start": v(-3.15, -13.1) * mm, "end": v(-3.26, -13.57) * mm});
            skLineSegment(sketch, "E12.6.206", {"start": v(0, -13.96) * mm, "end": v(0, -13.46) * mm});
            skLineSegment(sketch, "E12.6.207", {"start": v(-3.15, -13.1) * mm, "end": v(-3.26, -13.57) * mm});
            skArc(sketch, "E12.6.208", {"start": v(0, -13.96) * mm, "mid": v(0.14, -14.7) * mm, "end": v(0.54, -15.33) * mm});
            skLineSegment(sketch, "E12.6.209", {"start": v(-4.1, -14.78) * mm, "end": v(-5.46, -15.67) * mm});
            skArc(sketch, "E12.6.210", {"start": v(-2.01, -12.34) * mm, "mid": v(-1.47, -12.41) * mm, "end": v(-0.93, -12.47) * mm});
            skLineSegment(sketch, "E12.6.211", {"start": v(0.54, -15.33) * mm, "end": v(1.64, -16.5) * mm});
            skArc(sketch, "E12.6.212", {"start": v(-2.01, -12.34) * mm, "mid": v(-1.47, -12.41) * mm, "end": v(-0.93, -12.47) * mm});
            skLineSegment(sketch, "E12.6.213", {"start": v(0.54, -15.33) * mm, "end": v(1.64, -16.5) * mm});
            skLineSegment(sketch, "E12.6.214", {"start": v(-4.1, -14.78) * mm, "end": v(-5.46, -15.67) * mm});
            skLineSegment(sketch, "E12.6.215", {"start": v(0, -13.96) * mm, "end": v(0, -13.46) * mm});
            skArc(sketch, "E12.6.216", {"start": v(0, -13.96) * mm, "mid": v(0.14, -14.7) * mm, "end": v(0.54, -15.33) * mm});
            skLineSegment(sketch, "E12.6.217", {"start": v(-3.15, -13.1) * mm, "end": v(-3.26, -13.57) * mm});
            skLineSegment(sketch, "E12.6.218", {"start": v(0.54, -15.33) * mm, "end": v(1.64, -16.5) * mm});
            skArc(sketch, "E12.6.219", {"start": v(0, -13.96) * mm, "mid": v(0.14, -14.7) * mm, "end": v(0.54, -15.33) * mm});
            skLineSegment(sketch, "E12.6.220", {"start": v(-4.1, -14.78) * mm, "end": v(-5.46, -15.67) * mm});
            skLineSegment(sketch, "E12.6.221", {"start": v(-3.15, -13.1) * mm, "end": v(-3.26, -13.57) * mm});
            skArc(sketch, "E12.6.222", {"start": v(-2.01, -12.34) * mm, "mid": v(-1.47, -12.41) * mm, "end": v(-0.93, -12.47) * mm});
            skLineSegment(sketch, "E12.6.223", {"start": v(0, -13.96) * mm, "end": v(0, -13.46) * mm});
            skLineSegment(sketch, "E12.6.224", {"start": v(0.54, -15.33) * mm, "end": v(1.64, -16.5) * mm});
            skLineSegment(sketch, "E12.6.225", {"start": v(-4.1, -14.78) * mm, "end": v(-5.46, -15.67) * mm});
            skLineSegment(sketch, "E12.6.226", {"start": v(0, -13.96) * mm, "end": v(0, -13.46) * mm});
            skArc(sketch, "E12.6.227", {"start": v(0, -13.96) * mm, "mid": v(0.14, -14.7) * mm, "end": v(0.54, -15.33) * mm});
            skLineSegment(sketch, "E12.6.228", {"start": v(-3.15, -13.1) * mm, "end": v(-3.26, -13.57) * mm});
            skArc(sketch, "E12.6.229", {"start": v(-2.01, -12.34) * mm, "mid": v(-1.47, -12.41) * mm, "end": v(-0.93, -12.47) * mm});
            skArc(sketch, "E12.6.230", {"start": v(-2.01, -12.34) * mm, "mid": v(-1.47, -12.41) * mm, "end": v(-0.93, -12.47) * mm});
            skLineSegment(sketch, "E12.6.231", {"start": v(-3.15, -13.1) * mm, "end": v(-3.26, -13.57) * mm});
            skLineSegment(sketch, "E12.6.232", {"start": v(0.54, -15.33) * mm, "end": v(1.64, -16.5) * mm});
            skLineSegment(sketch, "E12.6.233", {"start": v(0, -13.96) * mm, "end": v(0, -13.46) * mm});
            skArc(sketch, "E12.6.234", {"start": v(0, -13.96) * mm, "mid": v(0.14, -14.7) * mm, "end": v(0.54, -15.33) * mm});
            skLineSegment(sketch, "E12.6.235", {"start": v(-4.1, -14.78) * mm, "end": v(-5.46, -15.67) * mm});
            skLineSegment(sketch, "E12.6.236", {"start": v(-3.15, -13.1) * mm, "end": v(-3.26, -13.57) * mm});
            skLineSegment(sketch, "E12.6.237", {"start": v(0, -13.96) * mm, "end": v(0, -13.46) * mm});
            skLineSegment(sketch, "E12.6.238", {"start": v(0, -13.96) * mm, "end": v(0, -13.46) * mm});
            skLineSegment(sketch, "E12.6.239", {"start": v(0, -13.96) * mm, "end": v(0, -13.46) * mm});
            skLineSegment(sketch, "E12.6.240", {"start": v(0, -13.96) * mm, "end": v(0, -13.46) * mm});
            skLineSegment(sketch, "E12.6.241", {"start": v(0, -13.96) * mm, "end": v(0, -13.46) * mm});
            skLineSegment(sketch, "E12.6.242", {"start": v(0, -13.96) * mm, "end": v(0, -13.46) * mm});
            skLineSegment(sketch, "E12.6.243", {"start": v(0, -13.96) * mm, "end": v(0, -13.46) * mm});
            skLineSegment(sketch, "E12.7.0", {"start": v(10.6, -13.3) * mm, "end": v(0, 0) * mm});
            skPoint(sketch, "E12.7.1", {"position": v(10.17, -13.62) * mm});
            skPoint(sketch, "E12.7.2", {"position": v(4.82, -16.3) * mm});
            skLineSegment(sketch, "E12.7.3", {"start": v(2.35, -16.84) * mm, "end": v(0, 0) * mm});
            skPoint(sketch, "E12.7.4", {"position": v(4.19, -14.14) * mm});
            skPoint(sketch, "E12.7.6", {"position": v(2.88, -16.75) * mm});
            skPoint(sketch, "E12.7.7", {"position": v(6.25, -10.83) * mm});
            skPoint(sketch, "E12.7.8", {"position": v(8.5, -14.72) * mm});
            skPoint(sketch, "E12.7.9", {"position": v(7.37, -12.77) * mm});
            skPoint(sketch, "E12.7.10", {"position": v(3.55, -11.99) * mm});
            skPoint(sketch, "E12.7.11", {"position": v(4.82, -16.3) * mm});
            skPoint(sketch, "E12.7.12", {"position": v(2.88, -16.75) * mm});
            skPoint(sketch, "E12.7.13", {"position": v(3.55, -11.99) * mm});
            skPoint(sketch, "E12.7.14", {"position": v(6.25, -10.83) * mm});
            skPoint(sketch, "E12.7.15", {"position": v(4.19, -14.14) * mm});
            skPoint(sketch, "E12.7.16", {"position": v(10.17, -13.62) * mm});
            skPoint(sketch, "E12.7.17", {"position": v(7.37, -12.77) * mm});
            skPoint(sketch, "E12.7.18", {"position": v(8.5, -14.72) * mm});
            skPoint(sketch, "E12.7.19", {"position": v(2.88, -16.75) * mm});
            skPoint(sketch, "E12.7.20", {"position": v(4.82, -16.3) * mm});
            skPoint(sketch, "E12.7.21", {"position": v(3.55, -11.99) * mm});
            skPoint(sketch, "E12.7.22", {"position": v(7.37, -12.77) * mm});
            skPoint(sketch, "E12.7.23", {"position": v(4.19, -14.14) * mm});
            skPoint(sketch, "E12.7.24", {"position": v(6.25, -10.83) * mm});
            skPoint(sketch, "E12.7.25", {"position": v(8.5, -14.72) * mm});
            skPoint(sketch, "E12.7.26", {"position": v(10.17, -13.62) * mm});
            skPoint(sketch, "E12.7.27", {"position": v(4.82, -16.3) * mm});
            skPoint(sketch, "E12.7.28", {"position": v(4.19, -14.14) * mm});
            skPoint(sketch, "E12.7.29", {"position": v(8.5, -14.72) * mm});
            skPoint(sketch, "E12.7.30", {"position": v(10.17, -13.62) * mm});
            skPoint(sketch, "E12.7.31", {"position": v(2.88, -16.75) * mm});
            skPoint(sketch, "E12.7.32", {"position": v(6.25, -10.83) * mm});
            skPoint(sketch, "E12.7.33", {"position": v(7.37, -12.77) * mm});
            skPoint(sketch, "E12.7.34", {"position": v(3.55, -11.99) * mm});
            skPoint(sketch, "E12.7.35", {"position": v(6.25, -10.83) * mm});
            skPoint(sketch, "E12.7.36", {"position": v(10.17, -13.62) * mm});
            skPoint(sketch, "E12.7.37", {"position": v(2.88, -16.75) * mm});
            skPoint(sketch, "E12.7.38", {"position": v(4.82, -16.3) * mm});
            skPoint(sketch, "E12.7.39", {"position": v(8.5, -14.72) * mm});
            skPoint(sketch, "E12.7.40", {"position": v(4.19, -14.14) * mm});
            skPoint(sketch, "E12.7.41", {"position": v(7.37, -12.77) * mm});
            skPoint(sketch, "E12.7.42", {"position": v(3.55, -11.99) * mm});
            skPoint(sketch, "E12.7.43", {"position": v(3.55, -11.99) * mm});
            skPoint(sketch, "E12.7.44", {"position": v(2.88, -16.75) * mm});
            skPoint(sketch, "E12.7.45", {"position": v(10.17, -13.62) * mm});
            skPoint(sketch, "E12.7.46", {"position": v(4.82, -16.3) * mm});
            skPoint(sketch, "E12.7.47", {"position": v(4.19, -14.14) * mm});
            skPoint(sketch, "E12.7.48", {"position": v(6.25, -10.83) * mm});
            skPoint(sketch, "E12.7.49", {"position": v(7.37, -12.77) * mm});
            skPoint(sketch, "E12.7.50", {"position": v(4.19, -14.14) * mm});
            skPoint(sketch, "E12.7.51", {"position": v(2.88, -16.75) * mm});
            skPoint(sketch, "E12.7.52", {"position": v(7.37, -12.77) * mm});
            skPoint(sketch, "E12.7.53", {"position": v(6.25, -10.83) * mm});
            skPoint(sketch, "E12.7.54", {"position": v(3.55, -11.99) * mm});
            skPoint(sketch, "E12.7.55", {"position": v(8.5, -14.72) * mm});
            skPoint(sketch, "E12.7.56", {"position": v(4.82, -16.3) * mm});
            skPoint(sketch, "E12.7.57", {"position": v(10.17, -13.62) * mm});
            skPoint(sketch, "E12.7.58", {"position": v(2.88, -16.75) * mm});
            skPoint(sketch, "E12.7.59", {"position": v(7.37, -12.77) * mm});
            skPoint(sketch, "E12.7.60", {"position": v(10.17, -13.62) * mm});
            skPoint(sketch, "E12.7.61", {"position": v(4.19, -14.14) * mm});
            skPoint(sketch, "E12.7.62", {"position": v(3.55, -11.99) * mm});
            skPoint(sketch, "E12.7.63", {"position": v(6.25, -10.83) * mm});
            skPoint(sketch, "E12.7.64", {"position": v(4.82, -16.3) * mm});
            skPoint(sketch, "E12.7.65", {"position": v(8.5, -14.72) * mm});
            skPoint(sketch, "E12.7.66", {"position": v(7.37, -12.77) * mm});
            skPoint(sketch, "E12.7.67", {"position": v(6.25, -10.83) * mm});
            skPoint(sketch, "E12.7.68", {"position": v(4.19, -14.14) * mm});
            skPoint(sketch, "E12.7.69", {"position": v(3.55, -11.99) * mm});
            skPoint(sketch, "E12.7.70", {"position": v(10.17, -13.62) * mm});
            skPoint(sketch, "E12.7.71", {"position": v(8.5, -14.72) * mm});
            skPoint(sketch, "E12.7.72", {"position": v(2.88, -16.75) * mm});
            skPoint(sketch, "E12.7.73", {"position": v(4.82, -16.3) * mm});
            skPoint(sketch, "E12.7.74", {"position": v(8.5, -14.72) * mm});
            skPoint(sketch, "E12.7.75", {"position": v(6.25, -10.83) * mm});
            skPoint(sketch, "E12.7.76", {"position": v(2.88, -16.75) * mm});
            skPoint(sketch, "E12.7.77", {"position": v(7.37, -12.77) * mm});
            skPoint(sketch, "E12.7.78", {"position": v(10.17, -13.62) * mm});
            skPoint(sketch, "E12.7.79", {"position": v(4.19, -14.14) * mm});
            skPoint(sketch, "E12.7.80", {"position": v(4.82, -16.3) * mm});
            skPoint(sketch, "E12.7.81", {"position": v(3.55, -11.99) * mm});
            skPoint(sketch, "E12.7.82", {"position": v(8.5, -14.72) * mm});
            skPoint(sketch, "E12.7.83", {"position": v(2.88, -16.75) * mm});
            skPoint(sketch, "E12.7.84", {"position": v(10.17, -13.62) * mm});
            skPoint(sketch, "E12.7.85", {"position": v(3.55, -11.99) * mm});
            skPoint(sketch, "E12.7.86", {"position": v(7.37, -12.77) * mm});
            skPoint(sketch, "E12.7.87", {"position": v(4.19, -14.14) * mm});
            skPoint(sketch, "E12.7.88", {"position": v(6.25, -10.83) * mm});
            skPoint(sketch, "E12.7.89", {"position": v(10.17, -13.62) * mm});
            skPoint(sketch, "E12.7.90", {"position": v(6.25, -10.83) * mm});
            skPoint(sketch, "E12.7.91", {"position": v(3.55, -11.99) * mm});
            skPoint(sketch, "E12.7.92", {"position": v(7.38, -12.77) * mm});
            skPoint(sketch, "E12.7.93", {"position": v(4.19, -14.14) * mm});
            skPoint(sketch, "E12.7.94", {"position": v(2.88, -16.75) * mm});
            skPoint(sketch, "E12.7.95", {"position": v(4.19, -14.14) * mm});
            skPoint(sketch, "E12.7.96", {"position": v(3.55, -11.99) * mm});
            skPoint(sketch, "E12.7.97", {"position": v(7.37, -12.77) * mm});
            skPoint(sketch, "E12.7.98", {"position": v(6.25, -10.83) * mm});
            skPoint(sketch, "E12.7.99", {"position": v(10.17, -13.62) * mm});
            skPoint(sketch, "E12.7.100", {"position": v(2.88, -16.75) * mm});
            skArc(sketch, "E12.7.101", {"start": v(3.83, -14.85) * mm, "mid": v(4.04, -14.13) * mm, "end": v(3.96, -13.39) * mm});
            skArc(sketch, "E12.7.102", {"start": v(4.43, -11.7) * mm, "mid": v(3.88, -12.18) * mm, "end": v(3.82, -12.9) * mm});
            skArc(sketch, "E12.7.103", {"start": v(6.73, -11.66) * mm, "mid": v(6.16, -11.2) * mm, "end": v(5.43, -11.26) * mm});
            skArc(sketch, "E12.7.104", {"start": v(3.83, -14.85) * mm, "mid": v(4.04, -14.13) * mm, "end": v(3.96, -13.39) * mm});
            skArc(sketch, "E12.7.105", {"start": v(2.35, -16.84) * mm, "mid": v(2.8, -16.66) * mm, "end": v(3.1, -16.3) * mm});
            skArc(sketch, "E12.7.106", {"start": v(4.43, -11.7) * mm, "mid": v(3.88, -12.18) * mm, "end": v(3.82, -12.9) * mm});
            skArc(sketch, "E12.7.107", {"start": v(6.73, -11.66) * mm, "mid": v(6.16, -11.2) * mm, "end": v(5.43, -11.26) * mm});
            skArc(sketch, "E12.7.108", {"start": v(9.68, -13.47) * mm, "mid": v(10.16, -13.5) * mm, "end": v(10.6, -13.3) * mm});
            skArc(sketch, "E12.7.109", {"start": v(4.43, -11.7) * mm, "mid": v(3.88, -12.18) * mm, "end": v(3.82, -12.9) * mm});
            skArc(sketch, "E12.7.110", {"start": v(6.73, -11.66) * mm, "mid": v(6.16, -11.2) * mm, "end": v(5.43, -11.26) * mm});
            skArc(sketch, "E12.7.111", {"start": v(3.83, -14.85) * mm, "mid": v(4.04, -14.13) * mm, "end": v(3.96, -13.39) * mm});
            skArc(sketch, "E12.7.112", {"start": v(2.35, -16.84) * mm, "mid": v(2.8, -16.66) * mm, "end": v(3.1, -16.3) * mm});
            skArc(sketch, "E12.7.113", {"start": v(9.68, -13.47) * mm, "mid": v(10.16, -13.5) * mm, "end": v(10.6, -13.3) * mm});
            skArc(sketch, "E12.7.114", {"start": v(4.43, -11.7) * mm, "mid": v(3.88, -12.18) * mm, "end": v(3.82, -12.9) * mm});
            skArc(sketch, "E12.7.115", {"start": v(9.68, -13.47) * mm, "mid": v(10.16, -13.5) * mm, "end": v(10.6, -13.3) * mm});
            skArc(sketch, "E12.7.116", {"start": v(6.73, -11.66) * mm, "mid": v(6.16, -11.2) * mm, "end": v(5.43, -11.26) * mm});
            skArc(sketch, "E12.7.117", {"start": v(3.83, -14.85) * mm, "mid": v(4.04, -14.13) * mm, "end": v(3.96, -13.39) * mm});
            skArc(sketch, "E12.7.118", {"start": v(2.35, -16.84) * mm, "mid": v(2.8, -16.66) * mm, "end": v(3.1, -16.3) * mm});
            skArc(sketch, "E12.7.119", {"start": v(9.68, -13.47) * mm, "mid": v(10.16, -13.5) * mm, "end": v(10.6, -13.3) * mm});
            skArc(sketch, "E12.7.120", {"start": v(6.73, -11.66) * mm, "mid": v(6.16, -11.2) * mm, "end": v(5.43, -11.26) * mm});
            skArc(sketch, "E12.7.121", {"start": v(4.43, -11.7) * mm, "mid": v(3.88, -12.18) * mm, "end": v(3.82, -12.9) * mm});
            skArc(sketch, "E12.7.122", {"start": v(3.83, -14.85) * mm, "mid": v(4.04, -14.13) * mm, "end": v(3.96, -13.39) * mm});
            skArc(sketch, "E12.7.123", {"start": v(2.35, -16.84) * mm, "mid": v(2.8, -16.66) * mm, "end": v(3.1, -16.3) * mm});
            skArc(sketch, "E12.7.124", {"start": v(9.68, -13.47) * mm, "mid": v(10.16, -13.5) * mm, "end": v(10.6, -13.3) * mm});
            skArc(sketch, "E12.7.125", {"start": v(4.43, -11.7) * mm, "mid": v(3.88, -12.18) * mm, "end": v(3.82, -12.9) * mm});
            skArc(sketch, "E12.7.126", {"start": v(6.73, -11.66) * mm, "mid": v(6.16, -11.2) * mm, "end": v(5.43, -11.26) * mm});
            skArc(sketch, "E12.7.127", {"start": v(3.83, -14.85) * mm, "mid": v(4.04, -14.13) * mm, "end": v(3.96, -13.39) * mm});
            skArc(sketch, "E12.7.128", {"start": v(2.35, -16.84) * mm, "mid": v(2.8, -16.66) * mm, "end": v(3.1, -16.3) * mm});
            skArc(sketch, "E12.7.129", {"start": v(4.43, -11.7) * mm, "mid": v(3.88, -12.18) * mm, "end": v(3.82, -12.9) * mm});
            skArc(sketch, "E12.7.130", {"start": v(9.68, -13.47) * mm, "mid": v(10.16, -13.5) * mm, "end": v(10.6, -13.3) * mm});
            skArc(sketch, "E12.7.131", {"start": v(6.73, -11.66) * mm, "mid": v(6.16, -11.2) * mm, "end": v(5.43, -11.26) * mm});
            skArc(sketch, "E12.7.132", {"start": v(2.35, -16.84) * mm, "mid": v(2.8, -16.66) * mm, "end": v(3.1, -16.3) * mm});
            skArc(sketch, "E12.7.133", {"start": v(3.83, -14.85) * mm, "mid": v(4.04, -14.13) * mm, "end": v(3.96, -13.39) * mm});
            skArc(sketch, "E12.7.134", {"start": v(3.83, -14.85) * mm, "mid": v(4.04, -14.13) * mm, "end": v(3.96, -13.39) * mm});
            skArc(sketch, "E12.7.135", {"start": v(2.35, -16.84) * mm, "mid": v(2.8, -16.66) * mm, "end": v(3.1, -16.3) * mm});
            skArc(sketch, "E12.7.136", {"start": v(4.43, -11.7) * mm, "mid": v(3.88, -12.18) * mm, "end": v(3.82, -12.9) * mm});
            skArc(sketch, "E12.7.137", {"start": v(9.68, -13.47) * mm, "mid": v(10.16, -13.5) * mm, "end": v(10.6, -13.3) * mm});
            skArc(sketch, "E12.7.138", {"start": v(6.73, -11.66) * mm, "mid": v(6.16, -11.2) * mm, "end": v(5.43, -11.26) * mm});
            skArc(sketch, "E12.7.139", {"start": v(4.43, -11.7) * mm, "mid": v(3.88, -12.18) * mm, "end": v(3.82, -12.9) * mm});
            skArc(sketch, "E12.7.140", {"start": v(6.73, -11.66) * mm, "mid": v(6.16, -11.2) * mm, "end": v(5.43, -11.26) * mm});
            skArc(sketch, "E12.7.141", {"start": v(3.83, -14.85) * mm, "mid": v(4.04, -14.13) * mm, "end": v(3.96, -13.39) * mm});
            skArc(sketch, "E12.7.142", {"start": v(2.35, -16.84) * mm, "mid": v(2.8, -16.66) * mm, "end": v(3.1, -16.3) * mm});
            skArc(sketch, "E12.7.143", {"start": v(9.68, -13.47) * mm, "mid": v(10.16, -13.5) * mm, "end": v(10.6, -13.3) * mm});
            skArc(sketch, "E12.7.144", {"start": v(9.68, -13.47) * mm, "mid": v(10.16, -13.5) * mm, "end": v(10.6, -13.3) * mm});
            skArc(sketch, "E12.7.145", {"start": v(3.83, -14.85) * mm, "mid": v(4.04, -14.13) * mm, "end": v(3.96, -13.39) * mm});
            skArc(sketch, "E12.7.146", {"start": v(4.43, -11.7) * mm, "mid": v(3.88, -12.18) * mm, "end": v(3.82, -12.9) * mm});
            skArc(sketch, "E12.7.147", {"start": v(6.73, -11.66) * mm, "mid": v(6.16, -11.2) * mm, "end": v(5.43, -11.26) * mm});
            skArc(sketch, "E12.7.148", {"start": v(2.35, -16.84) * mm, "mid": v(2.8, -16.66) * mm, "end": v(3.1, -16.3) * mm});
            skArc(sketch, "E12.7.149", {"start": v(4.43, -11.7) * mm, "mid": v(3.88, -12.18) * mm, "end": v(3.82, -12.9) * mm});
            skArc(sketch, "E12.7.150", {"start": v(9.68, -13.47) * mm, "mid": v(10.16, -13.5) * mm, "end": v(10.6, -13.3) * mm});
            skArc(sketch, "E12.7.151", {"start": v(6.73, -11.66) * mm, "mid": v(6.16, -11.2) * mm, "end": v(5.43, -11.26) * mm});
            skArc(sketch, "E12.7.152", {"start": v(2.35, -16.84) * mm, "mid": v(2.8, -16.66) * mm, "end": v(3.1, -16.3) * mm});
            skArc(sketch, "E12.7.153", {"start": v(3.83, -14.85) * mm, "mid": v(4.04, -14.13) * mm, "end": v(3.96, -13.39) * mm});
            skArc(sketch, "E12.7.154", {"start": v(9.68, -13.47) * mm, "mid": v(10.16, -13.5) * mm, "end": v(10.6, -13.3) * mm});
            skArc(sketch, "E12.7.155", {"start": v(2.35, -16.84) * mm, "mid": v(2.8, -16.66) * mm, "end": v(3.1, -16.3) * mm});
            skArc(sketch, "E12.7.156", {"start": v(4.43, -11.7) * mm, "mid": v(3.88, -12.18) * mm, "end": v(3.82, -12.9) * mm});
            skArc(sketch, "E12.7.157", {"start": v(3.83, -14.85) * mm, "mid": v(4.04, -14.13) * mm, "end": v(3.96, -13.39) * mm});
            skArc(sketch, "E12.7.158", {"start": v(6.73, -11.66) * mm, "mid": v(6.16, -11.2) * mm, "end": v(5.43, -11.26) * mm});
            skArc(sketch, "E12.7.159", {"start": v(9.68, -13.47) * mm, "mid": v(10.16, -13.5) * mm, "end": v(10.6, -13.3) * mm});
            skArc(sketch, "E12.7.160", {"start": v(6.73, -11.66) * mm, "mid": v(6.16, -11.2) * mm, "end": v(5.43, -11.26) * mm});
            skArc(sketch, "E12.7.161", {"start": v(4.43, -11.7) * mm, "mid": v(3.88, -12.18) * mm, "end": v(3.82, -12.9) * mm});
            skArc(sketch, "E12.7.162", {"start": v(3.83, -14.85) * mm, "mid": v(4.04, -14.13) * mm, "end": v(3.96, -13.39) * mm});
            skArc(sketch, "E12.7.163", {"start": v(2.35, -16.84) * mm, "mid": v(2.8, -16.66) * mm, "end": v(3.1, -16.3) * mm});
            skArc(sketch, "E12.7.164", {"start": v(6.98, -12.09) * mm, "mid": v(7.47, -12.66) * mm, "end": v(8.13, -13) * mm});
            skArc(sketch, "E12.7.165", {"start": v(4.43, -11.7) * mm, "mid": v(4.93, -11.49) * mm, "end": v(5.43, -11.26) * mm});
            skArc(sketch, "E12.7.166", {"start": v(2.35, -16.84) * mm, "mid": v(2.8, -16.66) * mm, "end": v(3.1, -16.3) * mm});
            skLineSegment(sketch, "E12.7.167", {"start": v(3.83, -14.85) * mm, "end": v(3.1, -16.3) * mm});
            skLineSegment(sketch, "E12.7.168", {"start": v(8.13, -13) * mm, "end": v(9.68, -13.47) * mm});
            skArc(sketch, "E12.7.169", {"start": v(9.68, -13.47) * mm, "mid": v(10.16, -13.5) * mm, "end": v(10.6, -13.3) * mm});
            skLineSegment(sketch, "E12.7.170", {"start": v(8.13, -13) * mm, "end": v(9.68, -13.47) * mm});
            skLineSegment(sketch, "E12.7.171", {"start": v(3.83, -14.85) * mm, "end": v(3.1, -16.3) * mm});
            skLineSegment(sketch, "E12.7.172", {"start": v(3.82, -12.9) * mm, "end": v(3.96, -13.39) * mm});
            skArc(sketch, "E12.7.173", {"start": v(4.43, -11.7) * mm, "mid": v(4.93, -11.49) * mm, "end": v(5.43, -11.26) * mm});
            skArc(sketch, "E12.7.174", {"start": v(6.98, -12.09) * mm, "mid": v(7.47, -12.66) * mm, "end": v(8.13, -13) * mm});
            skLineSegment(sketch, "E12.7.175", {"start": v(3.83, -14.85) * mm, "end": v(3.1, -16.3) * mm});
            skArc(sketch, "E12.7.176", {"start": v(6.98, -12.09) * mm, "mid": v(7.47, -12.66) * mm, "end": v(8.13, -13) * mm});
            skLineSegment(sketch, "E12.7.177", {"start": v(8.13, -13) * mm, "end": v(9.68, -13.47) * mm});
            skLineSegment(sketch, "E12.7.178", {"start": v(3.82, -12.9) * mm, "end": v(3.96, -13.39) * mm});
            skArc(sketch, "E12.7.179", {"start": v(4.43, -11.7) * mm, "mid": v(4.93, -11.49) * mm, "end": v(5.43, -11.26) * mm});
            skLineSegment(sketch, "E12.7.180", {"start": v(8.13, -13) * mm, "end": v(9.68, -13.47) * mm});
            skArc(sketch, "E12.7.181", {"start": v(6.98, -12.09) * mm, "mid": v(7.47, -12.66) * mm, "end": v(8.13, -13) * mm});
            skArc(sketch, "E12.7.182", {"start": v(4.43, -11.7) * mm, "mid": v(4.93, -11.49) * mm, "end": v(5.43, -11.26) * mm});
            skLineSegment(sketch, "E12.7.183", {"start": v(3.82, -12.9) * mm, "end": v(3.96, -13.39) * mm});
            skLineSegment(sketch, "E12.7.184", {"start": v(3.83, -14.85) * mm, "end": v(3.1, -16.3) * mm});
            skArc(sketch, "E12.7.185", {"start": v(6.98, -12.09) * mm, "mid": v(7.47, -12.66) * mm, "end": v(8.13, -13) * mm});
            skLineSegment(sketch, "E12.7.186", {"start": v(8.13, -13) * mm, "end": v(9.68, -13.47) * mm});
            skLineSegment(sketch, "E12.7.187", {"start": v(3.83, -14.85) * mm, "end": v(3.1, -16.3) * mm});
            skArc(sketch, "E12.7.188", {"start": v(4.43, -11.7) * mm, "mid": v(4.93, -11.49) * mm, "end": v(5.43, -11.26) * mm});
            skLineSegment(sketch, "E12.7.189", {"start": v(3.82, -12.9) * mm, "end": v(3.96, -13.39) * mm});
            skArc(sketch, "E12.7.190", {"start": v(6.98, -12.09) * mm, "mid": v(7.47, -12.66) * mm, "end": v(8.13, -13) * mm});
            skLineSegment(sketch, "E12.7.191", {"start": v(3.83, -14.85) * mm, "end": v(3.1, -16.3) * mm});
            skArc(sketch, "E12.7.192", {"start": v(4.43, -11.7) * mm, "mid": v(4.93, -11.49) * mm, "end": v(5.43, -11.26) * mm});
            skLineSegment(sketch, "E12.7.193", {"start": v(8.13, -13) * mm, "end": v(9.68, -13.47) * mm});
            skLineSegment(sketch, "E12.7.194", {"start": v(3.82, -12.9) * mm, "end": v(3.96, -13.39) * mm});
            skLineSegment(sketch, "E12.7.195", {"start": v(8.13, -13) * mm, "end": v(9.68, -13.47) * mm});
            skArc(sketch, "E12.7.196", {"start": v(4.43, -11.7) * mm, "mid": v(4.93, -11.49) * mm, "end": v(5.43, -11.26) * mm});
            skLineSegment(sketch, "E12.7.197", {"start": v(3.83, -14.85) * mm, "end": v(3.1, -16.3) * mm});
            skArc(sketch, "E12.7.198", {"start": v(6.98, -12.09) * mm, "mid": v(7.47, -12.66) * mm, "end": v(8.13, -13) * mm});
            skLineSegment(sketch, "E12.7.199", {"start": v(3.82, -12.9) * mm, "end": v(3.96, -13.39) * mm});
            skLineSegment(sketch, "E12.7.200", {"start": v(3.83, -14.85) * mm, "end": v(3.1, -16.3) * mm});
            skArc(sketch, "E12.7.201", {"start": v(4.43, -11.7) * mm, "mid": v(4.93, -11.49) * mm, "end": v(5.43, -11.26) * mm});
            skLineSegment(sketch, "E12.7.202", {"start": v(6.98, -12.09) * mm, "end": v(6.73, -11.66) * mm});
            skLineSegment(sketch, "E12.7.203", {"start": v(8.13, -13) * mm, "end": v(9.68, -13.47) * mm});
            skArc(sketch, "E12.7.204", {"start": v(6.98, -12.09) * mm, "mid": v(7.47, -12.66) * mm, "end": v(8.13, -13) * mm});
            skLineSegment(sketch, "E12.7.205", {"start": v(3.82, -12.9) * mm, "end": v(3.96, -13.39) * mm});
            skLineSegment(sketch, "E12.7.206", {"start": v(6.98, -12.09) * mm, "end": v(6.73, -11.66) * mm});
            skLineSegment(sketch, "E12.7.207", {"start": v(3.82, -12.9) * mm, "end": v(3.96, -13.39) * mm});
            skArc(sketch, "E12.7.208", {"start": v(6.98, -12.09) * mm, "mid": v(7.47, -12.66) * mm, "end": v(8.13, -13) * mm});
            skLineSegment(sketch, "E12.7.209", {"start": v(3.83, -14.85) * mm, "end": v(3.1, -16.3) * mm});
            skArc(sketch, "E12.7.210", {"start": v(4.43, -11.7) * mm, "mid": v(4.93, -11.49) * mm, "end": v(5.43, -11.26) * mm});
            skLineSegment(sketch, "E12.7.211", {"start": v(8.13, -13) * mm, "end": v(9.68, -13.47) * mm});
            skArc(sketch, "E12.7.212", {"start": v(4.43, -11.7) * mm, "mid": v(4.93, -11.49) * mm, "end": v(5.43, -11.26) * mm});
            skLineSegment(sketch, "E12.7.213", {"start": v(8.13, -13) * mm, "end": v(9.68, -13.47) * mm});
            skLineSegment(sketch, "E12.7.214", {"start": v(3.83, -14.85) * mm, "end": v(3.1, -16.3) * mm});
            skLineSegment(sketch, "E12.7.215", {"start": v(6.98, -12.09) * mm, "end": v(6.73, -11.66) * mm});
            skArc(sketch, "E12.7.216", {"start": v(6.98, -12.09) * mm, "mid": v(7.47, -12.66) * mm, "end": v(8.13, -13) * mm});
            skLineSegment(sketch, "E12.7.217", {"start": v(3.82, -12.9) * mm, "end": v(3.96, -13.39) * mm});
            skLineSegment(sketch, "E12.7.218", {"start": v(8.13, -13) * mm, "end": v(9.68, -13.47) * mm});
            skArc(sketch, "E12.7.219", {"start": v(6.98, -12.09) * mm, "mid": v(7.47, -12.66) * mm, "end": v(8.13, -13) * mm});
            skLineSegment(sketch, "E12.7.220", {"start": v(3.83, -14.85) * mm, "end": v(3.1, -16.3) * mm});
            skLineSegment(sketch, "E12.7.221", {"start": v(3.82, -12.9) * mm, "end": v(3.96, -13.39) * mm});
            skArc(sketch, "E12.7.222", {"start": v(4.43, -11.7) * mm, "mid": v(4.93, -11.49) * mm, "end": v(5.43, -11.26) * mm});
            skLineSegment(sketch, "E12.7.223", {"start": v(6.98, -12.09) * mm, "end": v(6.73, -11.66) * mm});
            skLineSegment(sketch, "E12.7.224", {"start": v(8.13, -13) * mm, "end": v(9.68, -13.47) * mm});
            skLineSegment(sketch, "E12.7.225", {"start": v(3.83, -14.85) * mm, "end": v(3.1, -16.3) * mm});
            skLineSegment(sketch, "E12.7.226", {"start": v(6.98, -12.09) * mm, "end": v(6.73, -11.66) * mm});
            skArc(sketch, "E12.7.227", {"start": v(6.98, -12.09) * mm, "mid": v(7.47, -12.66) * mm, "end": v(8.13, -13) * mm});
            skLineSegment(sketch, "E12.7.228", {"start": v(3.82, -12.9) * mm, "end": v(3.96, -13.39) * mm});
            skArc(sketch, "E12.7.229", {"start": v(4.43, -11.7) * mm, "mid": v(4.93, -11.49) * mm, "end": v(5.43, -11.26) * mm});
            skArc(sketch, "E12.7.230", {"start": v(4.43, -11.7) * mm, "mid": v(4.93, -11.49) * mm, "end": v(5.43, -11.26) * mm});
            skLineSegment(sketch, "E12.7.231", {"start": v(3.82, -12.9) * mm, "end": v(3.96, -13.39) * mm});
            skLineSegment(sketch, "E12.7.232", {"start": v(8.13, -13) * mm, "end": v(9.68, -13.47) * mm});
            skLineSegment(sketch, "E12.7.233", {"start": v(6.98, -12.09) * mm, "end": v(6.73, -11.66) * mm});
            skArc(sketch, "E12.7.234", {"start": v(6.98, -12.09) * mm, "mid": v(7.47, -12.66) * mm, "end": v(8.13, -13) * mm});
            skLineSegment(sketch, "E12.7.235", {"start": v(3.83, -14.85) * mm, "end": v(3.1, -16.3) * mm});
            skLineSegment(sketch, "E12.7.236", {"start": v(3.82, -12.9) * mm, "end": v(3.96, -13.39) * mm});
            skLineSegment(sketch, "E12.7.237", {"start": v(6.98, -12.09) * mm, "end": v(6.73, -11.66) * mm});
            skLineSegment(sketch, "E12.7.238", {"start": v(6.98, -12.09) * mm, "end": v(6.73, -11.66) * mm});
            skLineSegment(sketch, "E12.7.239", {"start": v(6.98, -12.09) * mm, "end": v(6.73, -11.66) * mm});
            skLineSegment(sketch, "E12.7.240", {"start": v(6.98, -12.09) * mm, "end": v(6.73, -11.66) * mm});
            skLineSegment(sketch, "E12.7.241", {"start": v(6.98, -12.09) * mm, "end": v(6.73, -11.66) * mm});
            skLineSegment(sketch, "E12.7.242", {"start": v(6.98, -12.09) * mm, "end": v(6.73, -11.66) * mm});
            skLineSegment(sketch, "E12.7.243", {"start": v(6.98, -12.09) * mm, "end": v(6.73, -11.66) * mm});
            skLineSegment(sketch, "E12.8.0", {"start": v(15.82, -6.22) * mm, "end": v(0, 0) * mm});
            skPoint(sketch, "E12.8.1", {"position": v(15.62, -6.71) * mm});
            skPoint(sketch, "E12.8.2", {"position": v(12.33, -11.7) * mm});
            skLineSegment(sketch, "E12.8.3", {"start": v(10.46, -13.4) * mm, "end": v(0, 0) * mm});
            skPoint(sketch, "E12.8.4", {"position": v(10.7, -10.16) * mm});
            skPoint(sketch, "E12.8.6", {"position": v(10.87, -13.07) * mm});
            skPoint(sketch, "E12.8.7", {"position": v(10.83, -6.25) * mm});
            skPoint(sketch, "E12.8.8", {"position": v(14.72, -8.5) * mm});
            skPoint(sketch, "E12.8.9", {"position": v(12.77, -7.38) * mm});
            skPoint(sketch, "E12.8.10", {"position": v(9.07, -8.6) * mm});
            skPoint(sketch, "E12.8.11", {"position": v(12.33, -11.7) * mm});
            skPoint(sketch, "E12.8.12", {"position": v(10.87, -13.07) * mm});
            skPoint(sketch, "E12.8.13", {"position": v(9.07, -8.6) * mm});
            skPoint(sketch, "E12.8.14", {"position": v(10.83, -6.25) * mm});
            skPoint(sketch, "E12.8.15", {"position": v(10.7, -10.16) * mm});
            skPoint(sketch, "E12.8.16", {"position": v(15.62, -6.71) * mm});
            skPoint(sketch, "E12.8.17", {"position": v(12.77, -7.38) * mm});
            skPoint(sketch, "E12.8.18", {"position": v(14.72, -8.5) * mm});
            skPoint(sketch, "E12.8.19", {"position": v(10.87, -13.07) * mm});
            skPoint(sketch, "E12.8.20", {"position": v(12.33, -11.7) * mm});
            skPoint(sketch, "E12.8.21", {"position": v(9.07, -8.6) * mm});
            skPoint(sketch, "E12.8.22", {"position": v(12.77, -7.38) * mm});
            skPoint(sketch, "E12.8.23", {"position": v(10.7, -10.16) * mm});
            skPoint(sketch, "E12.8.24", {"position": v(10.83, -6.25) * mm});
            skPoint(sketch, "E12.8.25", {"position": v(14.72, -8.5) * mm});
            skPoint(sketch, "E12.8.26", {"position": v(15.62, -6.71) * mm});
            skPoint(sketch, "E12.8.27", {"position": v(12.33, -11.7) * mm});
            skPoint(sketch, "E12.8.28", {"position": v(10.7, -10.16) * mm});
            skPoint(sketch, "E12.8.29", {"position": v(14.72, -8.5) * mm});
            skPoint(sketch, "E12.8.30", {"position": v(15.62, -6.71) * mm});
            skPoint(sketch, "E12.8.31", {"position": v(10.87, -13.07) * mm});
            skPoint(sketch, "E12.8.32", {"position": v(10.83, -6.25) * mm});
            skPoint(sketch, "E12.8.33", {"position": v(12.77, -7.38) * mm});
            skPoint(sketch, "E12.8.34", {"position": v(9.07, -8.6) * mm});
            skPoint(sketch, "E12.8.35", {"position": v(10.83, -6.25) * mm});
            skPoint(sketch, "E12.8.36", {"position": v(15.62, -6.71) * mm});
            skPoint(sketch, "E12.8.37", {"position": v(10.87, -13.07) * mm});
            skPoint(sketch, "E12.8.38", {"position": v(12.33, -11.7) * mm});
            skPoint(sketch, "E12.8.39", {"position": v(14.72, -8.5) * mm});
            skPoint(sketch, "E12.8.40", {"position": v(10.7, -10.16) * mm});
            skPoint(sketch, "E12.8.41", {"position": v(12.77, -7.38) * mm});
            skPoint(sketch, "E12.8.42", {"position": v(9.07, -8.6) * mm});
            skPoint(sketch, "E12.8.43", {"position": v(9.07, -8.6) * mm});
            skPoint(sketch, "E12.8.44", {"position": v(10.87, -13.07) * mm});
            skPoint(sketch, "E12.8.45", {"position": v(15.62, -6.71) * mm});
            skPoint(sketch, "E12.8.46", {"position": v(12.33, -11.7) * mm});
            skPoint(sketch, "E12.8.47", {"position": v(10.7, -10.16) * mm});
            skPoint(sketch, "E12.8.48", {"position": v(10.83, -6.25) * mm});
            skPoint(sketch, "E12.8.49", {"position": v(12.77, -7.38) * mm});
            skPoint(sketch, "E12.8.50", {"position": v(10.7, -10.16) * mm});
            skPoint(sketch, "E12.8.51", {"position": v(10.87, -13.07) * mm});
            skPoint(sketch, "E12.8.52", {"position": v(12.77, -7.38) * mm});
            skPoint(sketch, "E12.8.53", {"position": v(10.83, -6.25) * mm});
            skPoint(sketch, "E12.8.54", {"position": v(9.07, -8.6) * mm});
            skPoint(sketch, "E12.8.55", {"position": v(14.72, -8.5) * mm});
            skPoint(sketch, "E12.8.56", {"position": v(12.33, -11.7) * mm});
            skPoint(sketch, "E12.8.57", {"position": v(15.62, -6.71) * mm});
            skPoint(sketch, "E12.8.58", {"position": v(10.87, -13.07) * mm});
            skPoint(sketch, "E12.8.59", {"position": v(12.77, -7.38) * mm});
            skPoint(sketch, "E12.8.60", {"position": v(15.62, -6.71) * mm});
            skPoint(sketch, "E12.8.61", {"position": v(10.7, -10.16) * mm});
            skPoint(sketch, "E12.8.62", {"position": v(9.07, -8.6) * mm});
            skPoint(sketch, "E12.8.63", {"position": v(10.83, -6.25) * mm});
            skPoint(sketch, "E12.8.64", {"position": v(12.33, -11.7) * mm});
            skPoint(sketch, "E12.8.65", {"position": v(14.72, -8.5) * mm});
            skPoint(sketch, "E12.8.66", {"position": v(12.77, -7.38) * mm});
            skPoint(sketch, "E12.8.67", {"position": v(10.83, -6.25) * mm});
            skPoint(sketch, "E12.8.68", {"position": v(10.7, -10.16) * mm});
            skPoint(sketch, "E12.8.69", {"position": v(9.07, -8.6) * mm});
            skPoint(sketch, "E12.8.70", {"position": v(15.62, -6.71) * mm});
            skPoint(sketch, "E12.8.71", {"position": v(14.72, -8.5) * mm});
            skPoint(sketch, "E12.8.72", {"position": v(10.87, -13.07) * mm});
            skPoint(sketch, "E12.8.73", {"position": v(12.33, -11.7) * mm});
            skPoint(sketch, "E12.8.74", {"position": v(14.72, -8.5) * mm});
            skPoint(sketch, "E12.8.75", {"position": v(10.83, -6.25) * mm});
            skPoint(sketch, "E12.8.76", {"position": v(10.87, -13.07) * mm});
            skPoint(sketch, "E12.8.77", {"position": v(12.77, -7.38) * mm});
            skPoint(sketch, "E12.8.78", {"position": v(15.62, -6.71) * mm});
            skPoint(sketch, "E12.8.79", {"position": v(10.7, -10.16) * mm});
            skPoint(sketch, "E12.8.80", {"position": v(12.33, -11.7) * mm});
            skPoint(sketch, "E12.8.81", {"position": v(9.07, -8.6) * mm});
            skPoint(sketch, "E12.8.82", {"position": v(14.72, -8.5) * mm});
            skPoint(sketch, "E12.8.83", {"position": v(10.87, -13.07) * mm});
            skPoint(sketch, "E12.8.84", {"position": v(15.62, -6.71) * mm});
            skPoint(sketch, "E12.8.85", {"position": v(9.07, -8.6) * mm});
            skPoint(sketch, "E12.8.86", {"position": v(12.77, -7.38) * mm});
            skPoint(sketch, "E12.8.87", {"position": v(10.7, -10.16) * mm});
            skPoint(sketch, "E12.8.88", {"position": v(10.83, -6.25) * mm});
            skPoint(sketch, "E12.8.89", {"position": v(15.62, -6.71) * mm});
            skPoint(sketch, "E12.8.90", {"position": v(10.83, -6.25) * mm});
            skPoint(sketch, "E12.8.91", {"position": v(9.07, -8.6) * mm});
            skPoint(sketch, "E12.8.92", {"position": v(12.77, -7.38) * mm});
            skPoint(sketch, "E12.8.93", {"position": v(10.7, -10.16) * mm});
            skPoint(sketch, "E12.8.94", {"position": v(10.87, -13.07) * mm});
            skPoint(sketch, "E12.8.95", {"position": v(10.7, -10.16) * mm});
            skPoint(sketch, "E12.8.96", {"position": v(9.07, -8.6) * mm});
            skPoint(sketch, "E12.8.97", {"position": v(12.77, -7.38) * mm});
            skPoint(sketch, "E12.8.98", {"position": v(10.83, -6.25) * mm});
            skPoint(sketch, "E12.8.99", {"position": v(15.62, -6.71) * mm});
            skPoint(sketch, "E12.8.100", {"position": v(10.87, -13.07) * mm});
            skArc(sketch, "E12.8.101", {"start": v(10.74, -10.94) * mm, "mid": v(10.56, -10.22) * mm, "end": v(10.12, -9.61) * mm});
            skArc(sketch, "E12.8.102", {"start": v(9.68, -7.91) * mm, "mid": v(9.45, -8.6) * mm, "end": v(9.76, -9.27) * mm});
            skArc(sketch, "E12.8.103", {"start": v(11.66, -6.73) * mm, "mid": v(10.94, -6.62) * mm, "end": v(10.33, -7.03) * mm});
            skArc(sketch, "E12.8.104", {"start": v(10.74, -10.94) * mm, "mid": v(10.56, -10.22) * mm, "end": v(10.12, -9.61) * mm});
            skArc(sketch, "E12.8.105", {"start": v(10.46, -13.4) * mm, "mid": v(10.75, -13.03) * mm, "end": v(10.84, -12.56) * mm});
            skArc(sketch, "E12.8.106", {"start": v(9.68, -7.91) * mm, "mid": v(9.45, -8.6) * mm, "end": v(9.76, -9.27) * mm});
            skArc(sketch, "E12.8.107", {"start": v(11.66, -6.73) * mm, "mid": v(10.94, -6.62) * mm, "end": v(10.33, -7.03) * mm});
            skArc(sketch, "E12.8.108", {"start": v(15.12, -6.83) * mm, "mid": v(15.54, -6.61) * mm, "end": v(15.82, -6.22) * mm});
            skArc(sketch, "E12.8.109", {"start": v(9.68, -7.91) * mm, "mid": v(9.45, -8.6) * mm, "end": v(9.76, -9.27) * mm});
            skArc(sketch, "E12.8.110", {"start": v(11.66, -6.73) * mm, "mid": v(10.94, -6.62) * mm, "end": v(10.33, -7.03) * mm});
            skArc(sketch, "E12.8.111", {"start": v(10.74, -10.94) * mm, "mid": v(10.56, -10.22) * mm, "end": v(10.12, -9.61) * mm});
            skArc(sketch, "E12.8.112", {"start": v(10.46, -13.4) * mm, "mid": v(10.75, -13.03) * mm, "end": v(10.84, -12.56) * mm});
            skArc(sketch, "E12.8.113", {"start": v(15.12, -6.83) * mm, "mid": v(15.54, -6.61) * mm, "end": v(15.82, -6.22) * mm});
            skArc(sketch, "E12.8.114", {"start": v(9.68, -7.91) * mm, "mid": v(9.45, -8.6) * mm, "end": v(9.76, -9.27) * mm});
            skArc(sketch, "E12.8.115", {"start": v(15.12, -6.83) * mm, "mid": v(15.54, -6.61) * mm, "end": v(15.82, -6.22) * mm});
            skArc(sketch, "E12.8.116", {"start": v(11.66, -6.73) * mm, "mid": v(10.94, -6.62) * mm, "end": v(10.33, -7.03) * mm});
            skArc(sketch, "E12.8.117", {"start": v(10.74, -10.94) * mm, "mid": v(10.56, -10.22) * mm, "end": v(10.12, -9.61) * mm});
            skArc(sketch, "E12.8.118", {"start": v(10.46, -13.4) * mm, "mid": v(10.75, -13.03) * mm, "end": v(10.84, -12.56) * mm});
            skArc(sketch, "E12.8.119", {"start": v(15.12, -6.83) * mm, "mid": v(15.54, -6.61) * mm, "end": v(15.82, -6.22) * mm});
            skArc(sketch, "E12.8.120", {"start": v(11.66, -6.73) * mm, "mid": v(10.94, -6.62) * mm, "end": v(10.33, -7.03) * mm});
            skArc(sketch, "E12.8.121", {"start": v(9.68, -7.91) * mm, "mid": v(9.45, -8.6) * mm, "end": v(9.76, -9.27) * mm});
            skArc(sketch, "E12.8.122", {"start": v(10.74, -10.94) * mm, "mid": v(10.56, -10.22) * mm, "end": v(10.12, -9.61) * mm});
            skArc(sketch, "E12.8.123", {"start": v(10.46, -13.4) * mm, "mid": v(10.75, -13.03) * mm, "end": v(10.84, -12.56) * mm});
            skArc(sketch, "E12.8.124", {"start": v(15.12, -6.83) * mm, "mid": v(15.54, -6.61) * mm, "end": v(15.82, -6.22) * mm});
            skArc(sketch, "E12.8.125", {"start": v(9.68, -7.91) * mm, "mid": v(9.45, -8.6) * mm, "end": v(9.76, -9.27) * mm});
            skArc(sketch, "E12.8.126", {"start": v(11.66, -6.73) * mm, "mid": v(10.94, -6.62) * mm, "end": v(10.33, -7.03) * mm});
            skArc(sketch, "E12.8.127", {"start": v(10.74, -10.94) * mm, "mid": v(10.56, -10.22) * mm, "end": v(10.12, -9.61) * mm});
            skArc(sketch, "E12.8.128", {"start": v(10.46, -13.4) * mm, "mid": v(10.75, -13.03) * mm, "end": v(10.84, -12.56) * mm});
            skArc(sketch, "E12.8.129", {"start": v(9.68, -7.91) * mm, "mid": v(9.45, -8.6) * mm, "end": v(9.76, -9.27) * mm});
            skArc(sketch, "E12.8.130", {"start": v(15.12, -6.83) * mm, "mid": v(15.54, -6.61) * mm, "end": v(15.82, -6.22) * mm});
            skArc(sketch, "E12.8.131", {"start": v(11.66, -6.73) * mm, "mid": v(10.94, -6.62) * mm, "end": v(10.33, -7.03) * mm});
            skArc(sketch, "E12.8.132", {"start": v(10.46, -13.4) * mm, "mid": v(10.75, -13.03) * mm, "end": v(10.84, -12.56) * mm});
            skArc(sketch, "E12.8.133", {"start": v(10.74, -10.94) * mm, "mid": v(10.56, -10.22) * mm, "end": v(10.12, -9.61) * mm});
            skArc(sketch, "E12.8.134", {"start": v(10.74, -10.94) * mm, "mid": v(10.56, -10.22) * mm, "end": v(10.12, -9.61) * mm});
            skArc(sketch, "E12.8.135", {"start": v(10.46, -13.4) * mm, "mid": v(10.75, -13.03) * mm, "end": v(10.84, -12.56) * mm});
            skArc(sketch, "E12.8.136", {"start": v(9.68, -7.91) * mm, "mid": v(9.45, -8.6) * mm, "end": v(9.76, -9.27) * mm});
            skArc(sketch, "E12.8.137", {"start": v(15.12, -6.83) * mm, "mid": v(15.54, -6.61) * mm, "end": v(15.82, -6.22) * mm});
            skArc(sketch, "E12.8.138", {"start": v(11.66, -6.73) * mm, "mid": v(10.94, -6.62) * mm, "end": v(10.33, -7.03) * mm});
            skArc(sketch, "E12.8.139", {"start": v(9.68, -7.91) * mm, "mid": v(9.45, -8.6) * mm, "end": v(9.76, -9.27) * mm});
            skArc(sketch, "E12.8.140", {"start": v(11.66, -6.73) * mm, "mid": v(10.94, -6.62) * mm, "end": v(10.33, -7.03) * mm});
            skArc(sketch, "E12.8.141", {"start": v(10.74, -10.94) * mm, "mid": v(10.56, -10.22) * mm, "end": v(10.12, -9.61) * mm});
            skArc(sketch, "E12.8.142", {"start": v(10.46, -13.4) * mm, "mid": v(10.75, -13.03) * mm, "end": v(10.84, -12.56) * mm});
            skArc(sketch, "E12.8.143", {"start": v(15.12, -6.83) * mm, "mid": v(15.54, -6.61) * mm, "end": v(15.82, -6.22) * mm});
            skArc(sketch, "E12.8.144", {"start": v(15.12, -6.83) * mm, "mid": v(15.54, -6.61) * mm, "end": v(15.82, -6.22) * mm});
            skArc(sketch, "E12.8.145", {"start": v(10.74, -10.94) * mm, "mid": v(10.56, -10.22) * mm, "end": v(10.12, -9.61) * mm});
            skArc(sketch, "E12.8.146", {"start": v(9.68, -7.91) * mm, "mid": v(9.45, -8.6) * mm, "end": v(9.76, -9.27) * mm});
            skArc(sketch, "E12.8.147", {"start": v(11.66, -6.73) * mm, "mid": v(10.94, -6.62) * mm, "end": v(10.33, -7.03) * mm});
            skArc(sketch, "E12.8.148", {"start": v(10.46, -13.4) * mm, "mid": v(10.75, -13.03) * mm, "end": v(10.84, -12.56) * mm});
            skArc(sketch, "E12.8.149", {"start": v(9.68, -7.91) * mm, "mid": v(9.45, -8.6) * mm, "end": v(9.76, -9.27) * mm});
            skArc(sketch, "E12.8.150", {"start": v(15.12, -6.83) * mm, "mid": v(15.54, -6.61) * mm, "end": v(15.82, -6.22) * mm});
            skArc(sketch, "E12.8.151", {"start": v(11.66, -6.73) * mm, "mid": v(10.94, -6.62) * mm, "end": v(10.33, -7.03) * mm});
            skArc(sketch, "E12.8.152", {"start": v(10.46, -13.4) * mm, "mid": v(10.75, -13.03) * mm, "end": v(10.84, -12.56) * mm});
            skArc(sketch, "E12.8.153", {"start": v(10.74, -10.94) * mm, "mid": v(10.56, -10.22) * mm, "end": v(10.12, -9.61) * mm});
            skArc(sketch, "E12.8.154", {"start": v(15.12, -6.83) * mm, "mid": v(15.54, -6.61) * mm, "end": v(15.82, -6.22) * mm});
            skArc(sketch, "E12.8.155", {"start": v(10.46, -13.4) * mm, "mid": v(10.75, -13.03) * mm, "end": v(10.84, -12.56) * mm});
            skArc(sketch, "E12.8.156", {"start": v(9.68, -7.91) * mm, "mid": v(9.45, -8.6) * mm, "end": v(9.76, -9.27) * mm});
            skArc(sketch, "E12.8.157", {"start": v(10.74, -10.94) * mm, "mid": v(10.56, -10.22) * mm, "end": v(10.12, -9.61) * mm});
            skArc(sketch, "E12.8.158", {"start": v(11.66, -6.73) * mm, "mid": v(10.94, -6.62) * mm, "end": v(10.33, -7.03) * mm});
            skArc(sketch, "E12.8.159", {"start": v(15.12, -6.83) * mm, "mid": v(15.54, -6.61) * mm, "end": v(15.82, -6.22) * mm});
            skArc(sketch, "E12.8.160", {"start": v(11.66, -6.73) * mm, "mid": v(10.94, -6.62) * mm, "end": v(10.33, -7.03) * mm});
            skArc(sketch, "E12.8.161", {"start": v(9.68, -7.91) * mm, "mid": v(9.45, -8.6) * mm, "end": v(9.76, -9.27) * mm});
            skArc(sketch, "E12.8.162", {"start": v(10.74, -10.94) * mm, "mid": v(10.56, -10.22) * mm, "end": v(10.12, -9.61) * mm});
            skArc(sketch, "E12.8.163", {"start": v(10.46, -13.4) * mm, "mid": v(10.75, -13.03) * mm, "end": v(10.84, -12.56) * mm});
            skArc(sketch, "E12.8.164", {"start": v(12.09, -6.98) * mm, "mid": v(12.8, -7.23) * mm, "end": v(13.54, -7.2) * mm});
            skArc(sketch, "E12.8.165", {"start": v(9.68, -7.91) * mm, "mid": v(10.01, -7.48) * mm, "end": v(10.33, -7.03) * mm});
            skArc(sketch, "E12.8.166", {"start": v(10.46, -13.4) * mm, "mid": v(10.75, -13.03) * mm, "end": v(10.84, -12.56) * mm});
            skLineSegment(sketch, "E12.8.167", {"start": v(10.74, -10.94) * mm, "end": v(10.84, -12.56) * mm});
            skLineSegment(sketch, "E12.8.168", {"start": v(13.54, -7.2) * mm, "end": v(15.12, -6.83) * mm});
            skArc(sketch, "E12.8.169", {"start": v(15.12, -6.83) * mm, "mid": v(15.54, -6.61) * mm, "end": v(15.82, -6.22) * mm});
            skLineSegment(sketch, "E12.8.170", {"start": v(13.54, -7.2) * mm, "end": v(15.12, -6.83) * mm});
            skLineSegment(sketch, "E12.8.171", {"start": v(10.74, -10.94) * mm, "end": v(10.84, -12.56) * mm});
            skLineSegment(sketch, "E12.8.172", {"start": v(9.76, -9.27) * mm, "end": v(10.12, -9.61) * mm});
            skArc(sketch, "E12.8.173", {"start": v(9.68, -7.91) * mm, "mid": v(10.01, -7.48) * mm, "end": v(10.33, -7.03) * mm});
            skArc(sketch, "E12.8.174", {"start": v(12.09, -6.98) * mm, "mid": v(12.8, -7.23) * mm, "end": v(13.54, -7.2) * mm});
            skLineSegment(sketch, "E12.8.175", {"start": v(10.74, -10.94) * mm, "end": v(10.84, -12.56) * mm});
            skArc(sketch, "E12.8.176", {"start": v(12.09, -6.98) * mm, "mid": v(12.8, -7.23) * mm, "end": v(13.54, -7.2) * mm});
            skLineSegment(sketch, "E12.8.177", {"start": v(13.54, -7.2) * mm, "end": v(15.12, -6.83) * mm});
            skLineSegment(sketch, "E12.8.178", {"start": v(9.76, -9.27) * mm, "end": v(10.12, -9.61) * mm});
            skArc(sketch, "E12.8.179", {"start": v(9.68, -7.91) * mm, "mid": v(10.01, -7.48) * mm, "end": v(10.33, -7.03) * mm});
            skLineSegment(sketch, "E12.8.180", {"start": v(13.54, -7.2) * mm, "end": v(15.12, -6.83) * mm});
            skArc(sketch, "E12.8.181", {"start": v(12.09, -6.98) * mm, "mid": v(12.8, -7.23) * mm, "end": v(13.54, -7.2) * mm});
            skArc(sketch, "E12.8.182", {"start": v(9.68, -7.91) * mm, "mid": v(10.01, -7.48) * mm, "end": v(10.33, -7.03) * mm});
            skLineSegment(sketch, "E12.8.183", {"start": v(9.76, -9.27) * mm, "end": v(10.12, -9.61) * mm});
            skLineSegment(sketch, "E12.8.184", {"start": v(10.74, -10.94) * mm, "end": v(10.84, -12.56) * mm});
            skArc(sketch, "E12.8.185", {"start": v(12.09, -6.98) * mm, "mid": v(12.8, -7.23) * mm, "end": v(13.54, -7.2) * mm});
            skLineSegment(sketch, "E12.8.186", {"start": v(13.54, -7.2) * mm, "end": v(15.12, -6.83) * mm});
            skLineSegment(sketch, "E12.8.187", {"start": v(10.74, -10.94) * mm, "end": v(10.84, -12.56) * mm});
            skArc(sketch, "E12.8.188", {"start": v(9.68, -7.91) * mm, "mid": v(10.01, -7.48) * mm, "end": v(10.33, -7.03) * mm});
            skLineSegment(sketch, "E12.8.189", {"start": v(9.76, -9.27) * mm, "end": v(10.12, -9.61) * mm});
            skArc(sketch, "E12.8.190", {"start": v(12.09, -6.98) * mm, "mid": v(12.8, -7.23) * mm, "end": v(13.54, -7.2) * mm});
            skLineSegment(sketch, "E12.8.191", {"start": v(10.74, -10.94) * mm, "end": v(10.84, -12.56) * mm});
            skArc(sketch, "E12.8.192", {"start": v(9.68, -7.91) * mm, "mid": v(10.01, -7.48) * mm, "end": v(10.33, -7.03) * mm});
            skLineSegment(sketch, "E12.8.193", {"start": v(13.54, -7.2) * mm, "end": v(15.12, -6.83) * mm});
            skLineSegment(sketch, "E12.8.194", {"start": v(9.76, -9.27) * mm, "end": v(10.12, -9.61) * mm});
            skLineSegment(sketch, "E12.8.195", {"start": v(13.54, -7.2) * mm, "end": v(15.12, -6.83) * mm});
            skArc(sketch, "E12.8.196", {"start": v(9.68, -7.91) * mm, "mid": v(10.01, -7.48) * mm, "end": v(10.33, -7.03) * mm});
            skLineSegment(sketch, "E12.8.197", {"start": v(10.74, -10.94) * mm, "end": v(10.84, -12.56) * mm});
            skArc(sketch, "E12.8.198", {"start": v(12.09, -6.98) * mm, "mid": v(12.8, -7.23) * mm, "end": v(13.54, -7.2) * mm});
            skLineSegment(sketch, "E12.8.199", {"start": v(9.76, -9.27) * mm, "end": v(10.12, -9.61) * mm});
            skLineSegment(sketch, "E12.8.200", {"start": v(10.74, -10.94) * mm, "end": v(10.84, -12.56) * mm});
            skArc(sketch, "E12.8.201", {"start": v(9.68, -7.91) * mm, "mid": v(10.01, -7.48) * mm, "end": v(10.33, -7.03) * mm});
            skLineSegment(sketch, "E12.8.202", {"start": v(12.09, -6.98) * mm, "end": v(11.66, -6.73) * mm});
            skLineSegment(sketch, "E12.8.203", {"start": v(13.54, -7.2) * mm, "end": v(15.12, -6.83) * mm});
            skArc(sketch, "E12.8.204", {"start": v(12.09, -6.98) * mm, "mid": v(12.8, -7.23) * mm, "end": v(13.54, -7.2) * mm});
            skLineSegment(sketch, "E12.8.205", {"start": v(9.76, -9.27) * mm, "end": v(10.12, -9.61) * mm});
            skLineSegment(sketch, "E12.8.206", {"start": v(12.09, -6.98) * mm, "end": v(11.66, -6.73) * mm});
            skLineSegment(sketch, "E12.8.207", {"start": v(9.76, -9.27) * mm, "end": v(10.12, -9.61) * mm});
            skArc(sketch, "E12.8.208", {"start": v(12.09, -6.98) * mm, "mid": v(12.8, -7.23) * mm, "end": v(13.54, -7.2) * mm});
            skLineSegment(sketch, "E12.8.209", {"start": v(10.74, -10.94) * mm, "end": v(10.84, -12.56) * mm});
            skArc(sketch, "E12.8.210", {"start": v(9.68, -7.91) * mm, "mid": v(10.01, -7.48) * mm, "end": v(10.33, -7.03) * mm});
            skLineSegment(sketch, "E12.8.211", {"start": v(13.54, -7.2) * mm, "end": v(15.12, -6.83) * mm});
            skArc(sketch, "E12.8.212", {"start": v(9.68, -7.91) * mm, "mid": v(10.01, -7.48) * mm, "end": v(10.33, -7.03) * mm});
            skLineSegment(sketch, "E12.8.213", {"start": v(13.54, -7.2) * mm, "end": v(15.12, -6.83) * mm});
            skLineSegment(sketch, "E12.8.214", {"start": v(10.74, -10.94) * mm, "end": v(10.84, -12.56) * mm});
            skLineSegment(sketch, "E12.8.215", {"start": v(12.09, -6.98) * mm, "end": v(11.66, -6.73) * mm});
            skArc(sketch, "E12.8.216", {"start": v(12.09, -6.98) * mm, "mid": v(12.8, -7.23) * mm, "end": v(13.54, -7.2) * mm});
            skLineSegment(sketch, "E12.8.217", {"start": v(9.76, -9.27) * mm, "end": v(10.12, -9.61) * mm});
            skLineSegment(sketch, "E12.8.218", {"start": v(13.54, -7.2) * mm, "end": v(15.12, -6.83) * mm});
            skArc(sketch, "E12.8.219", {"start": v(12.09, -6.98) * mm, "mid": v(12.8, -7.23) * mm, "end": v(13.54, -7.2) * mm});
            skLineSegment(sketch, "E12.8.220", {"start": v(10.74, -10.94) * mm, "end": v(10.84, -12.56) * mm});
            skLineSegment(sketch, "E12.8.221", {"start": v(9.76, -9.27) * mm, "end": v(10.12, -9.61) * mm});
            skArc(sketch, "E12.8.222", {"start": v(9.68, -7.91) * mm, "mid": v(10.01, -7.48) * mm, "end": v(10.33, -7.03) * mm});
            skLineSegment(sketch, "E12.8.223", {"start": v(12.09, -6.98) * mm, "end": v(11.66, -6.73) * mm});
            skLineSegment(sketch, "E12.8.224", {"start": v(13.54, -7.2) * mm, "end": v(15.12, -6.83) * mm});
            skLineSegment(sketch, "E12.8.225", {"start": v(10.74, -10.94) * mm, "end": v(10.84, -12.56) * mm});
            skLineSegment(sketch, "E12.8.226", {"start": v(12.09, -6.98) * mm, "end": v(11.66, -6.73) * mm});
            skArc(sketch, "E12.8.227", {"start": v(12.09, -6.98) * mm, "mid": v(12.8, -7.23) * mm, "end": v(13.54, -7.2) * mm});
            skLineSegment(sketch, "E12.8.228", {"start": v(9.76, -9.27) * mm, "end": v(10.12, -9.61) * mm});
            skArc(sketch, "E12.8.229", {"start": v(9.68, -7.91) * mm, "mid": v(10.01, -7.48) * mm, "end": v(10.33, -7.03) * mm});
            skArc(sketch, "E12.8.230", {"start": v(9.68, -7.91) * mm, "mid": v(10.01, -7.48) * mm, "end": v(10.33, -7.03) * mm});
            skLineSegment(sketch, "E12.8.231", {"start": v(9.76, -9.27) * mm, "end": v(10.12, -9.61) * mm});
            skLineSegment(sketch, "E12.8.232", {"start": v(13.54, -7.2) * mm, "end": v(15.12, -6.83) * mm});
            skLineSegment(sketch, "E12.8.233", {"start": v(12.09, -6.98) * mm, "end": v(11.66, -6.73) * mm});
            skArc(sketch, "E12.8.234", {"start": v(12.09, -6.98) * mm, "mid": v(12.8, -7.23) * mm, "end": v(13.54, -7.2) * mm});
            skLineSegment(sketch, "E12.8.235", {"start": v(10.74, -10.94) * mm, "end": v(10.84, -12.56) * mm});
            skLineSegment(sketch, "E12.8.236", {"start": v(9.76, -9.27) * mm, "end": v(10.12, -9.61) * mm});
            skLineSegment(sketch, "E12.8.237", {"start": v(12.09, -6.98) * mm, "end": v(11.66, -6.73) * mm});
            skLineSegment(sketch, "E12.8.238", {"start": v(12.09, -6.98) * mm, "end": v(11.66, -6.73) * mm});
            skLineSegment(sketch, "E12.8.239", {"start": v(12.09, -6.98) * mm, "end": v(11.66, -6.73) * mm});
            skLineSegment(sketch, "E12.8.240", {"start": v(12.09, -6.98) * mm, "end": v(11.66, -6.73) * mm});
            skLineSegment(sketch, "E12.8.241", {"start": v(12.09, -6.98) * mm, "end": v(11.66, -6.73) * mm});
            skLineSegment(sketch, "E12.8.242", {"start": v(12.09, -6.98) * mm, "end": v(11.66, -6.73) * mm});
            skLineSegment(sketch, "E12.8.243", {"start": v(12.09, -6.98) * mm, "end": v(11.66, -6.73) * mm});
            skLineSegment(sketch, "E12.9.0", {"start": v(16.81, 2.52) * mm, "end": v(0, 0) * mm});
            skPoint(sketch, "E12.9.1", {"position": v(16.88, 2) * mm});
            skPoint(sketch, "E12.9.2", {"position": v(16.53, -3.97) * mm});
            skLineSegment(sketch, "E12.9.3", {"start": v(15.76, -6.38) * mm, "end": v(0, 0) * mm});
            skPoint(sketch, "E12.9.4", {"position": v(14.34, -3.45) * mm});
            skPoint(sketch, "E12.9.6", {"position": v(15.95, -5.89) * mm});
            skPoint(sketch, "E12.9.7", {"position": v(12.5, 0) * mm});
            skPoint(sketch, "E12.9.8", {"position": v(17, 0) * mm});
            skPoint(sketch, "E12.9.9", {"position": v(14.75, 0) * mm});
            skPoint(sketch, "E12.9.10", {"position": v(12.15, -2.92) * mm});
            skPoint(sketch, "E12.9.11", {"position": v(16.53, -3.97) * mm});
            skPoint(sketch, "E12.9.12", {"position": v(15.95, -5.89) * mm});
            skPoint(sketch, "E12.9.13", {"position": v(12.15, -2.92) * mm});
            skPoint(sketch, "E12.9.14", {"position": v(12.5, 0) * mm});
            skPoint(sketch, "E12.9.15", {"position": v(14.34, -3.45) * mm});
            skPoint(sketch, "E12.9.16", {"position": v(16.88, 2) * mm});
            skPoint(sketch, "E12.9.17", {"position": v(14.75, 0) * mm});
            skPoint(sketch, "E12.9.18", {"position": v(17, 0) * mm});
            skPoint(sketch, "E12.9.19", {"position": v(15.95, -5.89) * mm});
            skPoint(sketch, "E12.9.20", {"position": v(16.53, -3.97) * mm});
            skPoint(sketch, "E12.9.21", {"position": v(12.15, -2.92) * mm});
            skPoint(sketch, "E12.9.22", {"position": v(14.75, 0) * mm});
            skPoint(sketch, "E12.9.23", {"position": v(14.34, -3.45) * mm});
            skPoint(sketch, "E12.9.24", {"position": v(12.5, 0) * mm});
            skPoint(sketch, "E12.9.25", {"position": v(17, 0) * mm});
            skPoint(sketch, "E12.9.26", {"position": v(16.88, 2) * mm});
            skPoint(sketch, "E12.9.27", {"position": v(16.53, -3.97) * mm});
            skPoint(sketch, "E12.9.28", {"position": v(14.34, -3.45) * mm});
            skPoint(sketch, "E12.9.29", {"position": v(17, 0) * mm});
            skPoint(sketch, "E12.9.30", {"position": v(16.88, 2) * mm});
            skPoint(sketch, "E12.9.31", {"position": v(15.95, -5.89) * mm});
            skPoint(sketch, "E12.9.32", {"position": v(12.5, 0) * mm});
            skPoint(sketch, "E12.9.33", {"position": v(14.75, 0) * mm});
            skPoint(sketch, "E12.9.34", {"position": v(12.15, -2.92) * mm});
            skPoint(sketch, "E12.9.35", {"position": v(12.5, 0) * mm});
            skPoint(sketch, "E12.9.36", {"position": v(16.88, 2) * mm});
            skPoint(sketch, "E12.9.37", {"position": v(15.95, -5.89) * mm});
            skPoint(sketch, "E12.9.38", {"position": v(16.53, -3.97) * mm});
            skPoint(sketch, "E12.9.39", {"position": v(17, 0) * mm});
            skPoint(sketch, "E12.9.40", {"position": v(14.34, -3.45) * mm});
            skPoint(sketch, "E12.9.41", {"position": v(14.75, 0) * mm});
            skPoint(sketch, "E12.9.42", {"position": v(12.15, -2.92) * mm});
            skPoint(sketch, "E12.9.43", {"position": v(12.15, -2.92) * mm});
            skPoint(sketch, "E12.9.44", {"position": v(15.95, -5.89) * mm});
            skPoint(sketch, "E12.9.45", {"position": v(16.88, 2) * mm});
            skPoint(sketch, "E12.9.46", {"position": v(16.53, -3.97) * mm});
            skPoint(sketch, "E12.9.47", {"position": v(14.34, -3.45) * mm});
            skPoint(sketch, "E12.9.48", {"position": v(12.5, 0) * mm});
            skPoint(sketch, "E12.9.49", {"position": v(14.75, 0) * mm});
            skPoint(sketch, "E12.9.50", {"position": v(14.34, -3.45) * mm});
            skPoint(sketch, "E12.9.51", {"position": v(15.95, -5.89) * mm});
            skPoint(sketch, "E12.9.52", {"position": v(14.75, 0) * mm});
            skPoint(sketch, "E12.9.53", {"position": v(12.5, 0) * mm});
            skPoint(sketch, "E12.9.54", {"position": v(12.15, -2.92) * mm});
            skPoint(sketch, "E12.9.55", {"position": v(17, 0) * mm});
            skPoint(sketch, "E12.9.56", {"position": v(16.53, -3.97) * mm});
            skPoint(sketch, "E12.9.57", {"position": v(16.88, 2) * mm});
            skPoint(sketch, "E12.9.58", {"position": v(15.95, -5.89) * mm});
            skPoint(sketch, "E12.9.59", {"position": v(14.75, 0) * mm});
            skPoint(sketch, "E12.9.60", {"position": v(16.88, 2) * mm});
            skPoint(sketch, "E12.9.61", {"position": v(14.34, -3.45) * mm});
            skPoint(sketch, "E12.9.62", {"position": v(12.15, -2.92) * mm});
            skPoint(sketch, "E12.9.63", {"position": v(12.5, 0) * mm});
            skPoint(sketch, "E12.9.64", {"position": v(16.53, -3.97) * mm});
            skPoint(sketch, "E12.9.65", {"position": v(17, 0) * mm});
            skPoint(sketch, "E12.9.66", {"position": v(14.75, 0) * mm});
            skPoint(sketch, "E12.9.67", {"position": v(12.5, 0) * mm});
            skPoint(sketch, "E12.9.68", {"position": v(14.34, -3.45) * mm});
            skPoint(sketch, "E12.9.69", {"position": v(12.15, -2.92) * mm});
            skPoint(sketch, "E12.9.70", {"position": v(16.88, 2) * mm});
            skPoint(sketch, "E12.9.71", {"position": v(17, 0) * mm});
            skPoint(sketch, "E12.9.72", {"position": v(15.95, -5.89) * mm});
            skPoint(sketch, "E12.9.73", {"position": v(16.53, -3.97) * mm});
            skPoint(sketch, "E12.9.74", {"position": v(17, 0) * mm});
            skPoint(sketch, "E12.9.75", {"position": v(12.5, 0) * mm});
            skPoint(sketch, "E12.9.76", {"position": v(15.95, -5.89) * mm});
            skPoint(sketch, "E12.9.77", {"position": v(14.75, 0) * mm});
            skPoint(sketch, "E12.9.78", {"position": v(16.88, 2) * mm});
            skPoint(sketch, "E12.9.79", {"position": v(14.34, -3.45) * mm});
            skPoint(sketch, "E12.9.80", {"position": v(16.53, -3.97) * mm});
            skPoint(sketch, "E12.9.81", {"position": v(12.15, -2.92) * mm});
            skPoint(sketch, "E12.9.82", {"position": v(17, 0) * mm});
            skPoint(sketch, "E12.9.83", {"position": v(15.95, -5.89) * mm});
            skPoint(sketch, "E12.9.84", {"position": v(16.88, 2) * mm});
            skPoint(sketch, "E12.9.85", {"position": v(12.15, -2.92) * mm});
            skPoint(sketch, "E12.9.86", {"position": v(14.75, 0) * mm});
            skPoint(sketch, "E12.9.87", {"position": v(14.34, -3.45) * mm});
            skPoint(sketch, "E12.9.88", {"position": v(12.5, 0) * mm});
            skPoint(sketch, "E12.9.89", {"position": v(16.88, 2) * mm});
            skPoint(sketch, "E12.9.90", {"position": v(12.5, 0) * mm});
            skPoint(sketch, "E12.9.91", {"position": v(12.15, -2.92) * mm});
            skPoint(sketch, "E12.9.92", {"position": v(14.75, 0) * mm});
            skPoint(sketch, "E12.9.93", {"position": v(14.34, -3.45) * mm});
            skPoint(sketch, "E12.9.94", {"position": v(15.95, -5.89) * mm});
            skPoint(sketch, "E12.9.95", {"position": v(14.34, -3.45) * mm});
            skPoint(sketch, "E12.9.96", {"position": v(12.15, -2.92) * mm});
            skPoint(sketch, "E12.9.97", {"position": v(14.75, 0) * mm});
            skPoint(sketch, "E12.9.98", {"position": v(12.5, 0) * mm});
            skPoint(sketch, "E12.9.99", {"position": v(16.88, 2) * mm});
            skPoint(sketch, "E12.9.100", {"position": v(15.95, -5.89) * mm});
            skArc(sketch, "E12.9.101", {"start": v(14.78, -4.1) * mm, "mid": v(14.26, -3.57) * mm, "end": v(13.57, -3.26) * mm});
            skArc(sketch, "E12.9.102", {"start": v(12.34, -2.01) * mm, "mid": v(12.5, -2.73) * mm, "end": v(13.1, -3.15) * mm});
            skArc(sketch, "E12.9.103", {"start": v(13.46, 0) * mm, "mid": v(12.78, -0.27) * mm, "end": v(12.47, -0.93) * mm});
            skArc(sketch, "E12.9.104", {"start": v(14.78, -4.1) * mm, "mid": v(14.26, -3.57) * mm, "end": v(13.57, -3.26) * mm});
            skArc(sketch, "E12.9.105", {"start": v(15.76, -6.38) * mm, "mid": v(15.83, -5.9) * mm, "end": v(15.67, -5.46) * mm});
            skArc(sketch, "E12.9.106", {"start": v(12.34, -2.01) * mm, "mid": v(12.5, -2.73) * mm, "end": v(13.1, -3.15) * mm});
            skArc(sketch, "E12.9.107", {"start": v(13.46, 0) * mm, "mid": v(12.78, -0.27) * mm, "end": v(12.47, -0.93) * mm});
            skArc(sketch, "E12.9.108", {"start": v(16.5, 1.64) * mm, "mid": v(16.77, 2.05) * mm, "end": v(16.81, 2.52) * mm});
            skArc(sketch, "E12.9.109", {"start": v(12.34, -2.01) * mm, "mid": v(12.5, -2.73) * mm, "end": v(13.1, -3.15) * mm});
            skArc(sketch, "E12.9.110", {"start": v(13.46, 0) * mm, "mid": v(12.78, -0.27) * mm, "end": v(12.47, -0.93) * mm});
            skArc(sketch, "E12.9.111", {"start": v(14.78, -4.1) * mm, "mid": v(14.26, -3.57) * mm, "end": v(13.57, -3.26) * mm});
            skArc(sketch, "E12.9.112", {"start": v(15.76, -6.38) * mm, "mid": v(15.83, -5.9) * mm, "end": v(15.67, -5.46) * mm});
            skArc(sketch, "E12.9.113", {"start": v(16.5, 1.64) * mm, "mid": v(16.77, 2.05) * mm, "end": v(16.81, 2.52) * mm});
            skArc(sketch, "E12.9.114", {"start": v(12.34, -2.01) * mm, "mid": v(12.5, -2.73) * mm, "end": v(13.1, -3.15) * mm});
            skArc(sketch, "E12.9.115", {"start": v(16.5, 1.64) * mm, "mid": v(16.77, 2.05) * mm, "end": v(16.81, 2.52) * mm});
            skArc(sketch, "E12.9.116", {"start": v(13.46, 0) * mm, "mid": v(12.78, -0.27) * mm, "end": v(12.47, -0.93) * mm});
            skArc(sketch, "E12.9.117", {"start": v(14.78, -4.1) * mm, "mid": v(14.26, -3.57) * mm, "end": v(13.57, -3.26) * mm});
            skArc(sketch, "E12.9.118", {"start": v(15.76, -6.38) * mm, "mid": v(15.83, -5.9) * mm, "end": v(15.67, -5.46) * mm});
            skArc(sketch, "E12.9.119", {"start": v(16.5, 1.64) * mm, "mid": v(16.77, 2.05) * mm, "end": v(16.81, 2.52) * mm});
            skArc(sketch, "E12.9.120", {"start": v(13.46, 0) * mm, "mid": v(12.78, -0.27) * mm, "end": v(12.47, -0.93) * mm});
            skArc(sketch, "E12.9.121", {"start": v(12.34, -2.01) * mm, "mid": v(12.5, -2.73) * mm, "end": v(13.1, -3.15) * mm});
            skArc(sketch, "E12.9.122", {"start": v(14.78, -4.1) * mm, "mid": v(14.26, -3.57) * mm, "end": v(13.57, -3.26) * mm});
            skArc(sketch, "E12.9.123", {"start": v(15.76, -6.38) * mm, "mid": v(15.83, -5.9) * mm, "end": v(15.67, -5.46) * mm});
            skArc(sketch, "E12.9.124", {"start": v(16.5, 1.64) * mm, "mid": v(16.77, 2.05) * mm, "end": v(16.81, 2.52) * mm});
            skArc(sketch, "E12.9.125", {"start": v(12.34, -2.01) * mm, "mid": v(12.5, -2.73) * mm, "end": v(13.1, -3.15) * mm});
            skArc(sketch, "E12.9.126", {"start": v(13.46, 0) * mm, "mid": v(12.78, -0.27) * mm, "end": v(12.47, -0.93) * mm});
            skArc(sketch, "E12.9.127", {"start": v(14.78, -4.1) * mm, "mid": v(14.26, -3.57) * mm, "end": v(13.57, -3.26) * mm});
            skArc(sketch, "E12.9.128", {"start": v(15.76, -6.38) * mm, "mid": v(15.83, -5.9) * mm, "end": v(15.67, -5.46) * mm});
            skArc(sketch, "E12.9.129", {"start": v(12.34, -2.01) * mm, "mid": v(12.5, -2.73) * mm, "end": v(13.1, -3.15) * mm});
            skArc(sketch, "E12.9.130", {"start": v(16.5, 1.64) * mm, "mid": v(16.77, 2.05) * mm, "end": v(16.81, 2.52) * mm});
            skArc(sketch, "E12.9.131", {"start": v(13.46, 0) * mm, "mid": v(12.78, -0.27) * mm, "end": v(12.47, -0.93) * mm});
            skArc(sketch, "E12.9.132", {"start": v(15.76, -6.38) * mm, "mid": v(15.83, -5.9) * mm, "end": v(15.67, -5.46) * mm});
            skArc(sketch, "E12.9.133", {"start": v(14.78, -4.1) * mm, "mid": v(14.26, -3.57) * mm, "end": v(13.57, -3.26) * mm});
            skArc(sketch, "E12.9.134", {"start": v(14.78, -4.1) * mm, "mid": v(14.26, -3.57) * mm, "end": v(13.57, -3.26) * mm});
            skArc(sketch, "E12.9.135", {"start": v(15.76, -6.38) * mm, "mid": v(15.83, -5.9) * mm, "end": v(15.67, -5.46) * mm});
            skArc(sketch, "E12.9.136", {"start": v(12.34, -2.01) * mm, "mid": v(12.5, -2.73) * mm, "end": v(13.1, -3.15) * mm});
            skArc(sketch, "E12.9.137", {"start": v(16.5, 1.64) * mm, "mid": v(16.77, 2.05) * mm, "end": v(16.81, 2.52) * mm});
            skArc(sketch, "E12.9.138", {"start": v(13.46, 0) * mm, "mid": v(12.78, -0.27) * mm, "end": v(12.47, -0.93) * mm});
            skArc(sketch, "E12.9.139", {"start": v(12.34, -2.01) * mm, "mid": v(12.5, -2.73) * mm, "end": v(13.1, -3.15) * mm});
            skArc(sketch, "E12.9.140", {"start": v(13.46, 0) * mm, "mid": v(12.78, -0.27) * mm, "end": v(12.47, -0.93) * mm});
            skArc(sketch, "E12.9.141", {"start": v(14.78, -4.1) * mm, "mid": v(14.26, -3.57) * mm, "end": v(13.57, -3.26) * mm});
            skArc(sketch, "E12.9.142", {"start": v(15.76, -6.38) * mm, "mid": v(15.83, -5.9) * mm, "end": v(15.67, -5.46) * mm});
            skArc(sketch, "E12.9.143", {"start": v(16.5, 1.64) * mm, "mid": v(16.77, 2.05) * mm, "end": v(16.81, 2.52) * mm});
            skArc(sketch, "E12.9.144", {"start": v(16.5, 1.64) * mm, "mid": v(16.77, 2.05) * mm, "end": v(16.81, 2.52) * mm});
            skArc(sketch, "E12.9.145", {"start": v(14.78, -4.1) * mm, "mid": v(14.26, -3.57) * mm, "end": v(13.57, -3.26) * mm});
            skArc(sketch, "E12.9.146", {"start": v(12.34, -2.01) * mm, "mid": v(12.5, -2.73) * mm, "end": v(13.1, -3.15) * mm});
            skArc(sketch, "E12.9.147", {"start": v(13.46, 0) * mm, "mid": v(12.78, -0.27) * mm, "end": v(12.47, -0.93) * mm});
            skArc(sketch, "E12.9.148", {"start": v(15.76, -6.38) * mm, "mid": v(15.83, -5.9) * mm, "end": v(15.67, -5.46) * mm});
            skArc(sketch, "E12.9.149", {"start": v(12.34, -2.01) * mm, "mid": v(12.5, -2.73) * mm, "end": v(13.1, -3.15) * mm});
            skArc(sketch, "E12.9.150", {"start": v(16.5, 1.64) * mm, "mid": v(16.77, 2.05) * mm, "end": v(16.81, 2.52) * mm});
            skArc(sketch, "E12.9.151", {"start": v(13.46, 0) * mm, "mid": v(12.78, -0.27) * mm, "end": v(12.47, -0.93) * mm});
            skArc(sketch, "E12.9.152", {"start": v(15.76, -6.38) * mm, "mid": v(15.83, -5.9) * mm, "end": v(15.67, -5.46) * mm});
            skArc(sketch, "E12.9.153", {"start": v(14.78, -4.1) * mm, "mid": v(14.26, -3.57) * mm, "end": v(13.57, -3.26) * mm});
            skArc(sketch, "E12.9.154", {"start": v(16.5, 1.64) * mm, "mid": v(16.77, 2.05) * mm, "end": v(16.81, 2.52) * mm});
            skArc(sketch, "E12.9.155", {"start": v(15.76, -6.38) * mm, "mid": v(15.83, -5.9) * mm, "end": v(15.67, -5.46) * mm});
            skArc(sketch, "E12.9.156", {"start": v(12.34, -2.01) * mm, "mid": v(12.5, -2.73) * mm, "end": v(13.1, -3.15) * mm});
            skArc(sketch, "E12.9.157", {"start": v(14.78, -4.1) * mm, "mid": v(14.26, -3.57) * mm, "end": v(13.57, -3.26) * mm});
            skArc(sketch, "E12.9.158", {"start": v(13.46, 0) * mm, "mid": v(12.78, -0.27) * mm, "end": v(12.47, -0.93) * mm});
            skArc(sketch, "E12.9.159", {"start": v(16.5, 1.64) * mm, "mid": v(16.77, 2.05) * mm, "end": v(16.81, 2.52) * mm});
            skArc(sketch, "E12.9.160", {"start": v(13.46, 0) * mm, "mid": v(12.78, -0.27) * mm, "end": v(12.47, -0.93) * mm});
            skArc(sketch, "E12.9.161", {"start": v(12.34, -2.01) * mm, "mid": v(12.5, -2.73) * mm, "end": v(13.1, -3.15) * mm});
            skArc(sketch, "E12.9.162", {"start": v(14.78, -4.1) * mm, "mid": v(14.26, -3.57) * mm, "end": v(13.57, -3.26) * mm});
            skArc(sketch, "E12.9.163", {"start": v(15.76, -6.38) * mm, "mid": v(15.83, -5.9) * mm, "end": v(15.67, -5.46) * mm});
            skArc(sketch, "E12.9.164", {"start": v(13.96, 0) * mm, "mid": v(14.7, 0.14) * mm, "end": v(15.33, 0.54) * mm});
            skArc(sketch, "E12.9.165", {"start": v(12.34, -2.01) * mm, "mid": v(12.41, -1.47) * mm, "end": v(12.47, -0.93) * mm});
            skArc(sketch, "E12.9.166", {"start": v(15.76, -6.38) * mm, "mid": v(15.83, -5.9) * mm, "end": v(15.67, -5.46) * mm});
            skLineSegment(sketch, "E12.9.167", {"start": v(14.78, -4.1) * mm, "end": v(15.67, -5.46) * mm});
            skLineSegment(sketch, "E12.9.168", {"start": v(15.33, 0.54) * mm, "end": v(16.5, 1.64) * mm});
            skArc(sketch, "E12.9.169", {"start": v(16.5, 1.64) * mm, "mid": v(16.77, 2.05) * mm, "end": v(16.81, 2.52) * mm});
            skLineSegment(sketch, "E12.9.170", {"start": v(15.33, 0.54) * mm, "end": v(16.5, 1.64) * mm});
            skLineSegment(sketch, "E12.9.171", {"start": v(14.78, -4.1) * mm, "end": v(15.67, -5.46) * mm});
            skLineSegment(sketch, "E12.9.172", {"start": v(13.1, -3.15) * mm, "end": v(13.57, -3.26) * mm});
            skArc(sketch, "E12.9.173", {"start": v(12.34, -2.01) * mm, "mid": v(12.41, -1.47) * mm, "end": v(12.47, -0.93) * mm});
            skArc(sketch, "E12.9.174", {"start": v(13.96, 0) * mm, "mid": v(14.7, 0.14) * mm, "end": v(15.33, 0.54) * mm});
            skLineSegment(sketch, "E12.9.175", {"start": v(14.78, -4.1) * mm, "end": v(15.67, -5.46) * mm});
            skArc(sketch, "E12.9.176", {"start": v(13.96, 0) * mm, "mid": v(14.7, 0.14) * mm, "end": v(15.33, 0.54) * mm});
            skLineSegment(sketch, "E12.9.177", {"start": v(15.33, 0.54) * mm, "end": v(16.5, 1.64) * mm});
            skLineSegment(sketch, "E12.9.178", {"start": v(13.1, -3.15) * mm, "end": v(13.57, -3.26) * mm});
            skArc(sketch, "E12.9.179", {"start": v(12.34, -2.01) * mm, "mid": v(12.41, -1.47) * mm, "end": v(12.47, -0.93) * mm});
            skLineSegment(sketch, "E12.9.180", {"start": v(15.33, 0.54) * mm, "end": v(16.5, 1.64) * mm});
            skArc(sketch, "E12.9.181", {"start": v(13.96, 0) * mm, "mid": v(14.7, 0.14) * mm, "end": v(15.33, 0.54) * mm});
            skArc(sketch, "E12.9.182", {"start": v(12.34, -2.01) * mm, "mid": v(12.41, -1.47) * mm, "end": v(12.47, -0.93) * mm});
            skLineSegment(sketch, "E12.9.183", {"start": v(13.1, -3.15) * mm, "end": v(13.57, -3.26) * mm});
            skLineSegment(sketch, "E12.9.184", {"start": v(14.78, -4.1) * mm, "end": v(15.67, -5.46) * mm});
            skArc(sketch, "E12.9.185", {"start": v(13.96, 0) * mm, "mid": v(14.7, 0.14) * mm, "end": v(15.33, 0.54) * mm});
            skLineSegment(sketch, "E12.9.186", {"start": v(15.33, 0.54) * mm, "end": v(16.5, 1.64) * mm});
            skLineSegment(sketch, "E12.9.187", {"start": v(14.78, -4.1) * mm, "end": v(15.67, -5.46) * mm});
            skArc(sketch, "E12.9.188", {"start": v(12.34, -2.01) * mm, "mid": v(12.41, -1.47) * mm, "end": v(12.47, -0.93) * mm});
            skLineSegment(sketch, "E12.9.189", {"start": v(13.1, -3.15) * mm, "end": v(13.57, -3.26) * mm});
            skArc(sketch, "E12.9.190", {"start": v(13.96, 0) * mm, "mid": v(14.7, 0.14) * mm, "end": v(15.33, 0.54) * mm});
            skLineSegment(sketch, "E12.9.191", {"start": v(14.78, -4.1) * mm, "end": v(15.67, -5.46) * mm});
            skArc(sketch, "E12.9.192", {"start": v(12.34, -2.01) * mm, "mid": v(12.41, -1.47) * mm, "end": v(12.47, -0.93) * mm});
            skLineSegment(sketch, "E12.9.193", {"start": v(15.33, 0.54) * mm, "end": v(16.5, 1.64) * mm});
            skLineSegment(sketch, "E12.9.194", {"start": v(13.1, -3.15) * mm, "end": v(13.57, -3.26) * mm});
            skLineSegment(sketch, "E12.9.195", {"start": v(15.33, 0.54) * mm, "end": v(16.5, 1.64) * mm});
            skArc(sketch, "E12.9.196", {"start": v(12.34, -2.01) * mm, "mid": v(12.41, -1.47) * mm, "end": v(12.47, -0.93) * mm});
            skLineSegment(sketch, "E12.9.197", {"start": v(14.78, -4.1) * mm, "end": v(15.67, -5.46) * mm});
            skArc(sketch, "E12.9.198", {"start": v(13.96, 0) * mm, "mid": v(14.7, 0.14) * mm, "end": v(15.33, 0.54) * mm});
            skLineSegment(sketch, "E12.9.199", {"start": v(13.1, -3.15) * mm, "end": v(13.57, -3.26) * mm});
            skLineSegment(sketch, "E12.9.200", {"start": v(14.78, -4.1) * mm, "end": v(15.67, -5.46) * mm});
            skArc(sketch, "E12.9.201", {"start": v(12.34, -2.01) * mm, "mid": v(12.41, -1.47) * mm, "end": v(12.47, -0.93) * mm});
            skLineSegment(sketch, "E12.9.202", {"start": v(13.96, 0) * mm, "end": v(13.46, 0) * mm});
            skLineSegment(sketch, "E12.9.203", {"start": v(15.33, 0.54) * mm, "end": v(16.5, 1.64) * mm});
            skArc(sketch, "E12.9.204", {"start": v(13.96, 0) * mm, "mid": v(14.7, 0.14) * mm, "end": v(15.33, 0.54) * mm});
            skLineSegment(sketch, "E12.9.205", {"start": v(13.1, -3.15) * mm, "end": v(13.57, -3.26) * mm});
            skLineSegment(sketch, "E12.9.206", {"start": v(13.96, 0) * mm, "end": v(13.46, 0) * mm});
            skLineSegment(sketch, "E12.9.207", {"start": v(13.1, -3.15) * mm, "end": v(13.57, -3.26) * mm});
            skArc(sketch, "E12.9.208", {"start": v(13.96, 0) * mm, "mid": v(14.7, 0.14) * mm, "end": v(15.33, 0.54) * mm});
            skLineSegment(sketch, "E12.9.209", {"start": v(14.78, -4.1) * mm, "end": v(15.67, -5.46) * mm});
            skArc(sketch, "E12.9.210", {"start": v(12.34, -2.01) * mm, "mid": v(12.41, -1.47) * mm, "end": v(12.47, -0.93) * mm});
            skLineSegment(sketch, "E12.9.211", {"start": v(15.33, 0.54) * mm, "end": v(16.5, 1.64) * mm});
            skArc(sketch, "E12.9.212", {"start": v(12.34, -2.01) * mm, "mid": v(12.41, -1.47) * mm, "end": v(12.47, -0.93) * mm});
            skLineSegment(sketch, "E12.9.213", {"start": v(15.33, 0.54) * mm, "end": v(16.5, 1.64) * mm});
            skLineSegment(sketch, "E12.9.214", {"start": v(14.78, -4.1) * mm, "end": v(15.67, -5.46) * mm});
            skLineSegment(sketch, "E12.9.215", {"start": v(13.96, 0) * mm, "end": v(13.46, 0) * mm});
            skArc(sketch, "E12.9.216", {"start": v(13.96, 0) * mm, "mid": v(14.7, 0.14) * mm, "end": v(15.33, 0.54) * mm});
            skLineSegment(sketch, "E12.9.217", {"start": v(13.1, -3.15) * mm, "end": v(13.57, -3.26) * mm});
            skLineSegment(sketch, "E12.9.218", {"start": v(15.33, 0.54) * mm, "end": v(16.5, 1.64) * mm});
            skArc(sketch, "E12.9.219", {"start": v(13.96, 0) * mm, "mid": v(14.7, 0.14) * mm, "end": v(15.33, 0.54) * mm});
            skLineSegment(sketch, "E12.9.220", {"start": v(14.78, -4.1) * mm, "end": v(15.67, -5.46) * mm});
            skLineSegment(sketch, "E12.9.221", {"start": v(13.1, -3.15) * mm, "end": v(13.57, -3.26) * mm});
            skArc(sketch, "E12.9.222", {"start": v(12.34, -2.01) * mm, "mid": v(12.41, -1.47) * mm, "end": v(12.47, -0.93) * mm});
            skLineSegment(sketch, "E12.9.223", {"start": v(13.96, 0) * mm, "end": v(13.46, 0) * mm});
            skLineSegment(sketch, "E12.9.224", {"start": v(15.33, 0.54) * mm, "end": v(16.5, 1.64) * mm});
            skLineSegment(sketch, "E12.9.225", {"start": v(14.78, -4.1) * mm, "end": v(15.67, -5.46) * mm});
            skLineSegment(sketch, "E12.9.226", {"start": v(13.96, 0) * mm, "end": v(13.46, 0) * mm});
            skArc(sketch, "E12.9.227", {"start": v(13.96, 0) * mm, "mid": v(14.7, 0.14) * mm, "end": v(15.33, 0.54) * mm});
            skLineSegment(sketch, "E12.9.228", {"start": v(13.1, -3.15) * mm, "end": v(13.57, -3.26) * mm});
            skArc(sketch, "E12.9.229", {"start": v(12.34, -2.01) * mm, "mid": v(12.41, -1.47) * mm, "end": v(12.47, -0.93) * mm});
            skArc(sketch, "E12.9.230", {"start": v(12.34, -2.01) * mm, "mid": v(12.41, -1.47) * mm, "end": v(12.47, -0.93) * mm});
            skLineSegment(sketch, "E12.9.231", {"start": v(13.1, -3.15) * mm, "end": v(13.57, -3.26) * mm});
            skLineSegment(sketch, "E12.9.232", {"start": v(15.33, 0.54) * mm, "end": v(16.5, 1.64) * mm});
            skLineSegment(sketch, "E12.9.233", {"start": v(13.96, 0) * mm, "end": v(13.46, 0) * mm});
            skArc(sketch, "E12.9.234", {"start": v(13.96, 0) * mm, "mid": v(14.7, 0.14) * mm, "end": v(15.33, 0.54) * mm});
            skLineSegment(sketch, "E12.9.235", {"start": v(14.78, -4.1) * mm, "end": v(15.67, -5.46) * mm});
            skLineSegment(sketch, "E12.9.236", {"start": v(13.1, -3.15) * mm, "end": v(13.57, -3.26) * mm});
            skLineSegment(sketch, "E12.9.237", {"start": v(13.96, 0) * mm, "end": v(13.46, 0) * mm});
            skLineSegment(sketch, "E12.9.238", {"start": v(13.96, 0) * mm, "end": v(13.46, 0) * mm});
            skLineSegment(sketch, "E12.9.239", {"start": v(13.96, 0) * mm, "end": v(13.46, 0) * mm});
            skLineSegment(sketch, "E12.9.240", {"start": v(13.96, 0) * mm, "end": v(13.46, 0) * mm});
            skLineSegment(sketch, "E12.9.241", {"start": v(13.96, 0) * mm, "end": v(13.46, 0) * mm});
            skLineSegment(sketch, "E12.9.242", {"start": v(13.96, 0) * mm, "end": v(13.46, 0) * mm});
            skLineSegment(sketch, "E12.9.243", {"start": v(13.96, 0) * mm, "end": v(13.46, 0) * mm});
            skPoint(sketch, "E12.10.1", {"position": v(13.62, 10.17) * mm});
            skPoint(sketch, "E12.10.2", {"position": v(16.3, 4.82) * mm});
            skLineSegment(sketch, "E12.10.3", {"start": v(16.84, 2.35) * mm, "end": v(0, 0) * mm});
            skPoint(sketch, "E12.10.4", {"position": v(14.14, 4.19) * mm});
            skPoint(sketch, "E12.10.6", {"position": v(16.75, 2.88) * mm});
            skPoint(sketch, "E12.10.7", {"position": v(10.83, 6.25) * mm});
            skPoint(sketch, "E12.10.8", {"position": v(14.72, 8.5) * mm});
            skPoint(sketch, "E12.10.9", {"position": v(12.77, 7.38) * mm});
            skPoint(sketch, "E12.10.10", {"position": v(11.99, 3.55) * mm});
            skPoint(sketch, "E12.10.11", {"position": v(16.3, 4.82) * mm});
            skPoint(sketch, "E12.10.12", {"position": v(16.75, 2.88) * mm});
            skPoint(sketch, "E12.10.13", {"position": v(11.99, 3.55) * mm});
            skPoint(sketch, "E12.10.14", {"position": v(10.83, 6.25) * mm});
            skPoint(sketch, "E12.10.15", {"position": v(14.14, 4.19) * mm});
            skPoint(sketch, "E12.10.16", {"position": v(13.62, 10.17) * mm});
            skPoint(sketch, "E12.10.17", {"position": v(12.77, 7.38) * mm});
            skPoint(sketch, "E12.10.18", {"position": v(14.72, 8.5) * mm});
            skPoint(sketch, "E12.10.19", {"position": v(16.75, 2.88) * mm});
            skPoint(sketch, "E12.10.20", {"position": v(16.3, 4.82) * mm});
            skPoint(sketch, "E12.10.21", {"position": v(11.99, 3.55) * mm});
            skPoint(sketch, "E12.10.22", {"position": v(12.77, 7.38) * mm});
            skPoint(sketch, "E12.10.23", {"position": v(14.14, 4.19) * mm});
            skPoint(sketch, "E12.10.24", {"position": v(10.83, 6.25) * mm});
            skPoint(sketch, "E12.10.25", {"position": v(14.72, 8.5) * mm});
            skPoint(sketch, "E12.10.26", {"position": v(13.62, 10.17) * mm});
            skPoint(sketch, "E12.10.27", {"position": v(16.3, 4.82) * mm});
            skPoint(sketch, "E12.10.28", {"position": v(14.14, 4.19) * mm});
            skPoint(sketch, "E12.10.29", {"position": v(14.72, 8.5) * mm});
            skPoint(sketch, "E12.10.30", {"position": v(13.62, 10.17) * mm});
            skPoint(sketch, "E12.10.31", {"position": v(16.75, 2.88) * mm});
            skPoint(sketch, "E12.10.32", {"position": v(10.83, 6.25) * mm});
            skPoint(sketch, "E12.10.33", {"position": v(12.77, 7.38) * mm});
            skPoint(sketch, "E12.10.34", {"position": v(11.99, 3.55) * mm});
            skPoint(sketch, "E12.10.35", {"position": v(10.83, 6.25) * mm});
            skPoint(sketch, "E12.10.36", {"position": v(13.62, 10.17) * mm});
            skPoint(sketch, "E12.10.37", {"position": v(16.75, 2.88) * mm});
            skPoint(sketch, "E12.10.38", {"position": v(16.3, 4.82) * mm});
            skPoint(sketch, "E12.10.39", {"position": v(14.72, 8.5) * mm});
            skPoint(sketch, "E12.10.40", {"position": v(14.14, 4.19) * mm});
            skPoint(sketch, "E12.10.41", {"position": v(12.77, 7.38) * mm});
            skPoint(sketch, "E12.10.42", {"position": v(11.99, 3.55) * mm});
            skPoint(sketch, "E12.10.43", {"position": v(11.99, 3.55) * mm});
            skPoint(sketch, "E12.10.44", {"position": v(16.75, 2.88) * mm});
            skPoint(sketch, "E12.10.45", {"position": v(13.62, 10.17) * mm});
            skPoint(sketch, "E12.10.46", {"position": v(16.3, 4.82) * mm});
            skPoint(sketch, "E12.10.47", {"position": v(14.14, 4.19) * mm});
            skPoint(sketch, "E12.10.48", {"position": v(10.83, 6.25) * mm});
            skPoint(sketch, "E12.10.49", {"position": v(12.77, 7.38) * mm});
            skPoint(sketch, "E12.10.50", {"position": v(14.14, 4.19) * mm});
            skPoint(sketch, "E12.10.51", {"position": v(16.75, 2.88) * mm});
            skPoint(sketch, "E12.10.52", {"position": v(12.77, 7.38) * mm});
            skPoint(sketch, "E12.10.53", {"position": v(10.83, 6.25) * mm});
            skPoint(sketch, "E12.10.54", {"position": v(11.99, 3.55) * mm});
            skPoint(sketch, "E12.10.55", {"position": v(14.72, 8.5) * mm});
            skPoint(sketch, "E12.10.56", {"position": v(16.3, 4.82) * mm});
            skPoint(sketch, "E12.10.57", {"position": v(13.62, 10.17) * mm});
            skPoint(sketch, "E12.10.58", {"position": v(16.75, 2.88) * mm});
            skPoint(sketch, "E12.10.59", {"position": v(12.77, 7.38) * mm});
            skPoint(sketch, "E12.10.60", {"position": v(13.62, 10.17) * mm});
            skPoint(sketch, "E12.10.61", {"position": v(14.14, 4.19) * mm});
            skPoint(sketch, "E12.10.62", {"position": v(11.99, 3.55) * mm});
            skPoint(sketch, "E12.10.63", {"position": v(10.83, 6.25) * mm});
            skPoint(sketch, "E12.10.64", {"position": v(16.3, 4.82) * mm});
            skPoint(sketch, "E12.10.65", {"position": v(14.72, 8.5) * mm});
            skPoint(sketch, "E12.10.66", {"position": v(12.77, 7.38) * mm});
            skPoint(sketch, "E12.10.67", {"position": v(10.83, 6.25) * mm});
            skPoint(sketch, "E12.10.68", {"position": v(14.14, 4.19) * mm});
            skPoint(sketch, "E12.10.69", {"position": v(11.99, 3.55) * mm});
            skPoint(sketch, "E12.10.70", {"position": v(13.62, 10.17) * mm});
            skPoint(sketch, "E12.10.71", {"position": v(14.72, 8.5) * mm});
            skPoint(sketch, "E12.10.72", {"position": v(16.75, 2.88) * mm});
            skPoint(sketch, "E12.10.73", {"position": v(16.3, 4.82) * mm});
            skPoint(sketch, "E12.10.74", {"position": v(14.72, 8.5) * mm});
            skPoint(sketch, "E12.10.75", {"position": v(10.83, 6.25) * mm});
            skPoint(sketch, "E12.10.76", {"position": v(16.75, 2.88) * mm});
            skPoint(sketch, "E12.10.77", {"position": v(12.77, 7.38) * mm});
            skPoint(sketch, "E12.10.78", {"position": v(13.62, 10.17) * mm});
            skPoint(sketch, "E12.10.79", {"position": v(14.14, 4.19) * mm});
            skPoint(sketch, "E12.10.80", {"position": v(16.3, 4.82) * mm});
            skPoint(sketch, "E12.10.81", {"position": v(11.99, 3.55) * mm});
            skPoint(sketch, "E12.10.82", {"position": v(14.72, 8.5) * mm});
            skPoint(sketch, "E12.10.83", {"position": v(16.75, 2.88) * mm});
            skPoint(sketch, "E12.10.84", {"position": v(13.62, 10.17) * mm});
            skPoint(sketch, "E12.10.85", {"position": v(11.99, 3.55) * mm});
            skPoint(sketch, "E12.10.86", {"position": v(12.77, 7.38) * mm});
            skPoint(sketch, "E12.10.87", {"position": v(14.14, 4.19) * mm});
            skPoint(sketch, "E12.10.88", {"position": v(10.83, 6.25) * mm});
            skPoint(sketch, "E12.10.89", {"position": v(13.62, 10.17) * mm});
            skPoint(sketch, "E12.10.90", {"position": v(10.83, 6.25) * mm});
            skPoint(sketch, "E12.10.91", {"position": v(11.99, 3.55) * mm});
            skPoint(sketch, "E12.10.92", {"position": v(12.77, 7.38) * mm});
            skPoint(sketch, "E12.10.93", {"position": v(14.14, 4.19) * mm});
            skPoint(sketch, "E12.10.94", {"position": v(16.75, 2.88) * mm});
            skPoint(sketch, "E12.10.95", {"position": v(14.14, 4.19) * mm});
            skPoint(sketch, "E12.10.96", {"position": v(11.99, 3.55) * mm});
            skPoint(sketch, "E12.10.97", {"position": v(12.77, 7.38) * mm});
            skPoint(sketch, "E12.10.98", {"position": v(10.83, 6.25) * mm});
            skPoint(sketch, "E12.10.99", {"position": v(13.62, 10.17) * mm});
            skPoint(sketch, "E12.10.100", {"position": v(16.75, 2.88) * mm});
            skArc(sketch, "E12.10.101", {"start": v(14.85, 3.83) * mm, "mid": v(14.13, 4.04) * mm, "end": v(13.39, 3.96) * mm});
            skArc(sketch, "E12.10.102", {"start": v(11.7, 4.43) * mm, "mid": v(12.18, 3.88) * mm, "end": v(12.9, 3.82) * mm});
            skArc(sketch, "E12.10.103", {"start": v(11.66, 6.73) * mm, "mid": v(11.2, 6.16) * mm, "end": v(11.26, 5.43) * mm});
            skArc(sketch, "E12.10.104", {"start": v(14.85, 3.83) * mm, "mid": v(14.13, 4.04) * mm, "end": v(13.39, 3.96) * mm});
            skArc(sketch, "E12.10.105", {"start": v(16.84, 2.35) * mm, "mid": v(16.66, 2.8) * mm, "end": v(16.3, 3.1) * mm});
            skArc(sketch, "E12.10.106", {"start": v(11.7, 4.43) * mm, "mid": v(12.18, 3.88) * mm, "end": v(12.9, 3.82) * mm});
            skArc(sketch, "E12.10.107", {"start": v(11.66, 6.73) * mm, "mid": v(11.2, 6.16) * mm, "end": v(11.26, 5.43) * mm});
            skArc(sketch, "E12.10.108", {"start": v(13.47, 9.68) * mm, "mid": v(13.5, 10.16) * mm, "end": v(13.3, 10.6) * mm});
            skArc(sketch, "E12.10.109", {"start": v(11.7, 4.43) * mm, "mid": v(12.18, 3.88) * mm, "end": v(12.9, 3.82) * mm});
            skArc(sketch, "E12.10.110", {"start": v(11.66, 6.73) * mm, "mid": v(11.2, 6.16) * mm, "end": v(11.26, 5.43) * mm});
            skArc(sketch, "E12.10.111", {"start": v(14.85, 3.83) * mm, "mid": v(14.13, 4.04) * mm, "end": v(13.39, 3.96) * mm});
            skArc(sketch, "E12.10.112", {"start": v(16.84, 2.35) * mm, "mid": v(16.66, 2.8) * mm, "end": v(16.3, 3.1) * mm});
            skArc(sketch, "E12.10.113", {"start": v(13.47, 9.68) * mm, "mid": v(13.5, 10.16) * mm, "end": v(13.3, 10.6) * mm});
            skArc(sketch, "E12.10.114", {"start": v(11.7, 4.43) * mm, "mid": v(12.18, 3.88) * mm, "end": v(12.9, 3.82) * mm});
            skArc(sketch, "E12.10.115", {"start": v(13.47, 9.68) * mm, "mid": v(13.5, 10.16) * mm, "end": v(13.3, 10.6) * mm});
            skArc(sketch, "E12.10.116", {"start": v(11.66, 6.73) * mm, "mid": v(11.2, 6.16) * mm, "end": v(11.26, 5.43) * mm});
            skArc(sketch, "E12.10.117", {"start": v(14.85, 3.83) * mm, "mid": v(14.13, 4.04) * mm, "end": v(13.39, 3.96) * mm});
            skArc(sketch, "E12.10.118", {"start": v(16.84, 2.35) * mm, "mid": v(16.66, 2.8) * mm, "end": v(16.3, 3.1) * mm});
            skArc(sketch, "E12.10.119", {"start": v(13.47, 9.68) * mm, "mid": v(13.5, 10.16) * mm, "end": v(13.3, 10.6) * mm});
            skArc(sketch, "E12.10.120", {"start": v(11.66, 6.73) * mm, "mid": v(11.2, 6.16) * mm, "end": v(11.26, 5.43) * mm});
            skArc(sketch, "E12.10.121", {"start": v(11.7, 4.43) * mm, "mid": v(12.18, 3.88) * mm, "end": v(12.9, 3.82) * mm});
            skArc(sketch, "E12.10.122", {"start": v(14.85, 3.83) * mm, "mid": v(14.13, 4.04) * mm, "end": v(13.39, 3.96) * mm});
            skArc(sketch, "E12.10.123", {"start": v(16.84, 2.35) * mm, "mid": v(16.66, 2.8) * mm, "end": v(16.3, 3.1) * mm});
            skArc(sketch, "E12.10.124", {"start": v(13.47, 9.68) * mm, "mid": v(13.5, 10.16) * mm, "end": v(13.3, 10.6) * mm});
            skArc(sketch, "E12.10.125", {"start": v(11.7, 4.43) * mm, "mid": v(12.18, 3.88) * mm, "end": v(12.9, 3.82) * mm});
            skArc(sketch, "E12.10.126", {"start": v(11.66, 6.73) * mm, "mid": v(11.2, 6.16) * mm, "end": v(11.26, 5.43) * mm});
            skArc(sketch, "E12.10.127", {"start": v(14.85, 3.83) * mm, "mid": v(14.13, 4.04) * mm, "end": v(13.39, 3.96) * mm});
            skArc(sketch, "E12.10.128", {"start": v(16.84, 2.35) * mm, "mid": v(16.66, 2.8) * mm, "end": v(16.3, 3.1) * mm});
            skArc(sketch, "E12.10.129", {"start": v(11.7, 4.43) * mm, "mid": v(12.18, 3.88) * mm, "end": v(12.9, 3.82) * mm});
            skArc(sketch, "E12.10.130", {"start": v(13.47, 9.68) * mm, "mid": v(13.5, 10.16) * mm, "end": v(13.3, 10.6) * mm});
            skArc(sketch, "E12.10.131", {"start": v(11.66, 6.73) * mm, "mid": v(11.2, 6.16) * mm, "end": v(11.26, 5.43) * mm});
            skArc(sketch, "E12.10.132", {"start": v(16.84, 2.35) * mm, "mid": v(16.66, 2.8) * mm, "end": v(16.3, 3.1) * mm});
            skArc(sketch, "E12.10.133", {"start": v(14.85, 3.83) * mm, "mid": v(14.13, 4.04) * mm, "end": v(13.39, 3.96) * mm});
            skArc(sketch, "E12.10.134", {"start": v(14.85, 3.83) * mm, "mid": v(14.13, 4.04) * mm, "end": v(13.39, 3.96) * mm});
            skArc(sketch, "E12.10.135", {"start": v(16.84, 2.35) * mm, "mid": v(16.66, 2.8) * mm, "end": v(16.3, 3.1) * mm});
            skArc(sketch, "E12.10.136", {"start": v(11.7, 4.43) * mm, "mid": v(12.18, 3.88) * mm, "end": v(12.9, 3.82) * mm});
            skArc(sketch, "E12.10.137", {"start": v(13.47, 9.68) * mm, "mid": v(13.5, 10.16) * mm, "end": v(13.3, 10.6) * mm});
            skArc(sketch, "E12.10.138", {"start": v(11.66, 6.73) * mm, "mid": v(11.2, 6.16) * mm, "end": v(11.26, 5.43) * mm});
            skArc(sketch, "E12.10.139", {"start": v(11.7, 4.43) * mm, "mid": v(12.18, 3.88) * mm, "end": v(12.9, 3.82) * mm});
            skArc(sketch, "E12.10.140", {"start": v(11.66, 6.73) * mm, "mid": v(11.2, 6.16) * mm, "end": v(11.26, 5.43) * mm});
            skArc(sketch, "E12.10.141", {"start": v(14.85, 3.83) * mm, "mid": v(14.13, 4.04) * mm, "end": v(13.39, 3.96) * mm});
            skArc(sketch, "E12.10.142", {"start": v(16.84, 2.35) * mm, "mid": v(16.66, 2.8) * mm, "end": v(16.3, 3.1) * mm});
            skArc(sketch, "E12.10.143", {"start": v(13.47, 9.68) * mm, "mid": v(13.5, 10.16) * mm, "end": v(13.3, 10.6) * mm});
            skArc(sketch, "E12.10.144", {"start": v(13.47, 9.68) * mm, "mid": v(13.5, 10.16) * mm, "end": v(13.3, 10.6) * mm});
            skArc(sketch, "E12.10.145", {"start": v(14.85, 3.83) * mm, "mid": v(14.13, 4.04) * mm, "end": v(13.39, 3.96) * mm});
            skArc(sketch, "E12.10.146", {"start": v(11.7, 4.43) * mm, "mid": v(12.18, 3.88) * mm, "end": v(12.9, 3.82) * mm});
            skArc(sketch, "E12.10.147", {"start": v(11.66, 6.73) * mm, "mid": v(11.2, 6.16) * mm, "end": v(11.26, 5.43) * mm});
            skArc(sketch, "E12.10.148", {"start": v(16.84, 2.35) * mm, "mid": v(16.66, 2.8) * mm, "end": v(16.3, 3.1) * mm});
            skArc(sketch, "E12.10.149", {"start": v(11.7, 4.43) * mm, "mid": v(12.18, 3.88) * mm, "end": v(12.9, 3.82) * mm});
            skArc(sketch, "E12.10.150", {"start": v(13.47, 9.68) * mm, "mid": v(13.5, 10.16) * mm, "end": v(13.3, 10.6) * mm});
            skArc(sketch, "E12.10.151", {"start": v(11.66, 6.73) * mm, "mid": v(11.2, 6.16) * mm, "end": v(11.26, 5.43) * mm});
            skArc(sketch, "E12.10.152", {"start": v(16.84, 2.35) * mm, "mid": v(16.66, 2.8) * mm, "end": v(16.3, 3.1) * mm});
            skArc(sketch, "E12.10.153", {"start": v(14.85, 3.83) * mm, "mid": v(14.13, 4.04) * mm, "end": v(13.39, 3.96) * mm});
            skArc(sketch, "E12.10.154", {"start": v(13.47, 9.68) * mm, "mid": v(13.5, 10.16) * mm, "end": v(13.3, 10.6) * mm});
            skArc(sketch, "E12.10.155", {"start": v(16.84, 2.35) * mm, "mid": v(16.66, 2.8) * mm, "end": v(16.3, 3.1) * mm});
            skArc(sketch, "E12.10.156", {"start": v(11.7, 4.43) * mm, "mid": v(12.18, 3.88) * mm, "end": v(12.9, 3.82) * mm});
            skArc(sketch, "E12.10.157", {"start": v(14.85, 3.83) * mm, "mid": v(14.13, 4.04) * mm, "end": v(13.39, 3.96) * mm});
            skArc(sketch, "E12.10.158", {"start": v(11.66, 6.73) * mm, "mid": v(11.2, 6.16) * mm, "end": v(11.26, 5.43) * mm});
            skArc(sketch, "E12.10.159", {"start": v(13.47, 9.68) * mm, "mid": v(13.5, 10.16) * mm, "end": v(13.3, 10.6) * mm});
            skArc(sketch, "E12.10.160", {"start": v(11.66, 6.73) * mm, "mid": v(11.2, 6.16) * mm, "end": v(11.26, 5.43) * mm});
            skArc(sketch, "E12.10.161", {"start": v(11.7, 4.43) * mm, "mid": v(12.18, 3.88) * mm, "end": v(12.9, 3.82) * mm});
            skArc(sketch, "E12.10.162", {"start": v(14.85, 3.83) * mm, "mid": v(14.13, 4.04) * mm, "end": v(13.39, 3.96) * mm});
            skArc(sketch, "E12.10.163", {"start": v(16.84, 2.35) * mm, "mid": v(16.66, 2.8) * mm, "end": v(16.3, 3.1) * mm});
            skArc(sketch, "E12.10.164", {"start": v(12.09, 6.98) * mm, "mid": v(12.66, 7.47) * mm, "end": v(13, 8.13) * mm});
            skArc(sketch, "E12.10.165", {"start": v(11.7, 4.43) * mm, "mid": v(11.49, 4.93) * mm, "end": v(11.26, 5.43) * mm});
            skArc(sketch, "E12.10.166", {"start": v(16.84, 2.35) * mm, "mid": v(16.66, 2.8) * mm, "end": v(16.3, 3.1) * mm});
            skLineSegment(sketch, "E12.10.167", {"start": v(14.85, 3.83) * mm, "end": v(16.3, 3.1) * mm});
            skLineSegment(sketch, "E12.10.168", {"start": v(13, 8.13) * mm, "end": v(13.47, 9.68) * mm});
            skArc(sketch, "E12.10.169", {"start": v(13.47, 9.68) * mm, "mid": v(13.5, 10.16) * mm, "end": v(13.3, 10.6) * mm});
            skLineSegment(sketch, "E12.10.170", {"start": v(13, 8.13) * mm, "end": v(13.47, 9.68) * mm});
            skLineSegment(sketch, "E12.10.171", {"start": v(14.85, 3.83) * mm, "end": v(16.3, 3.1) * mm});
            skLineSegment(sketch, "E12.10.172", {"start": v(12.9, 3.82) * mm, "end": v(13.39, 3.96) * mm});
            skArc(sketch, "E12.10.173", {"start": v(11.7, 4.43) * mm, "mid": v(11.49, 4.93) * mm, "end": v(11.26, 5.43) * mm});
            skArc(sketch, "E12.10.174", {"start": v(12.09, 6.98) * mm, "mid": v(12.66, 7.47) * mm, "end": v(13, 8.13) * mm});
            skLineSegment(sketch, "E12.10.175", {"start": v(14.85, 3.83) * mm, "end": v(16.3, 3.1) * mm});
            skArc(sketch, "E12.10.176", {"start": v(12.09, 6.98) * mm, "mid": v(12.66, 7.47) * mm, "end": v(13, 8.13) * mm});
            skLineSegment(sketch, "E12.10.177", {"start": v(13, 8.13) * mm, "end": v(13.47, 9.68) * mm});
            skLineSegment(sketch, "E12.10.178", {"start": v(12.9, 3.82) * mm, "end": v(13.39, 3.96) * mm});
            skArc(sketch, "E12.10.179", {"start": v(11.7, 4.43) * mm, "mid": v(11.49, 4.93) * mm, "end": v(11.26, 5.43) * mm});
            skLineSegment(sketch, "E12.10.180", {"start": v(13, 8.13) * mm, "end": v(13.47, 9.68) * mm});
            skArc(sketch, "E12.10.181", {"start": v(12.09, 6.98) * mm, "mid": v(12.66, 7.47) * mm, "end": v(13, 8.13) * mm});
            skArc(sketch, "E12.10.182", {"start": v(11.7, 4.43) * mm, "mid": v(11.49, 4.93) * mm, "end": v(11.26, 5.43) * mm});
            skLineSegment(sketch, "E12.10.183", {"start": v(12.9, 3.82) * mm, "end": v(13.39, 3.96) * mm});
            skLineSegment(sketch, "E12.10.184", {"start": v(14.85, 3.83) * mm, "end": v(16.3, 3.1) * mm});
            skArc(sketch, "E12.10.185", {"start": v(12.09, 6.98) * mm, "mid": v(12.66, 7.47) * mm, "end": v(13, 8.13) * mm});
            skLineSegment(sketch, "E12.10.186", {"start": v(13, 8.13) * mm, "end": v(13.47, 9.68) * mm});
            skLineSegment(sketch, "E12.10.187", {"start": v(14.85, 3.83) * mm, "end": v(16.3, 3.1) * mm});
            skArc(sketch, "E12.10.188", {"start": v(11.7, 4.43) * mm, "mid": v(11.49, 4.93) * mm, "end": v(11.26, 5.43) * mm});
            skLineSegment(sketch, "E12.10.189", {"start": v(12.9, 3.82) * mm, "end": v(13.39, 3.96) * mm});
            skArc(sketch, "E12.10.190", {"start": v(12.09, 6.98) * mm, "mid": v(12.66, 7.47) * mm, "end": v(13, 8.13) * mm});
            skLineSegment(sketch, "E12.10.191", {"start": v(14.85, 3.83) * mm, "end": v(16.3, 3.1) * mm});
            skArc(sketch, "E12.10.192", {"start": v(11.7, 4.43) * mm, "mid": v(11.49, 4.93) * mm, "end": v(11.26, 5.43) * mm});
            skLineSegment(sketch, "E12.10.193", {"start": v(13, 8.13) * mm, "end": v(13.47, 9.68) * mm});
            skLineSegment(sketch, "E12.10.194", {"start": v(12.9, 3.82) * mm, "end": v(13.39, 3.96) * mm});
            skLineSegment(sketch, "E12.10.195", {"start": v(13, 8.13) * mm, "end": v(13.47, 9.68) * mm});
            skArc(sketch, "E12.10.196", {"start": v(11.7, 4.43) * mm, "mid": v(11.49, 4.93) * mm, "end": v(11.26, 5.43) * mm});
            skLineSegment(sketch, "E12.10.197", {"start": v(14.85, 3.83) * mm, "end": v(16.3, 3.1) * mm});
            skArc(sketch, "E12.10.198", {"start": v(12.09, 6.98) * mm, "mid": v(12.66, 7.47) * mm, "end": v(13, 8.13) * mm});
            skLineSegment(sketch, "E12.10.199", {"start": v(12.9, 3.82) * mm, "end": v(13.39, 3.96) * mm});
            skLineSegment(sketch, "E12.10.200", {"start": v(14.85, 3.83) * mm, "end": v(16.3, 3.1) * mm});
            skArc(sketch, "E12.10.201", {"start": v(11.7, 4.43) * mm, "mid": v(11.49, 4.93) * mm, "end": v(11.26, 5.43) * mm});
            skLineSegment(sketch, "E12.10.202", {"start": v(12.09, 6.98) * mm, "end": v(11.66, 6.73) * mm});
            skLineSegment(sketch, "E12.10.203", {"start": v(13, 8.13) * mm, "end": v(13.47, 9.68) * mm});
            skArc(sketch, "E12.10.204", {"start": v(12.09, 6.98) * mm, "mid": v(12.66, 7.47) * mm, "end": v(13, 8.13) * mm});
            skLineSegment(sketch, "E12.10.205", {"start": v(12.9, 3.82) * mm, "end": v(13.39, 3.96) * mm});
            skLineSegment(sketch, "E12.10.206", {"start": v(12.09, 6.98) * mm, "end": v(11.66, 6.73) * mm});
            skLineSegment(sketch, "E12.10.207", {"start": v(12.9, 3.82) * mm, "end": v(13.39, 3.96) * mm});
            skArc(sketch, "E12.10.208", {"start": v(12.09, 6.98) * mm, "mid": v(12.66, 7.47) * mm, "end": v(13, 8.13) * mm});
            skLineSegment(sketch, "E12.10.209", {"start": v(14.85, 3.83) * mm, "end": v(16.3, 3.1) * mm});
            skArc(sketch, "E12.10.210", {"start": v(11.7, 4.43) * mm, "mid": v(11.49, 4.93) * mm, "end": v(11.26, 5.43) * mm});
            skLineSegment(sketch, "E12.10.211", {"start": v(13, 8.13) * mm, "end": v(13.47, 9.68) * mm});
            skArc(sketch, "E12.10.212", {"start": v(11.7, 4.43) * mm, "mid": v(11.49, 4.93) * mm, "end": v(11.26, 5.43) * mm});
            skLineSegment(sketch, "E12.10.213", {"start": v(13, 8.13) * mm, "end": v(13.47, 9.68) * mm});
            skLineSegment(sketch, "E12.10.214", {"start": v(14.85, 3.83) * mm, "end": v(16.3, 3.1) * mm});
            skLineSegment(sketch, "E12.10.215", {"start": v(12.09, 6.98) * mm, "end": v(11.66, 6.73) * mm});
            skArc(sketch, "E12.10.216", {"start": v(12.09, 6.98) * mm, "mid": v(12.66, 7.47) * mm, "end": v(13, 8.13) * mm});
            skLineSegment(sketch, "E12.10.217", {"start": v(12.9, 3.82) * mm, "end": v(13.39, 3.96) * mm});
            skLineSegment(sketch, "E12.10.218", {"start": v(13, 8.13) * mm, "end": v(13.47, 9.68) * mm});
            skArc(sketch, "E12.10.219", {"start": v(12.09, 6.98) * mm, "mid": v(12.66, 7.47) * mm, "end": v(13, 8.13) * mm});
            skLineSegment(sketch, "E12.10.220", {"start": v(14.85, 3.83) * mm, "end": v(16.3, 3.1) * mm});
            skLineSegment(sketch, "E12.10.221", {"start": v(12.9, 3.82) * mm, "end": v(13.39, 3.96) * mm});
            skArc(sketch, "E12.10.222", {"start": v(11.7, 4.43) * mm, "mid": v(11.49, 4.93) * mm, "end": v(11.26, 5.43) * mm});
            skLineSegment(sketch, "E12.10.223", {"start": v(12.09, 6.98) * mm, "end": v(11.66, 6.73) * mm});
            skLineSegment(sketch, "E12.10.224", {"start": v(13, 8.13) * mm, "end": v(13.47, 9.68) * mm});
            skLineSegment(sketch, "E12.10.225", {"start": v(14.85, 3.83) * mm, "end": v(16.3, 3.1) * mm});
            skLineSegment(sketch, "E12.10.226", {"start": v(12.09, 6.98) * mm, "end": v(11.66, 6.73) * mm});
            skArc(sketch, "E12.10.227", {"start": v(12.09, 6.98) * mm, "mid": v(12.66, 7.47) * mm, "end": v(13, 8.13) * mm});
            skLineSegment(sketch, "E12.10.228", {"start": v(12.9, 3.82) * mm, "end": v(13.39, 3.96) * mm});
            skArc(sketch, "E12.10.229", {"start": v(11.7, 4.43) * mm, "mid": v(11.49, 4.93) * mm, "end": v(11.26, 5.43) * mm});
            skArc(sketch, "E12.10.230", {"start": v(11.7, 4.43) * mm, "mid": v(11.49, 4.93) * mm, "end": v(11.26, 5.43) * mm});
            skLineSegment(sketch, "E12.10.231", {"start": v(12.9, 3.82) * mm, "end": v(13.39, 3.96) * mm});
            skLineSegment(sketch, "E12.10.232", {"start": v(13, 8.13) * mm, "end": v(13.47, 9.68) * mm});
            skLineSegment(sketch, "E12.10.233", {"start": v(12.09, 6.98) * mm, "end": v(11.66, 6.73) * mm});
            skArc(sketch, "E12.10.234", {"start": v(12.09, 6.98) * mm, "mid": v(12.66, 7.47) * mm, "end": v(13, 8.13) * mm});
            skLineSegment(sketch, "E12.10.235", {"start": v(14.85, 3.83) * mm, "end": v(16.3, 3.1) * mm});
            skLineSegment(sketch, "E12.10.236", {"start": v(12.9, 3.82) * mm, "end": v(13.39, 3.96) * mm});
            skLineSegment(sketch, "E12.10.237", {"start": v(12.09, 6.98) * mm, "end": v(11.66, 6.73) * mm});
            skLineSegment(sketch, "E12.10.238", {"start": v(12.09, 6.98) * mm, "end": v(11.66, 6.73) * mm});
            skLineSegment(sketch, "E12.10.239", {"start": v(12.09, 6.98) * mm, "end": v(11.66, 6.73) * mm});
            skLineSegment(sketch, "E12.10.240", {"start": v(12.09, 6.98) * mm, "end": v(11.66, 6.73) * mm});
            skLineSegment(sketch, "E12.10.241", {"start": v(12.09, 6.98) * mm, "end": v(11.66, 6.73) * mm});
            skLineSegment(sketch, "E12.10.242", {"start": v(12.09, 6.98) * mm, "end": v(11.66, 6.73) * mm});
            skLineSegment(sketch, "E12.10.243", {"start": v(12.09, 6.98) * mm, "end": v(11.66, 6.73) * mm});
            skPoint(sketch, "E12.11.1", {"position": v(6.71, 15.62) * mm});
            skPoint(sketch, "E12.11.4", {"position": v(10.16, 10.7) * mm});
            skPoint(sketch, "E12.11.6", {"position": v(13.07, 10.87) * mm});
            skPoint(sketch, "E12.11.7", {"position": v(6.25, 10.83) * mm});
            skPoint(sketch, "E12.11.8", {"position": v(8.5, 14.72) * mm});
            skPoint(sketch, "E12.11.9", {"position": v(7.38, 12.77) * mm});
            skPoint(sketch, "E12.11.10", {"position": v(8.6, 9.07) * mm});
            skPoint(sketch, "E12.11.11", {"position": v(11.7, 12.33) * mm});
            skPoint(sketch, "E12.11.12", {"position": v(13.07, 10.87) * mm});
            skPoint(sketch, "E12.11.13", {"position": v(8.6, 9.07) * mm});
            skPoint(sketch, "E12.11.14", {"position": v(6.25, 10.83) * mm});
            skPoint(sketch, "E12.11.15", {"position": v(10.16, 10.7) * mm});
            skPoint(sketch, "E12.11.16", {"position": v(6.71, 15.62) * mm});
            skPoint(sketch, "E12.11.17", {"position": v(7.38, 12.77) * mm});
            skPoint(sketch, "E12.11.18", {"position": v(8.5, 14.72) * mm});
            skPoint(sketch, "E12.11.19", {"position": v(13.07, 10.87) * mm});
            skPoint(sketch, "E12.11.20", {"position": v(11.7, 12.33) * mm});
            skPoint(sketch, "E12.11.21", {"position": v(8.6, 9.07) * mm});
            skPoint(sketch, "E12.11.22", {"position": v(7.38, 12.77) * mm});
            skPoint(sketch, "E12.11.23", {"position": v(10.16, 10.7) * mm});
            skPoint(sketch, "E12.11.24", {"position": v(6.25, 10.83) * mm});
            skPoint(sketch, "E12.11.25", {"position": v(8.5, 14.72) * mm});
            skPoint(sketch, "E12.11.26", {"position": v(6.71, 15.62) * mm});
            skPoint(sketch, "E12.11.27", {"position": v(11.7, 12.33) * mm});
            skPoint(sketch, "E12.11.28", {"position": v(10.16, 10.7) * mm});
            skPoint(sketch, "E12.11.29", {"position": v(8.5, 14.72) * mm});
            skPoint(sketch, "E12.11.30", {"position": v(6.71, 15.62) * mm});
            skPoint(sketch, "E12.11.31", {"position": v(13.07, 10.87) * mm});
            skPoint(sketch, "E12.11.32", {"position": v(6.25, 10.83) * mm});
            skPoint(sketch, "E12.11.33", {"position": v(7.38, 12.77) * mm});
            skPoint(sketch, "E12.11.34", {"position": v(8.6, 9.07) * mm});
            skPoint(sketch, "E12.11.35", {"position": v(6.25, 10.83) * mm});
            skPoint(sketch, "E12.11.36", {"position": v(6.71, 15.62) * mm});
            skPoint(sketch, "E12.11.37", {"position": v(13.07, 10.87) * mm});
            skPoint(sketch, "E12.11.38", {"position": v(11.7, 12.33) * mm});
            skPoint(sketch, "E12.11.39", {"position": v(8.5, 14.72) * mm});
            skPoint(sketch, "E12.11.40", {"position": v(10.16, 10.7) * mm});
            skPoint(sketch, "E12.11.41", {"position": v(7.38, 12.77) * mm});
            skPoint(sketch, "E12.11.42", {"position": v(8.6, 9.07) * mm});
            skPoint(sketch, "E12.11.43", {"position": v(8.6, 9.07) * mm});
            skPoint(sketch, "E12.11.44", {"position": v(13.07, 10.87) * mm});
            skPoint(sketch, "E12.11.45", {"position": v(6.71, 15.62) * mm});
            skPoint(sketch, "E12.11.46", {"position": v(11.7, 12.33) * mm});
            skPoint(sketch, "E12.11.47", {"position": v(10.16, 10.7) * mm});
            skPoint(sketch, "E12.11.48", {"position": v(6.25, 10.83) * mm});
            skPoint(sketch, "E12.11.49", {"position": v(7.38, 12.77) * mm});
            skPoint(sketch, "E12.11.50", {"position": v(10.16, 10.7) * mm});
            skPoint(sketch, "E12.11.51", {"position": v(13.07, 10.87) * mm});
            skPoint(sketch, "E12.11.52", {"position": v(7.38, 12.77) * mm});
            skPoint(sketch, "E12.11.53", {"position": v(6.25, 10.83) * mm});
            skPoint(sketch, "E12.11.54", {"position": v(8.6, 9.07) * mm});
            skPoint(sketch, "E12.11.55", {"position": v(8.5, 14.72) * mm});
            skPoint(sketch, "E12.11.56", {"position": v(11.7, 12.33) * mm});
            skPoint(sketch, "E12.11.57", {"position": v(6.71, 15.62) * mm});
            skPoint(sketch, "E12.11.58", {"position": v(13.07, 10.87) * mm});
            skPoint(sketch, "E12.11.59", {"position": v(7.38, 12.77) * mm});
            skPoint(sketch, "E12.11.60", {"position": v(6.71, 15.62) * mm});
            skPoint(sketch, "E12.11.61", {"position": v(10.16, 10.7) * mm});
            skPoint(sketch, "E12.11.62", {"position": v(8.6, 9.07) * mm});
            skPoint(sketch, "E12.11.63", {"position": v(6.25, 10.83) * mm});
            skPoint(sketch, "E12.11.64", {"position": v(11.7, 12.33) * mm});
            skPoint(sketch, "E12.11.65", {"position": v(8.5, 14.72) * mm});
            skPoint(sketch, "E12.11.66", {"position": v(7.38, 12.77) * mm});
            skPoint(sketch, "E12.11.67", {"position": v(6.25, 10.83) * mm});
            skPoint(sketch, "E12.11.68", {"position": v(10.16, 10.7) * mm});
            skPoint(sketch, "E12.11.69", {"position": v(8.6, 9.07) * mm});
            skPoint(sketch, "E12.11.70", {"position": v(6.71, 15.62) * mm});
            skPoint(sketch, "E12.11.71", {"position": v(8.5, 14.72) * mm});
            skPoint(sketch, "E12.11.72", {"position": v(13.07, 10.87) * mm});
            skPoint(sketch, "E12.11.73", {"position": v(11.7, 12.33) * mm});
            skPoint(sketch, "E12.11.74", {"position": v(8.5, 14.72) * mm});
            skPoint(sketch, "E12.11.75", {"position": v(6.25, 10.83) * mm});
            skPoint(sketch, "E12.11.76", {"position": v(13.07, 10.87) * mm});
            skPoint(sketch, "E12.11.77", {"position": v(7.38, 12.77) * mm});
            skPoint(sketch, "E12.11.78", {"position": v(6.71, 15.62) * mm});
            skPoint(sketch, "E12.11.79", {"position": v(10.16, 10.7) * mm});
            skPoint(sketch, "E12.11.80", {"position": v(11.7, 12.33) * mm});
            skPoint(sketch, "E12.11.81", {"position": v(8.6, 9.07) * mm});
            skPoint(sketch, "E12.11.82", {"position": v(8.5, 14.72) * mm});
            skPoint(sketch, "E12.11.83", {"position": v(13.07, 10.87) * mm});
            skPoint(sketch, "E12.11.84", {"position": v(6.71, 15.62) * mm});
            skPoint(sketch, "E12.11.85", {"position": v(8.6, 9.07) * mm});
            skPoint(sketch, "E12.11.86", {"position": v(7.38, 12.77) * mm});
            skPoint(sketch, "E12.11.87", {"position": v(10.16, 10.7) * mm});
            skPoint(sketch, "E12.11.88", {"position": v(6.25, 10.83) * mm});
            skPoint(sketch, "E12.11.89", {"position": v(6.71, 15.62) * mm});
            skPoint(sketch, "E12.11.90", {"position": v(6.25, 10.83) * mm});
            skPoint(sketch, "E12.11.91", {"position": v(8.6, 9.07) * mm});
            skPoint(sketch, "E12.11.92", {"position": v(7.38, 12.77) * mm});
            skPoint(sketch, "E12.11.93", {"position": v(10.16, 10.7) * mm});
            skPoint(sketch, "E12.11.94", {"position": v(13.07, 10.87) * mm});
            skPoint(sketch, "E12.11.95", {"position": v(10.16, 10.7) * mm});
            skPoint(sketch, "E12.11.96", {"position": v(8.6, 9.07) * mm});
            skPoint(sketch, "E12.11.97", {"position": v(7.38, 12.77) * mm});
            skPoint(sketch, "E12.11.98", {"position": v(6.25, 10.83) * mm});
            skPoint(sketch, "E12.11.99", {"position": v(6.71, 15.62) * mm});
            skPoint(sketch, "E12.11.100", {"position": v(13.07, 10.87) * mm});
            skArc(sketch, "E12.11.101", {"start": v(10.94, 10.74) * mm, "mid": v(10.22, 10.56) * mm, "end": v(9.61, 10.12) * mm});
            skArc(sketch, "E12.11.102", {"start": v(7.91, 9.68) * mm, "mid": v(8.6, 9.45) * mm, "end": v(9.27, 9.76) * mm});
            skArc(sketch, "E12.11.103", {"start": v(6.73, 11.66) * mm, "mid": v(6.62, 10.94) * mm, "end": v(7.03, 10.33) * mm});
            skArc(sketch, "E12.11.104", {"start": v(10.94, 10.74) * mm, "mid": v(10.22, 10.56) * mm, "end": v(9.61, 10.12) * mm});
            skArc(sketch, "E12.11.105", {"start": v(13.4, 10.46) * mm, "mid": v(13.03, 10.75) * mm, "end": v(12.56, 10.84) * mm});
            skArc(sketch, "E12.11.106", {"start": v(7.91, 9.68) * mm, "mid": v(8.6, 9.45) * mm, "end": v(9.27, 9.76) * mm});
            skArc(sketch, "E12.11.107", {"start": v(6.73, 11.66) * mm, "mid": v(6.62, 10.94) * mm, "end": v(7.03, 10.33) * mm});
            skArc(sketch, "E12.11.108", {"start": v(6.83, 15.12) * mm, "mid": v(6.61, 15.54) * mm, "end": v(6.22, 15.82) * mm});
            skArc(sketch, "E12.11.109", {"start": v(7.91, 9.68) * mm, "mid": v(8.6, 9.45) * mm, "end": v(9.27, 9.76) * mm});
            skArc(sketch, "E12.11.110", {"start": v(6.73, 11.66) * mm, "mid": v(6.62, 10.94) * mm, "end": v(7.03, 10.33) * mm});
            skArc(sketch, "E12.11.111", {"start": v(10.94, 10.74) * mm, "mid": v(10.22, 10.56) * mm, "end": v(9.61, 10.12) * mm});
            skArc(sketch, "E12.11.112", {"start": v(13.4, 10.46) * mm, "mid": v(13.03, 10.75) * mm, "end": v(12.56, 10.84) * mm});
            skArc(sketch, "E12.11.113", {"start": v(6.83, 15.12) * mm, "mid": v(6.61, 15.54) * mm, "end": v(6.22, 15.82) * mm});
            skArc(sketch, "E12.11.114", {"start": v(7.91, 9.68) * mm, "mid": v(8.6, 9.45) * mm, "end": v(9.27, 9.76) * mm});
            skArc(sketch, "E12.11.115", {"start": v(6.83, 15.12) * mm, "mid": v(6.61, 15.54) * mm, "end": v(6.22, 15.82) * mm});
            skArc(sketch, "E12.11.116", {"start": v(6.73, 11.66) * mm, "mid": v(6.62, 10.94) * mm, "end": v(7.03, 10.33) * mm});
            skArc(sketch, "E12.11.117", {"start": v(10.94, 10.74) * mm, "mid": v(10.22, 10.56) * mm, "end": v(9.61, 10.12) * mm});
            skArc(sketch, "E12.11.118", {"start": v(13.4, 10.46) * mm, "mid": v(13.03, 10.75) * mm, "end": v(12.56, 10.84) * mm});
            skArc(sketch, "E12.11.119", {"start": v(6.83, 15.12) * mm, "mid": v(6.61, 15.54) * mm, "end": v(6.22, 15.82) * mm});
            skArc(sketch, "E12.11.120", {"start": v(6.73, 11.66) * mm, "mid": v(6.62, 10.94) * mm, "end": v(7.03, 10.33) * mm});
            skArc(sketch, "E12.11.121", {"start": v(7.91, 9.68) * mm, "mid": v(8.6, 9.45) * mm, "end": v(9.27, 9.76) * mm});
            skArc(sketch, "E12.11.122", {"start": v(10.94, 10.74) * mm, "mid": v(10.22, 10.56) * mm, "end": v(9.61, 10.12) * mm});
            skArc(sketch, "E12.11.123", {"start": v(13.4, 10.46) * mm, "mid": v(13.03, 10.75) * mm, "end": v(12.56, 10.84) * mm});
            skArc(sketch, "E12.11.124", {"start": v(6.83, 15.12) * mm, "mid": v(6.61, 15.54) * mm, "end": v(6.22, 15.82) * mm});
            skArc(sketch, "E12.11.125", {"start": v(7.91, 9.68) * mm, "mid": v(8.6, 9.45) * mm, "end": v(9.27, 9.76) * mm});
            skArc(sketch, "E12.11.126", {"start": v(6.73, 11.66) * mm, "mid": v(6.62, 10.94) * mm, "end": v(7.03, 10.33) * mm});
            skArc(sketch, "E12.11.127", {"start": v(10.94, 10.74) * mm, "mid": v(10.22, 10.56) * mm, "end": v(9.61, 10.12) * mm});
            skArc(sketch, "E12.11.128", {"start": v(13.4, 10.46) * mm, "mid": v(13.03, 10.75) * mm, "end": v(12.56, 10.84) * mm});
            skArc(sketch, "E12.11.129", {"start": v(7.91, 9.68) * mm, "mid": v(8.6, 9.45) * mm, "end": v(9.27, 9.76) * mm});
            skArc(sketch, "E12.11.130", {"start": v(6.83, 15.12) * mm, "mid": v(6.61, 15.54) * mm, "end": v(6.22, 15.82) * mm});
            skArc(sketch, "E12.11.131", {"start": v(6.73, 11.66) * mm, "mid": v(6.62, 10.94) * mm, "end": v(7.03, 10.33) * mm});
            skArc(sketch, "E12.11.132", {"start": v(13.4, 10.46) * mm, "mid": v(13.03, 10.75) * mm, "end": v(12.56, 10.84) * mm});
            skArc(sketch, "E12.11.133", {"start": v(10.94, 10.74) * mm, "mid": v(10.22, 10.56) * mm, "end": v(9.61, 10.12) * mm});
            skArc(sketch, "E12.11.134", {"start": v(10.94, 10.74) * mm, "mid": v(10.22, 10.56) * mm, "end": v(9.61, 10.12) * mm});
            skArc(sketch, "E12.11.135", {"start": v(13.4, 10.46) * mm, "mid": v(13.03, 10.75) * mm, "end": v(12.56, 10.84) * mm});
            skArc(sketch, "E12.11.136", {"start": v(7.91, 9.68) * mm, "mid": v(8.6, 9.45) * mm, "end": v(9.27, 9.76) * mm});
            skArc(sketch, "E12.11.137", {"start": v(6.83, 15.12) * mm, "mid": v(6.61, 15.54) * mm, "end": v(6.22, 15.82) * mm});
            skArc(sketch, "E12.11.138", {"start": v(6.73, 11.66) * mm, "mid": v(6.62, 10.94) * mm, "end": v(7.03, 10.33) * mm});
            skArc(sketch, "E12.11.139", {"start": v(7.91, 9.68) * mm, "mid": v(8.6, 9.45) * mm, "end": v(9.27, 9.76) * mm});
            skArc(sketch, "E12.11.140", {"start": v(6.73, 11.66) * mm, "mid": v(6.62, 10.94) * mm, "end": v(7.03, 10.33) * mm});
            skArc(sketch, "E12.11.141", {"start": v(10.94, 10.74) * mm, "mid": v(10.22, 10.56) * mm, "end": v(9.61, 10.12) * mm});
            skArc(sketch, "E12.11.142", {"start": v(13.4, 10.46) * mm, "mid": v(13.03, 10.75) * mm, "end": v(12.56, 10.84) * mm});
            skArc(sketch, "E12.11.143", {"start": v(6.83, 15.12) * mm, "mid": v(6.61, 15.54) * mm, "end": v(6.22, 15.82) * mm});
            skArc(sketch, "E12.11.144", {"start": v(6.83, 15.12) * mm, "mid": v(6.61, 15.54) * mm, "end": v(6.22, 15.82) * mm});
            skArc(sketch, "E12.11.145", {"start": v(10.94, 10.74) * mm, "mid": v(10.22, 10.56) * mm, "end": v(9.61, 10.12) * mm});
            skArc(sketch, "E12.11.146", {"start": v(7.91, 9.68) * mm, "mid": v(8.6, 9.45) * mm, "end": v(9.27, 9.76) * mm});
            skArc(sketch, "E12.11.147", {"start": v(6.73, 11.66) * mm, "mid": v(6.62, 10.94) * mm, "end": v(7.03, 10.33) * mm});
            skArc(sketch, "E12.11.148", {"start": v(13.4, 10.46) * mm, "mid": v(13.03, 10.75) * mm, "end": v(12.56, 10.84) * mm});
            skArc(sketch, "E12.11.149", {"start": v(7.91, 9.68) * mm, "mid": v(8.6, 9.45) * mm, "end": v(9.27, 9.76) * mm});
            skArc(sketch, "E12.11.150", {"start": v(6.83, 15.12) * mm, "mid": v(6.61, 15.54) * mm, "end": v(6.22, 15.82) * mm});
            skArc(sketch, "E12.11.151", {"start": v(6.73, 11.66) * mm, "mid": v(6.62, 10.94) * mm, "end": v(7.03, 10.33) * mm});
            skArc(sketch, "E12.11.152", {"start": v(13.4, 10.46) * mm, "mid": v(13.03, 10.75) * mm, "end": v(12.56, 10.84) * mm});
            skArc(sketch, "E12.11.153", {"start": v(10.94, 10.74) * mm, "mid": v(10.22, 10.56) * mm, "end": v(9.61, 10.12) * mm});
            skArc(sketch, "E12.11.154", {"start": v(6.83, 15.12) * mm, "mid": v(6.61, 15.54) * mm, "end": v(6.22, 15.82) * mm});
            skArc(sketch, "E12.11.155", {"start": v(13.4, 10.46) * mm, "mid": v(13.03, 10.75) * mm, "end": v(12.56, 10.84) * mm});
            skArc(sketch, "E12.11.156", {"start": v(7.91, 9.68) * mm, "mid": v(8.6, 9.45) * mm, "end": v(9.27, 9.76) * mm});
            skArc(sketch, "E12.11.157", {"start": v(10.94, 10.74) * mm, "mid": v(10.22, 10.56) * mm, "end": v(9.61, 10.12) * mm});
            skArc(sketch, "E12.11.158", {"start": v(6.73, 11.66) * mm, "mid": v(6.62, 10.94) * mm, "end": v(7.03, 10.33) * mm});
            skArc(sketch, "E12.11.159", {"start": v(6.83, 15.12) * mm, "mid": v(6.61, 15.54) * mm, "end": v(6.22, 15.82) * mm});
            skArc(sketch, "E12.11.160", {"start": v(6.73, 11.66) * mm, "mid": v(6.62, 10.94) * mm, "end": v(7.03, 10.33) * mm});
            skArc(sketch, "E12.11.161", {"start": v(7.91, 9.68) * mm, "mid": v(8.6, 9.45) * mm, "end": v(9.27, 9.76) * mm});
            skArc(sketch, "E12.11.162", {"start": v(10.94, 10.74) * mm, "mid": v(10.22, 10.56) * mm, "end": v(9.61, 10.12) * mm});
            skArc(sketch, "E12.11.163", {"start": v(13.4, 10.46) * mm, "mid": v(13.03, 10.75) * mm, "end": v(12.56, 10.84) * mm});
            skArc(sketch, "E12.11.164", {"start": v(6.98, 12.09) * mm, "mid": v(7.23, 12.8) * mm, "end": v(7.2, 13.54) * mm});
            skArc(sketch, "E12.11.165", {"start": v(7.91, 9.68) * mm, "mid": v(7.48, 10.01) * mm, "end": v(7.03, 10.33) * mm});
            skArc(sketch, "E12.11.166", {"start": v(13.4, 10.46) * mm, "mid": v(13.03, 10.75) * mm, "end": v(12.56, 10.84) * mm});
            skLineSegment(sketch, "E12.11.167", {"start": v(10.94, 10.74) * mm, "end": v(12.56, 10.84) * mm});
            skLineSegment(sketch, "E12.11.168", {"start": v(7.2, 13.54) * mm, "end": v(6.83, 15.12) * mm});
            skArc(sketch, "E12.11.169", {"start": v(6.83, 15.12) * mm, "mid": v(6.61, 15.54) * mm, "end": v(6.22, 15.82) * mm});
            skLineSegment(sketch, "E12.11.170", {"start": v(7.2, 13.54) * mm, "end": v(6.83, 15.12) * mm});
            skLineSegment(sketch, "E12.11.171", {"start": v(10.94, 10.74) * mm, "end": v(12.56, 10.84) * mm});
            skLineSegment(sketch, "E12.11.172", {"start": v(9.27, 9.76) * mm, "end": v(9.61, 10.12) * mm});
            skArc(sketch, "E12.11.173", {"start": v(7.91, 9.68) * mm, "mid": v(7.48, 10.01) * mm, "end": v(7.03, 10.33) * mm});
            skArc(sketch, "E12.11.174", {"start": v(6.98, 12.09) * mm, "mid": v(7.23, 12.8) * mm, "end": v(7.2, 13.54) * mm});
            skLineSegment(sketch, "E12.11.175", {"start": v(10.94, 10.74) * mm, "end": v(12.56, 10.84) * mm});
            skArc(sketch, "E12.11.176", {"start": v(6.98, 12.09) * mm, "mid": v(7.23, 12.8) * mm, "end": v(7.2, 13.54) * mm});
            skLineSegment(sketch, "E12.11.177", {"start": v(7.2, 13.54) * mm, "end": v(6.83, 15.12) * mm});
            skLineSegment(sketch, "E12.11.178", {"start": v(9.27, 9.76) * mm, "end": v(9.61, 10.12) * mm});
            skArc(sketch, "E12.11.179", {"start": v(7.91, 9.68) * mm, "mid": v(7.48, 10.01) * mm, "end": v(7.03, 10.33) * mm});
            skLineSegment(sketch, "E12.11.180", {"start": v(7.2, 13.54) * mm, "end": v(6.83, 15.12) * mm});
            skArc(sketch, "E12.11.181", {"start": v(6.98, 12.09) * mm, "mid": v(7.23, 12.8) * mm, "end": v(7.2, 13.54) * mm});
            skArc(sketch, "E12.11.182", {"start": v(7.91, 9.68) * mm, "mid": v(7.48, 10.01) * mm, "end": v(7.03, 10.33) * mm});
            skLineSegment(sketch, "E12.11.183", {"start": v(9.27, 9.76) * mm, "end": v(9.61, 10.12) * mm});
            skLineSegment(sketch, "E12.11.184", {"start": v(10.94, 10.74) * mm, "end": v(12.56, 10.84) * mm});
            skArc(sketch, "E12.11.185", {"start": v(6.98, 12.09) * mm, "mid": v(7.23, 12.8) * mm, "end": v(7.2, 13.54) * mm});
            skLineSegment(sketch, "E12.11.186", {"start": v(7.2, 13.54) * mm, "end": v(6.83, 15.12) * mm});
            skLineSegment(sketch, "E12.11.187", {"start": v(10.94, 10.74) * mm, "end": v(12.56, 10.84) * mm});
            skArc(sketch, "E12.11.188", {"start": v(7.91, 9.68) * mm, "mid": v(7.48, 10.01) * mm, "end": v(7.03, 10.33) * mm});
            skLineSegment(sketch, "E12.11.189", {"start": v(9.27, 9.76) * mm, "end": v(9.61, 10.12) * mm});
            skArc(sketch, "E12.11.190", {"start": v(6.98, 12.09) * mm, "mid": v(7.23, 12.8) * mm, "end": v(7.2, 13.54) * mm});
            skLineSegment(sketch, "E12.11.191", {"start": v(10.94, 10.74) * mm, "end": v(12.56, 10.84) * mm});
            skArc(sketch, "E12.11.192", {"start": v(7.91, 9.68) * mm, "mid": v(7.48, 10.01) * mm, "end": v(7.03, 10.33) * mm});
            skLineSegment(sketch, "E12.11.193", {"start": v(7.2, 13.54) * mm, "end": v(6.83, 15.12) * mm});
            skLineSegment(sketch, "E12.11.194", {"start": v(9.27, 9.76) * mm, "end": v(9.61, 10.12) * mm});
            skLineSegment(sketch, "E12.11.195", {"start": v(7.2, 13.54) * mm, "end": v(6.83, 15.12) * mm});
            skArc(sketch, "E12.11.196", {"start": v(7.91, 9.68) * mm, "mid": v(7.48, 10.01) * mm, "end": v(7.03, 10.33) * mm});
            skLineSegment(sketch, "E12.11.197", {"start": v(10.94, 10.74) * mm, "end": v(12.56, 10.84) * mm});
            skArc(sketch, "E12.11.198", {"start": v(6.98, 12.09) * mm, "mid": v(7.23, 12.8) * mm, "end": v(7.2, 13.54) * mm});
            skLineSegment(sketch, "E12.11.199", {"start": v(9.27, 9.76) * mm, "end": v(9.61, 10.12) * mm});
            skLineSegment(sketch, "E12.11.200", {"start": v(10.94, 10.74) * mm, "end": v(12.56, 10.84) * mm});
            skArc(sketch, "E12.11.201", {"start": v(7.91, 9.68) * mm, "mid": v(7.48, 10.01) * mm, "end": v(7.03, 10.33) * mm});
            skLineSegment(sketch, "E12.11.202", {"start": v(6.98, 12.09) * mm, "end": v(6.73, 11.66) * mm});
            skLineSegment(sketch, "E12.11.203", {"start": v(7.2, 13.54) * mm, "end": v(6.83, 15.12) * mm});
            skArc(sketch, "E12.11.204", {"start": v(6.98, 12.09) * mm, "mid": v(7.23, 12.8) * mm, "end": v(7.2, 13.54) * mm});
            skLineSegment(sketch, "E12.11.205", {"start": v(9.27, 9.76) * mm, "end": v(9.61, 10.12) * mm});
            skLineSegment(sketch, "E12.11.206", {"start": v(6.98, 12.09) * mm, "end": v(6.73, 11.66) * mm});
            skLineSegment(sketch, "E12.11.207", {"start": v(9.27, 9.76) * mm, "end": v(9.61, 10.12) * mm});
            skArc(sketch, "E12.11.208", {"start": v(6.98, 12.09) * mm, "mid": v(7.23, 12.8) * mm, "end": v(7.2, 13.54) * mm});
            skLineSegment(sketch, "E12.11.209", {"start": v(10.94, 10.74) * mm, "end": v(12.56, 10.84) * mm});
            skArc(sketch, "E12.11.210", {"start": v(7.91, 9.68) * mm, "mid": v(7.48, 10.01) * mm, "end": v(7.03, 10.33) * mm});
            skLineSegment(sketch, "E12.11.211", {"start": v(7.2, 13.54) * mm, "end": v(6.83, 15.12) * mm});
            skArc(sketch, "E12.11.212", {"start": v(7.91, 9.68) * mm, "mid": v(7.48, 10.01) * mm, "end": v(7.03, 10.33) * mm});
            skLineSegment(sketch, "E12.11.213", {"start": v(7.2, 13.54) * mm, "end": v(6.83, 15.12) * mm});
            skLineSegment(sketch, "E12.11.214", {"start": v(10.94, 10.74) * mm, "end": v(12.56, 10.84) * mm});
            skLineSegment(sketch, "E12.11.215", {"start": v(6.98, 12.09) * mm, "end": v(6.73, 11.66) * mm});
            skArc(sketch, "E12.11.216", {"start": v(6.98, 12.09) * mm, "mid": v(7.23, 12.8) * mm, "end": v(7.2, 13.54) * mm});
            skLineSegment(sketch, "E12.11.217", {"start": v(9.27, 9.76) * mm, "end": v(9.61, 10.12) * mm});
            skLineSegment(sketch, "E12.11.218", {"start": v(7.2, 13.54) * mm, "end": v(6.83, 15.12) * mm});
            skArc(sketch, "E12.11.219", {"start": v(6.98, 12.09) * mm, "mid": v(7.23, 12.8) * mm, "end": v(7.2, 13.54) * mm});
            skLineSegment(sketch, "E12.11.220", {"start": v(10.94, 10.74) * mm, "end": v(12.56, 10.84) * mm});
            skLineSegment(sketch, "E12.11.221", {"start": v(9.27, 9.76) * mm, "end": v(9.61, 10.12) * mm});
            skArc(sketch, "E12.11.222", {"start": v(7.91, 9.68) * mm, "mid": v(7.48, 10.01) * mm, "end": v(7.03, 10.33) * mm});
            skLineSegment(sketch, "E12.11.223", {"start": v(6.98, 12.09) * mm, "end": v(6.73, 11.66) * mm});
            skLineSegment(sketch, "E12.11.224", {"start": v(7.2, 13.54) * mm, "end": v(6.83, 15.12) * mm});
            skLineSegment(sketch, "E12.11.225", {"start": v(10.94, 10.74) * mm, "end": v(12.56, 10.84) * mm});
            skLineSegment(sketch, "E12.11.226", {"start": v(6.98, 12.09) * mm, "end": v(6.73, 11.66) * mm});
            skArc(sketch, "E12.11.227", {"start": v(6.98, 12.09) * mm, "mid": v(7.23, 12.8) * mm, "end": v(7.2, 13.54) * mm});
            skLineSegment(sketch, "E12.11.228", {"start": v(9.27, 9.76) * mm, "end": v(9.61, 10.12) * mm});
            skArc(sketch, "E12.11.229", {"start": v(7.91, 9.68) * mm, "mid": v(7.48, 10.01) * mm, "end": v(7.03, 10.33) * mm});
            skArc(sketch, "E12.11.230", {"start": v(7.91, 9.68) * mm, "mid": v(7.48, 10.01) * mm, "end": v(7.03, 10.33) * mm});
            skLineSegment(sketch, "E12.11.231", {"start": v(9.27, 9.76) * mm, "end": v(9.61, 10.12) * mm});
            skLineSegment(sketch, "E12.11.232", {"start": v(7.2, 13.54) * mm, "end": v(6.83, 15.12) * mm});
            skLineSegment(sketch, "E12.11.233", {"start": v(6.98, 12.09) * mm, "end": v(6.73, 11.66) * mm});
            skArc(sketch, "E12.11.234", {"start": v(6.98, 12.09) * mm, "mid": v(7.23, 12.8) * mm, "end": v(7.2, 13.54) * mm});
            skLineSegment(sketch, "E12.11.235", {"start": v(10.94, 10.74) * mm, "end": v(12.56, 10.84) * mm});
            skLineSegment(sketch, "E12.11.236", {"start": v(9.27, 9.76) * mm, "end": v(9.61, 10.12) * mm});
            skLineSegment(sketch, "E12.11.237", {"start": v(6.98, 12.09) * mm, "end": v(6.73, 11.66) * mm});
            skLineSegment(sketch, "E12.11.238", {"start": v(6.98, 12.09) * mm, "end": v(6.73, 11.66) * mm});
            skLineSegment(sketch, "E12.11.239", {"start": v(6.98, 12.09) * mm, "end": v(6.73, 11.66) * mm});
            skLineSegment(sketch, "E12.11.240", {"start": v(6.98, 12.09) * mm, "end": v(6.73, 11.66) * mm});
            skLineSegment(sketch, "E12.11.241", {"start": v(6.98, 12.09) * mm, "end": v(6.73, 11.66) * mm});
            skLineSegment(sketch, "E12.11.242", {"start": v(6.98, 12.09) * mm, "end": v(6.73, 11.66) * mm});
            skLineSegment(sketch, "E12.11.243", {"start": v(6.98, 12.09) * mm, "end": v(6.73, 11.66) * mm});
            skSolve(sketch);
        }
        {
            var Q0;
            Q0 = qSketchRegion(id + "F0", true);
            extrude(context, id + "F1", {"entities" : qUnion([Q0]), "depth" : 15 * mm, "offsetDistance" : 25 * mm});
        }
        {
            var Q0;
            Q0=qCreatedBy(makeId("Top.planeOp"),FACE);
            var sketch = newSketch(context, id + "F2", { "sketchPlane" : qUnion([Q0])});
            skCircle(sketch, "E13", {"center": v(0, 0) * mm, "radius": 17 * mm});
            skCircle(sketch, "E14", {"center": v(0, 0) * mm, "radius": 3 * mm});
            skSolve(sketch);
        }
        {
            var Q0;
            Q0 = qSketchRegion(id + "F2", true);
            extrude(context, id + "F3", {"entities" : qUnion([Q0]), "operationType" : NewBodyOperationType.ADD, "oppositeDirection" : true, "depth" : 10 * mm, "offsetDistance" : 25 * mm});
        }
        {
            var Q0;
            Q0=qCreatedBy(makeId("Front.planeOp"),FACE);
            var sketch = newSketch(context, id + "F4", { "sketchPlane" : qUnion([Q0])});
            skCircle(sketch, "E15", {"center": v(0, -5) * mm, "radius": 1.75 * mm});
            skSolve(sketch);
        }
        {
            var Q0;
            Q0=makeQuery(id+"F4.imprint","IMPRINT",FACE,{"disambiguationData":[TD([[makeQuery(id+"F4.imprint","IMPRINT",EDGE,{"derivedFrom":sQuery(id+"F4.wireOp",EDGE,"E15")}),1.0]])]});
            var Q1;
            Q1=sQuery(id+"F4.wireOp",EDGE,"E15");
            extrude(context, id + "F5", {"entities" : qUnion([Q0]), "operationType" : NewBodyOperationType.REMOVE, "surfaceEntities" : qUnion([Q1]), "endBound" : BoundingType.THROUGH_ALL, "oppositeDirection" : true, "depth" : 25 * mm, "offsetDistance" : 25 * mm});
        }
        {
            var Q0;
            Q0=makeQuery(id+"F3.opExtrude","CAP_FACE",FACE,{"disambiguationData":[OSD([sQuery(id+"F2.wireOp",EDGE,"E13"),sQuery(id+"F2.wireOp",EDGE,"E14")])],"isStart":false});
            var sketch = newSketch(context, id + "F6", { "sketchPlane" : qUnion([Q0])});
            skLineSegment(sketch, "E16.bottom", {"start": v(2.5, -9) * mm, "end": v(-2.5, -9) * mm});
            skLineSegment(sketch, "E16.top", {"start": v(2.5, -7) * mm, "end": v(-2.5, -7) * mm});
            skLineSegment(sketch, "E16.left", {"start": v(2.5, -9) * mm, "end": v(2.5, -7) * mm});
            skLineSegment(sketch, "E16.right", {"start": v(-2.5, -9) * mm, "end": v(-2.5, -7) * mm});
            skPoint(sketch, "E16.middle", {"position": v(0, -8) * mm});
            skSolve(sketch);
        }
        {
            var Q0;
            Q0 = qSketchRegion(id + "F6", true);
            extrude(context, id + "F7", {"entities" : qUnion([Q0]), "operationType" : NewBodyOperationType.REMOVE, "oppositeDirection" : true, "depth" : 9 * mm, "offsetDistance" : 25 * mm});
        }
    });
